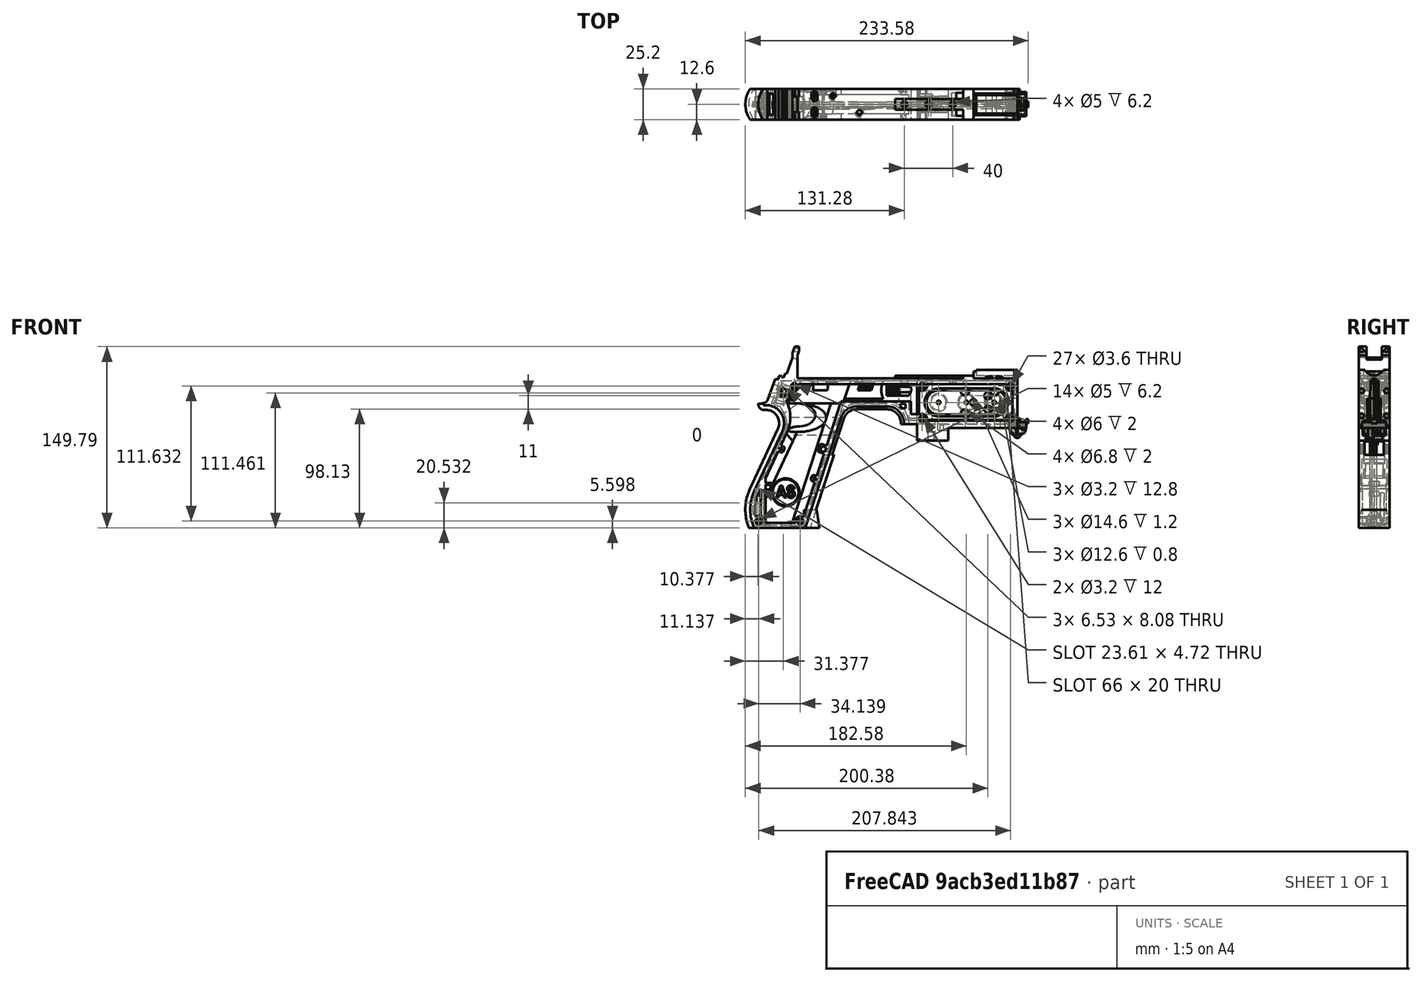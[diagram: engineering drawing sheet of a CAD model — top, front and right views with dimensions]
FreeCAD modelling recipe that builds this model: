
FCSTD DOCUMENT  (FreeCAD 1.0R39319 (Git))
Label: PICON-OF_ver_34_prova_spazio_switch_alette
License: All rights reserved
LicenseURL: https://en.wikipedia.org/wiki/All_rights_reserved
objects: Sketcher::SketchObject×119, Part::Extrusion×75, Part::Cut×47, PartDesign::Pad×19, PartDesign::Pocket×14, PartDesign::Chamfer×14, PartDesign::Body×8, Part::MultiFuse×6, PartDesign::Fillet×6, PartDesign::SubtractivePipe×4, Part::Part2DObjectPython×4, PartDesign::SubtractiveLoft×4, PartDesign::Plane×2, PartDesign::SubShapeBinder×2, Part::Sweep×1, PartDesign::ShapeBinder×1, PartDesign::FeatureBase×1, Part::Cone×1, Part::Chamfer×1, Mesh::Feature×1, +1 more types
note: 572 computed .brp shape members not serialized (recipe doc carries the construction recipe); baked Part::Feature solids carry a one-line shape summary decoded from their .brp

FEATURE [Sketcher::SketchObject] Sketch  label="corpo principale"
  ArcFitTolerance = 1e-06
  AttacherType = Attacher::AttachEngine3D
  AttachmentSupport = -> [XZ_Plane]
  FullyConstrained = true
  MakeInternals = false
  MapMode = 5
  Placement = pos=(0,0,0) rot=(1,0,0;1.5708rad)
  sketch-geometry (65):
    g0: LineSegment StartX=0 StartY=0 StartZ=0 EndX=-57.2 EndY=0 EndZ=0
    g1: LineSegment StartX=-57.2 StartY=0 StartZ=0 EndX=-57.2 EndY=-10.4 EndZ=0
    g2: LineSegment StartX=-57.2 StartY=-10.4 StartZ=0 EndX=-82.8 EndY=-10.4 EndZ=0
    g3: LineSegment StartX=-82.8 StartY=-10.4 StartZ=0 EndX=-82.8 EndY=3.2 EndZ=0
    g4: LineSegment StartX=-82.8 StartY=3.2 StartZ=0 EndX=-93.6 EndY=3.2 EndZ=0
    g5: LineSegment StartX=-93.6 StartY=3.2 StartZ=0 EndX=-93.6 EndY=4 EndZ=0
    g6: LineSegment StartX=-107.6 StartY=18 StartZ=0 EndX=-132.428 EndY=18 EndZ=0
    g7: LineSegment StartX=-145.743 StartY=8.32624 StartZ=0 EndX=-175.232 EndY=-82.4316 EndZ=0
    g8: LineSegment StartX=-175.232 StartY=-82.4316 StartZ=0 EndX=-217.232 EndY=-82.4316 EndZ=0
    g9: LineSegment StartX=-217.232 StartY=-52.1862 StartZ=0 EndX=-193.988 EndY=-2.33927 EndZ=0
    g10: LineSegment StartX=-206.196 StartY=23.0857 StartZ=0 EndX=-199.861 EndY=40.4914 EndZ=0
    g11: LineSegment StartX=-199.861 StartY=40.4914 StartZ=0 EndX=-197.061 EndY=40.4914 EndZ=0
    g12: LineSegment StartX=-197.061 StartY=40.4914 StartZ=0 EndX=-197.061 EndY=42.8914 EndZ=0
    g13: LineSegment StartX=-197.061 StartY=42.8914 StartZ=0 EndX=-194.261 EndY=42.8914 EndZ=0
    g14: LineSegment StartX=-194.261 StartY=42.8914 StartZ=0 EndX=-194.535 EndY=42.1397 EndZ=0
    g15: LineSegment StartX=-194.535 StartY=42.1397 StartZ=0 EndX=-193.031 EndY=41.5924 EndZ=0
    g16: LineSegment StartX=-193.031 StartY=41.5924 StartZ=0 EndX=-191.663 EndY=45.3512 EndZ=0
    g17: LineSegment StartX=-191.663 StartY=45.3512 StartZ=0 EndX=-190.536 EndY=44.9408 EndZ=0
    g18: LineSegment StartX=-190.536 StartY=44.9408 StartZ=0 EndX=-185.747 EndY=58.0965 EndZ=0
    g19: LineSegment StartX=-185.747 StartY=58.0965 StartZ=0 EndX=-185.747 EndY=62.0965 EndZ=0
    g20: LineSegment StartX=-185.747 StartY=62.0965 StartZ=0 EndX=-183.832 EndY=67.3588 EndZ=0
    g21: LineSegment StartX=-183.832 StartY=67.3588 StartZ=0 EndX=-180.232 EndY=67.3588 EndZ=0
    g22: LineSegment StartX=-180.232 StartY=67.3588 StartZ=0 EndX=-180.232 EndY=63.7588 EndZ=0
    g23: LineSegment StartX=-180.232 StartY=63.7588 StartZ=0 EndX=-181.6 EndY=60 EndZ=0
    g24: LineSegment StartX=-181.6 StartY=60 StartZ=0 EndX=-181.6 EndY=41.2 EndZ=0
    g25: LineSegment StartX=-181.6 StartY=41.2 StartZ=0 EndX=-100.8 EndY=41.2 EndZ=0
    g26: LineSegment StartX=-36 StartY=43.2 StartZ=0 EndX=-36 EndY=41.2 EndZ=0
    g27: LineSegment StartX=0 StartY=48 StartZ=0 EndX=0 EndY=0 EndZ=0
    g28: LineSegment StartX=-209.901 StartY=19.85 StartZ=0 EndX=-209.901 EndY=20.1 EndZ=0
    g29: LineSegment StartX=-208.001 StartY=22 StartZ=0 EndX=-207.747 EndY=22 EndZ=0
    g30: LineSegment StartX=-207.583 StartY=19 StartZ=0 EndX=-209.051 EndY=19 EndZ=0
    g31: ArcOfCircle CenterX=-208.001 CenterY=20.1 CenterZ=0 NormalX=0 NormalY=0 NormalZ=1 AngleXU=0 Radius=1.9 StartAngle=1.5708 EndAngle=3.14159
    g32: GeomPoint [constr] X=-209.901 Y=22 Z=0
    g33: ArcOfCircle CenterX=-209.051 CenterY=19.85 CenterZ=0 NormalX=0 NormalY=0 NormalZ=1 AngleXU=0 Radius=0.85 StartAngle=3.14159 EndAngle=4.71239
    g34: GeomPoint [constr] X=-209.901 Y=19 Z=0
    g35: ArcOfCircle CenterX=-207.747 CenterY=23.65 CenterZ=0 NormalX=0 NormalY=0 NormalZ=1 AngleXU=0 Radius=1.65 StartAngle=4.71239 EndAngle=5.93412
    g36: GeomPoint [constr] X=-206.591 Y=22 Z=0
    g37: LineSegment StartX=-4 StartY=6 StartZ=0 EndX=-4 EndY=36.4 EndZ=0
    g38: LineSegment StartX=-4 StartY=36.4 StartZ=0 EndX=-185.2 EndY=36.4 EndZ=0
    g39: LineSegment StartX=-185.2 StartY=36.4 StartZ=0 EndX=-190.441 EndY=22 EndZ=0
    g40: LineSegment StartX=-214.575 StartY=-78.4316 StartZ=0 EndX=-178.142 EndY=-78.4316 EndZ=0
    g41: LineSegment StartX=-178.142 StartY=-78.4316 StartZ=0 EndX=-145.51 EndY=22 EndZ=0
    g42: LineSegment StartX=-145.51 StartY=22 StartZ=0 EndX=-87.91 EndY=22 EndZ=0
    g43: LineSegment StartX=-87.91 StartY=22 StartZ=0 EndX=-87.91 EndY=11.6 EndZ=0
    g44: LineSegment StartX=-87.91 StartY=11.6 StartZ=0 EndX=-80.11 EndY=11.6 EndZ=0
    g45: LineSegment StartX=-80.11 StartY=11.6 StartZ=0 EndX=-80.11 EndY=6 EndZ=0
    g46: LineSegment StartX=-80.11 StartY=6 StartZ=0 EndX=-4 EndY=6 EndZ=0
    g47: LineSegment StartX=-190.363 StartY=-4.02975 StartZ=0 EndX=-213.607 EndY=-53.8767 EndZ=0
    g48: ArcOfCircle CenterX=-132.428 CenterY=4 CenterZ=0 NormalX=0 NormalY=0 NormalZ=1 AngleXU=0 Radius=14 StartAngle=1.5708 EndAngle=2.82743
    g49: GeomPoint [constr] X=-142.6 Y=18 Z=0
    g50: ArcOfCircle CenterX=-107.6 CenterY=4 CenterZ=0 NormalX=0 NormalY=0 NormalZ=1 AngleXU=0 Radius=14 StartAngle=0 EndAngle=1.5708
    g51: GeomPoint [constr] X=-93.6 Y=18 Z=0
    g52: ArcOfCircle CenterX=-184.801 CenterY=-67.3089 CenterZ=0 NormalX=0 NormalY=0 NormalZ=1 AngleXU=0 Radius=35.7833 StartAngle=2.70526 EndAngle=3.57792
    g53: ArcOfCircle CenterX=-207.583 CenterY=4 CenterZ=0 NormalX=0 NormalY=0 NormalZ=1 AngleXU=0 Radius=15 StartAngle=5.84685 EndAngle=7.85398
    g54: LineSegment [constr] StartX=-213.607 StartY=-53.8767 StartZ=0 EndX=-217.232 EndY=-52.1862 EndZ=0
    g55: ArcOfCircle CenterX=-184.801 CenterY=-67.3089 CenterZ=0 NormalX=0 NormalY=0 NormalZ=1 AngleXU=0 Radius=31.7833 StartAngle=2.70526 EndAngle=3.49911
    g56: ArcOfCircle CenterX=-218.095 CenterY=8.90192 CenterZ=0 NormalX=0 NormalY=0 NormalZ=1 AngleXU=0 Radius=30.5989 StartAngle=5.84685 EndAngle=6.72553
    g57: LineSegment StartX=-44.6 StartY=43.2 StartZ=0 EndX=-36 EndY=43.2 EndZ=0
    g58: LineSegment StartX=-100.8 StartY=41.2 StartZ=0 EndX=-44.6 EndY=41.2 EndZ=0
    g59: LineSegment StartX=-44.6 StartY=41.2 StartZ=0 EndX=-44.6 EndY=43.2 EndZ=0
    g60: LineSegment StartX=-2.4 StartY=48 StartZ=0 EndX=0 EndY=48 EndZ=0
    g61: LineSegment StartX=-36 StartY=41.2 StartZ=0 EndX=-2.4 EndY=41.2 EndZ=0
    g62: LineSegment StartX=-2.4 StartY=41.2 StartZ=0 EndX=-2.4 EndY=48 EndZ=0
    g63: LineSegment [constr] StartX=-181.6 StartY=36.4 StartZ=0 EndX=-152.209 EndY=36.4 EndZ=0
    g64: LineSegment [constr] StartX=-181.6 StartY=36.4 StartZ=0 EndX=-130.41 EndY=36.4 EndZ=0
  constraints (183):
    c: Coincident(g-1,g0)
    c: PointOnObject(g0,g-1)
    c: Coincident(g0,g1)
    c: Vertical(g1)
    c: Coincident(g1,g2)
    c: Horizontal(g2)
    c: Coincident(g2,g3)
    c: Vertical(g3)
    c: Coincident(g3,g4)
    c: Coincident(g4,g5)
    c: Vertical(g5)
    c: Horizontal(g6)
    c: Coincident(g7,g8)
    c: Horizontal(g8)
    c: Coincident(g10,g11)
    c: Horizontal(g11)
    c: Coincident(g11,g12)
    c: Vertical(g12)
    c: Coincident(g12,g13)
    c: Horizontal(g13)
    c: Coincident(g13,g14)
    c: Coincident(g14,g15)
    c: Coincident(g15,g16)
    c: Coincident(g16,g17)
    c: Coincident(g17,g18)
    c: Coincident(g18,g19)
    c: Vertical(g19)
    c: Coincident(g19,g20)
    c: Coincident(g20,g21)
    c: Horizontal(g21)
    c: Coincident(g21,g22)
    c: Vertical(g22)
    c: Coincident(g22,g23)
    c: Coincident(g23,g24)
    c: Vertical(g24)
    c: Coincident(g24,g25)
    c: Horizontal(g25)
    c: Coincident(g57,g26)
    c: Vertical(g26)
    c: Coincident(g26,g61)
    c: PointOnObject(g60,g-2)
    c: Coincident(g60,g27)
    c: Coincident(g27,g0)
    c: DistanceY(g27,g27) = 48
    c: DistanceY(g1,g1) = 10.4
    c: DistanceX(g0,g0) = 57.2
    c: DistanceX(g2,g2) = 25.6
    c: Horizontal(g4)
    c: DistanceY(g3,g3) = 13.6
    c: DistanceX(g4,g4) = 10.8
    c: DistanceY(g5,g51) = 14.8
    c: DistanceX(g49,g51) = 49
    c: Distance(g7,g49) = 105.6
    c: DistanceX(g61,g60) = 36
    c: DistanceX(g25,g25) = 80.8
    c: DistanceY(g24,g24) = 18.8
    c: DistanceY(g22,g22) = 3.6
    c: Distance(g23) = 4
    c: Angle(g-1,g23) = 1.22173
    c: DistanceX(g21,g21) = 3.6
    c: Distance(g20) = 5.6
    c: Angle(g-1,g20) = 1.22173
    c: DistanceY(g19,g19) = 4
    c: Distance(g18) = 14
    c: Angle(g-1,g18) = 1.22173
    c: Distance(g17) = 1.2
    c: Distance(g16) = 4
    c: Angle(g16) = 1.22173
    c: Perpendicular(g18,g17)
    c: Distance(g15) = 1.6
    c: Perpendicular(g16,g15)
    c: Distance(g14) = 0.8
    c: DistanceX(g13,g13) = 2.8
    c: Perpendicular(g15,g14)
    c: DistanceY(g12,g12) = 2.4
    c: DistanceX(g11,g11) = 2.8
    c: Distance(g9) = 55
    c: Angle(g9,g-1) = 2.00713
    c: Horizontal(g29)
    c: Vertical(g28)
    c: Horizontal(g30)
    c: PointOnObject(g32,g29)
    c: PointOnObject(g32,g28)
    c: Tangent(g29,g31) = 1.5708
    c: Tangent(g28,g31) = 1.5708
    c: PointOnObject(g34,g28)
    c: PointOnObject(g34,g30)
    c: Tangent(g28,g33) = 1.5708
    c: Tangent(g30,g33) = 1.5708
    c: PointOnObject(g36,g29)
    c: PointOnObject(g36,g10)
    c: Tangent(g29,g35) = -1.5708
    c: Tangent(g10,g35) = -1.5708
    c: Angle(g-1,g10) = 1.22173
    c: Radius(g35) = 1.65
    c: Vertical(g37)
    c: Coincident(g37,g38)
    c: Horizontal(g38)
    c: Coincident(g38,g39)
    c: Horizontal(g40)
    c: Coincident(g40,g41)
    c: Coincident(g41,g42)
    c: Horizontal(g42)
    c: Coincident(g42,g43)
    c: Vertical(g43)
    c: Coincident(g43,g44)
    c: Horizontal(g44)
    c: Coincident(g44,g45)
    c: Vertical(g45)
    c: Coincident(g45,g46)
    c: Coincident(g46,g37)
    c: Horizontal(g46)
    c: DistanceY(g0,g37) = 6
    c: DistanceX(g37,g0) = 4
    c: DistanceY(g37,g25) = 4.8
    c: DistanceX(g38,g38) = 181.2
    c: DistanceX(g42,g42) = 57.6
    c: DistanceY(g49,g41) = 4
    c: DistanceX(g41,g49) = 2.91
    c: DistanceY(g43,g43) = 10.4
    c: DistanceX(g44,g44) = 7.8
    c: DistanceY(g7,g40) = 4
    c: Distance(g47) = 55
    c: Angle(g-1,g39) = 1.22173
    c: PointOnObject(g49,g7)
    c: PointOnObject(g49,g6)
    c: Tangent(g7,g48) = -1.5708
    c: Tangent(g6,g48) = -1.5708
    c: PointOnObject(g51,g5)
    c: PointOnObject(g51,g6)
    c: Tangent(g5,g50) = -1.5708
    c: Tangent(g6,g50) = -1.5708
    c: Radius(g50) = 14
    c: Radius(g48) = 14
    c: DistanceX(g8,g8) = 42
    c: Angle(g7,g-1) = 1.88496
    c: Parallel(g41,g7)
    c: Parallel(g47,g9)
    c: Coincident(g52,g8)
    c: Tangent(g52,g9) = 1.5708
    c: DistanceX(g9,g8) = 0
    c: Tangent(g53,g9) = -1.5708
    c: Tangent(g53,g30) = -1.5708
    c: Diameter(g53) = 30
    c: DistanceY(g53,g0) = -4
    c: Coincident(g54,g47)
    c: Distance(g54) = 4
    c: Coincident(g54,g9)
    c: Coincident(g55,g40)
    c: Tangent(g55,g47) = -1.5708
    c: Coincident(g52,g55)
    c: Coincident(g56,g39)
    c: Tangent(g56,g47) = 1.5708
    c: Horizontal(g57)
    c: DistanceX(g57,g57) = 8.6
    c: Coincident(g58,g25)
    c: Horizontal(g58)
    c: Coincident(g59,g58)
    c: Vertical(g59)
    c: DistanceY(g58,g57) = 2
    c: DistanceX(g58,g58) = 56.2
    c: Coincident(g59,g57)
    c: DistanceY(g41,g36) = 0
    c: DistanceY(g36,g39) = 0
    c: DistanceY(g28,g28) = 0.25
    c: DistanceX(g30,g36) = 2.46
    c: DistanceX(g28,g29) = 1.9
    c: Coincident(g62,g60)
    c: Horizontal(g60)
    c: DistanceX(g62,g27) = 2.4
    c: Coincident(g61,g62)
    c: DistanceY(g26,g26) = 2
    c: Vertical(g62)
    c: DistanceY(g61,g60) = 6.8
    c: Horizontal(g61)
    c: Distance(g63) = 29.391
    c: PointOnObject(g63,g38)
    c: PointOnObject(g63,g38)
    c: Distance(g64) = 51.19
    c: PointOnObject(g64,g38)
    c: PointOnObject(g64,g38)
    c: DistanceX(g24,g63) = 0
    c: DistanceX(g24,g64) = 0
FEATURE [Part::Extrusion] Extrude  label="Extrude corpo principale"
  Base = -> Sketch
  Dir = (0,-1,2e-16)
  DirMode = 2
  FaceMakerClass = Part::FaceMakerBullseye
  FaceMakerMode = 3
  LengthFwd = 25.2
  LengthRev = 12.6
  Solid = true
  Symmetric = true
FEATURE [Sketcher::SketchObject] Sketch002  label="scavo grilletto"
  ArcFitTolerance = 1e-06
  AttachmentSupport = -> [XZ_Plane]
  ExternalGeometry = -> [Sketch]
  FullyConstrained = true
  MakeInternals = false
  MapMode = 5
  Placement = pos=(0,0,0) rot=(1,0,0;1.5708rad)
  sketch-geometry (4):
    g0: LineSegment StartX=-89.51 StartY=22 StartZ=0 EndX=-152.71 EndY=22 EndZ=0
    g1: LineSegment StartX=-152.71 StartY=22 StartZ=0 EndX=-167.006 EndY=-22 EndZ=0
    g2: LineSegment StartX=-167.006 StartY=-22 StartZ=0 EndX=-89.51 EndY=-22 EndZ=0
    g3: LineSegment StartX=-89.51 StartY=-22 StartZ=0 EndX=-89.51 EndY=22 EndZ=0
  constraints (12):
    c: Horizontal(g0)
    c: Coincident(g0,g1)
    c: Coincident(g1,g2)
    c: Horizontal(g2)
    c: Coincident(g2,g3)
    c: Coincident(g3,g0)
    c: Vertical(g3)
    c: Angle(g1,g0) = 1.88496
    c: DistanceY(g3,g3) = 44
    c: DistanceX(g0,g0) = 63.2
    c: DistanceX(g0,g-3) = 1.6
    c: DistanceY(g-3,g0) = 0
FEATURE [Sketcher::SketchObject] Sketch004  label="traiettoria arrotondamento impugnatura anteriore"
  ArcFitTolerance = 1e-06
  AttachmentSupport = -> [XZ_Plane]
  ExternalGeometry = -> [Sketch]
  FullyConstrained = true
  MakeInternals = false
  MapMode = 5
  Placement = pos=(0,0,0) rot=(1,0,0;1.5708rad)
  sketch-geometry (13):
    g0: LineSegment StartX=-175.232 StartY=-82.4316 StartZ=0 EndX=-145.743 EndY=8.32624 EndZ=0
    g1: LineSegment StartX=-93.6 StartY=3.2 StartZ=0 EndX=-93.6 EndY=4 EndZ=0
    g2: LineSegment StartX=-132.428 StartY=18 StartZ=0 EndX=-107.6 EndY=18 EndZ=0
    g3: ArcOfCircle CenterX=-132.428 CenterY=4 CenterZ=0 NormalX=0 NormalY=0 NormalZ=1 AngleXU=0 Radius=14 StartAngle=1.5708 EndAngle=2.82743
    g4: ArcOfCircle CenterX=-107.6 CenterY=4 CenterZ=0 NormalX=0 NormalY=0 NormalZ=1 AngleXU=0 Radius=14 StartAngle=0 EndAngle=1.5708
    g5: LineSegment StartX=-175.232 StartY=-82.4316 StartZ=0 EndX=-217.232 EndY=-82.4316 EndZ=0
    g6: LineSegment StartX=-217.232 StartY=-52.1862 StartZ=0 EndX=-193.988 EndY=-2.33927 EndZ=0
    g7: LineSegment StartX=-209.051 StartY=19 StartZ=0 EndX=-207.583 EndY=19 EndZ=0
    g8: LineSegment StartX=-209.901 StartY=20.1 StartZ=0 EndX=-209.901 EndY=19.85 EndZ=0
    g9: ArcOfCircle CenterX=-184.801 CenterY=-67.3089 CenterZ=0 NormalX=0 NormalY=0 NormalZ=1 AngleXU=0 Radius=35.7833 StartAngle=2.70526 EndAngle=3.57792
    g10: ArcOfCircle CenterX=-207.583 CenterY=4 CenterZ=0 NormalX=0 NormalY=0 NormalZ=1 AngleXU=0 Radius=15 StartAngle=5.84685 EndAngle=7.85398
    g11: ArcOfCircle CenterX=-209.051 CenterY=19.85 CenterZ=0 NormalX=0 NormalY=0 NormalZ=1 AngleXU=0 Radius=0.85 StartAngle=3.14159 EndAngle=4.71239
    g12: ArcOfCircle CenterX=-208.001 CenterY=20.1 CenterZ=0 NormalX=0 NormalY=0 NormalZ=1 AngleXU=0 Radius=1.9 StartAngle=1.5708 EndAngle=3.14159
  constraints (26):
    c: Coincident(g0,g-3)
    c: Coincident(g0,g-6)
    c: Coincident(g1,g-8)
    c: Coincident(g1,g-7)
    c: Coincident(g2,g-5)
    c: Coincident(g2,g-4)
    c: Coincident(g3,g2)
    c: Tangent(g3,g0) = 1.5708
    c: Coincident(g4,g1)
    c: Tangent(g4,g2) = 1.5708
    c: Coincident(g5,g0)
    c: Coincident(g5,g-9)
    c: Coincident(g6,g-12)
    c: Coincident(g6,g-11)
    c: Coincident(g7,g-15)
    c: Coincident(g7,g-14)
    c: Coincident(g8,g-16)
    c: Coincident(g8,g-17)
    c: Tangent(g9,g6) = 1.5708
    c: Coincident(g9,g5)
    c: Coincident(g10,g7)
    c: Tangent(g10,g6) = -1.5708
    c: Tangent(g11,g7) = -1.5708
    c: Coincident(g11,g8)
    c: Tangent(g12,g8) = -1.5708
    c: Coincident(g12,g-17)
FEATURE [PartDesign::Plane] DatumPlane  label="Piano per disegno arrotondamento impugnatura"
  AttachmentSupport = -> [Sketch]
  Length = 68.5841
  MapMode = 7
  Placement = pos=(-145.743,1.8e-15,8.32624) rot=(0.154555,0.154555,0.97582;1.59527rad)
  ResizeMode = 0
  Width = 191.269
FEATURE [Sketcher::SketchObject] Sketch005  label="forma arrotondamento impugnatura anteriore"
  ArcFitTolerance = 1e-06
  AttachmentSupport = -> [DatumPlane]
  FullyConstrained = true
  MakeInternals = false
  MapMode = 5
  Placement = pos=(-145.743,1.8e-15,8.32624) rot=(0.154555,0.154555,0.97582;1.59527rad)
  sketch-geometry (5):
    g0: GeomPoint [constr] X=0 Y=-4 Z=0
    g1: GeomPoint [constr] X=-12.6 Y=7.1e-15 Z=0
    g2: GeomPoint [constr] X=12.6 Y=4.97e-14 Z=0
    g3: LineSegment StartX=-12.6 StartY=7.1e-15 StartZ=0 EndX=12.6 EndY=4.97e-14 EndZ=0
    g4: ArcOfCircle CenterX=-3.88e-14 CenterY=17.845 CenterZ=0 NormalX=0 NormalY=0 NormalZ=1 AngleXU=0 Radius=21.845 StartAngle=4.09759 EndAngle=5.32718
  constraints (11):
    c: DistanceY(g0,g-1) = 4
    c: DistanceX(g-1,g0) = 0
    c: DistanceX(g1,g-1) = 12.6
    c: DistanceX(g-1,g2) = 12.6
    c: DistanceY(g-1,g2) = 0
    c: DistanceY(g-1,g1) = 0
    c: Coincident(g3,g1)
    c: Coincident(g3,g2)
    c: Coincident(g4,g1)
    c: Coincident(g4,g2)
    c: PointOnObject(g0,g4)
FEATURE [Part::Sweep] Sweep  label="Sweep impugnatura"
  Frenet = true
  Sections = -> [Sketch005]
  Solid = true
  Spine = -> Sketch [Edge32,Edge33,Edge34,Edge35,Edge36,Edge37,Edge38,Edge39,Edge40,Edge41,Edge42,Edge43,Edge44]
  Transition = 1
FEATURE [Sketcher::SketchObject] Sketch008  label="buchi e pulizie varie"
  ArcFitTolerance = 1e-06
  AttachmentSupport = -> [XZ_Plane]
  ExternalGeometry = -> [Sketch]
  FullyConstrained = true
  MakeInternals = false
  MapMode = 5
  Placement = pos=(0,0,0) rot=(1,0,0;1.5708rad)
  sketch-geometry (26):
    g0: LineSegment StartX=-96.278 StartY=20.155 StartZ=0 EndX=-92.278 EndY=20.155 EndZ=0
    g1: LineSegment StartX=-92.278 StartY=20.155 StartZ=0 EndX=-92.278 EndY=16.155 EndZ=0
    g2: LineSegment StartX=-92.278 StartY=16.155 StartZ=0 EndX=-96.278 EndY=16.155 EndZ=0
    g3: LineSegment StartX=-96.278 StartY=16.155 StartZ=0 EndX=-96.278 EndY=20.155 EndZ=0
    g4: LineSegment StartX=-222.232 StartY=-82.4316 StartZ=0 EndX=-170.232 EndY=-82.4316 EndZ=0
    g5: LineSegment StartX=-170.232 StartY=-82.4316 StartZ=0 EndX=-170.232 EndY=-86.4316 EndZ=0
    g6: LineSegment StartX=-170.232 StartY=-86.4316 StartZ=0 EndX=-222.232 EndY=-86.4316 EndZ=0
    g7: LineSegment StartX=-222.232 StartY=-86.4316 StartZ=0 EndX=-222.232 EndY=-82.4316 EndZ=0
    g8: LineSegment StartX=-213.901 StartY=20.1 StartZ=0 EndX=-213.901 EndY=26 EndZ=0
    g9: LineSegment StartX=-213.901 StartY=26 StartZ=0 EndX=-206.196 EndY=26 EndZ=0
    g10: LineSegment StartX=-17.4 StartY=42.8 StartZ=0 EndX=-12.4 EndY=42.8 EndZ=0
    g11: LineSegment StartX=-12.4 StartY=42.8 StartZ=0 EndX=-12.4 EndY=41.2 EndZ=0
    g12: LineSegment StartX=-12.4 StartY=41.2 StartZ=0 EndX=-17.4 EndY=41.2 EndZ=0
    g13: LineSegment StartX=-17.4 StartY=41.2 StartZ=0 EndX=-17.4 EndY=42.8 EndZ=0
    g14: LineSegment StartX=-25.9 StartY=42.8 StartZ=0 EndX=-20.9 EndY=42.8 EndZ=0
    g15: LineSegment StartX=-20.9 StartY=42.8 StartZ=0 EndX=-20.9 EndY=41.2 EndZ=0
    g16: LineSegment StartX=-20.9 StartY=41.2 StartZ=0 EndX=-25.9 EndY=41.2 EndZ=0
    g17: LineSegment StartX=-25.9 StartY=41.2 StartZ=0 EndX=-25.9 EndY=42.8 EndZ=0
    g18: GeomPoint [constr] X=-206.196 Y=23.0857 Z=0
    g19: GeomPoint [constr] X=-213.901 Y=20.1 Z=0
    g20: BSplineCurve PolesCount=4 KnotsCount=2 Degree=3 IsPeriodic=0
    g21-g24: Circle [constr] x4 (B-spline internal-alignment scaffolding for g20; pole/knot coordinates omitted)
    g25: LineSegment StartX=-206.196 StartY=26 StartZ=0 EndX=-206.196 EndY=23.0857 EndZ=0
  constraints (73):
    c: Horizontal(g0)
    c: Coincident(g1,g0)
    c: Vertical(g1)
    c: Coincident(g2,g1)
    c: Horizontal(g2)
    c: Coincident(g3,g2)
    c: Coincident(g3,g0)
    c: Vertical(g3)
    c: DistanceX(g0,g-4) = 4.368
    c: DistanceY(g0,g-4) = 1.845
    c: DistanceY(g1,g1) = 4
    c: DistanceX(g2,g2) = 4
    c: Horizontal(g4)
    c: Coincident(g5,g4)
    c: Vertical(g5)
    c: Coincident(g6,g5)
    c: Horizontal(g6)
    c: Coincident(g7,g6)
    c: Coincident(g7,g4)
    c: Vertical(g7)
    c: DistanceY(g7,g7) = 4
    c: DistanceX(g4,g-5) = 5
    c: DistanceX(g-5,g4) = 5
    c: DistanceY(g4,g-5) = 0
    c: Coincident(g9,g8)
    c: Parallel(g9,g-6)
    c: DistanceX(g8,g-8) = 4
    c: Horizontal(g10)
    c: Coincident(g11,g10)
    c: Vertical(g11)
    c: Coincident(g12,g11)
    c: Horizontal(g12)
    c: Coincident(g13,g12)
    c: Coincident(g13,g10)
    c: Vertical(g13)
    c: Horizontal(g14)
    c: Coincident(g15,g14)
    c: Vertical(g15)
    c: Coincident(g16,g15)
    c: Horizontal(g16)
    c: Coincident(g17,g16)
    c: Coincident(g17,g14)
    c: Vertical(g17)
    c: DistanceY(g11,g10) = 1.6
    c: DistanceX(g10,g10) = 5
    c: DistanceY(g15,g14) = 1.6
    c: DistanceX(g14,g14) = 5
    c: DistanceX(g15,g12) = 3.5
    c: DistanceX(g11,g-9) = 10
    c: DistanceY(g-9,g11) = 0
    c: DistanceY(g-9,g15) = 0
    c: Perpendicular(g8,g9)
    c: DistanceY(g-7,g9) = 4
    c: DistanceY(g8,g-8) = 0
    c: InternalAlignment(g18,g20)
    c: InternalAlignment(g19,g20)
    c: InternalAlignment(g21,g20)
    c: Weight(g21) = 1
    c: InternalAlignment(g22,g20)
    c: Equal(g22,g21)
    c: InternalAlignment(g23,g20)
    c: Equal(g23,g21)
    c: InternalAlignment(g24,g20)
    c: Equal(g24,g21)
    c: Coincident(g18,g-12)
    c: Coincident(g19,g8)
    c: Coincident(g25,g9)
    c: Coincident(g25,g20)
    c: Vertical(g25)
    c: DistanceY(g20,g23) = 0
    c: DistanceY(g22,g18) = 2.26
    c: DistanceX(g22,g18) = 0.93
    c: DistanceX(g20,g23) = 2.9
FEATURE [Part::Extrusion] Extrude004  label="Extrude Buchi e pulizie varie"
  Base = -> Sketch008
  Dir = (0,-1,2e-16)
  DirMode = 2
  FaceMakerClass = Part::FaceMakerBullseye
  FaceMakerMode = 3
  LengthFwd = 25.2
  LengthRev = 0
  Solid = true
  Symmetric = true
FEATURE [Sketcher::SketchObject] Sketch009  label="rinforzi"
  ArcFitTolerance = 1e-06
  AttachmentSupport = -> [XZ_Plane]
  ExternalGeometry = -> [Sketch]
  FullyConstrained = true
  MakeInternals = false
  MapMode = 5
  Placement = pos=(0,0,0) rot=(1,0,0;1.5708rad)
  sketch-geometry (9):
    g0: LineSegment StartX=-87.91 StartY=22 StartZ=0 EndX=-87.91 EndY=36.4 EndZ=0
    g1: LineSegment StartX=-87.91 StartY=36.4 StartZ=0 EndX=-97.91 EndY=36.4 EndZ=0
    g2: LineSegment StartX=-97.91 StartY=36.4 StartZ=0 EndX=-97.91 EndY=22 EndZ=0
    g3: LineSegment StartX=-97.91 StartY=22 StartZ=0 EndX=-87.91 EndY=22 EndZ=0
    g4: LineSegment StartX=-149.713 StartY=9.06563 StartZ=0 EndX=-154.586 EndY=-5.93437 EndZ=0
    g5: LineSegment StartX=-154.586 StartY=-5.93437 StartZ=0 EndX=-191.863 EndY=-5.93437 EndZ=0
    g6: LineSegment StartX=-191.863 StartY=-5.93437 StartZ=0 EndX=-191.863 EndY=9.06563 EndZ=0
    g7: LineSegment StartX=-191.863 StartY=9.06563 StartZ=0 EndX=-149.713 EndY=9.06563 EndZ=0
    g8: LineSegment [constr] StartX=-145.51 StartY=22 StartZ=0 EndX=-149.713 EndY=9.06563 EndZ=0
  constraints (25):
    c: Vertical(g0)
    c: Coincident(g1,g0)
    c: Horizontal(g1)
    c: Coincident(g2,g1)
    c: Vertical(g2)
    c: Coincident(g3,g2)
    c: Coincident(g3,g0)
    c: Horizontal(g3)
    c: Coincident(g0,g-4)
    c: DistanceX(g3,g3) = 10
    c: DistanceY(g0,g-3) = 0
    c: Coincident(g5,g4)
    c: Horizontal(g5)
    c: Coincident(g6,g5)
    c: Vertical(g6)
    c: Coincident(g7,g6)
    c: Coincident(g7,g4)
    c: Horizontal(g7)
    c: Distance(g8) = 13.6
    c: Parallel(g-6,g8)
    c: Coincident(g-6,g8)
    c: Parallel(g4,g-6)
    c: DistanceY(g4,g4) = 15
    c: Coincident(g4,g8)
    c: DistanceX(g-5,g5) = -1.5
FEATURE [Part::Extrusion] Extrude001  label="Extrude scavo grilletto"
  Base = -> Sketch002
  Dir = (0,-1,2e-16)
  DirMode = 2
  FaceMakerClass = Part::FaceMakerBullseye
  FaceMakerMode = 3
  LengthFwd = 16
  LengthRev = 0
  Solid = true
  Symmetric = true
FEATURE [Part::Extrusion] Extrude005  label="Extrude Rinforzi"
  Base = -> Sketch009
  Dir = (0,-1,2e-16)
  DirMode = 2
  FaceMakerClass = Part::FaceMakerBullseye
  FaceMakerMode = 3
  LengthFwd = 2
  LengthRev = 0
  Placement = pos=(0,12.6,0) rot=(0,0,1;0rad)
  Solid = true
  Symmetric = false
FEATURE [PartDesign::ShapeBinder] CopyCut
  TraceSupport = false
FEATURE [PartDesign::Plane] DatumPlane001
  AttachmentSupport = -> [CopyCut]
  Length = 60
  MapMode = 5
  Placement = pos=(0,12.6,0) rot=(0,0.707107,0.707107;3.14159rad)
  ResizeMode = 0
  Width = 60
FEATURE [Sketcher::SketchObject] Sketch010  label="buco neopixel"
  ArcFitTolerance = 1e-06
  AttachmentSupport = -> [XZ_Plane]
  ExternalGeometry = -> [Sketch]
  FullyConstrained = true
  MakeInternals = false
  MapMode = 5
  Placement = pos=(0,0,0) rot=(1,0,0;1.5708rad)
  sketch-geometry (5):
    g0: LineSegment [constr] StartX=-199.861 StartY=40.4914 StartZ=0 EndX=-201.368 EndY=36.3521 EndZ=0
    g1: LineSegment StartX=-201.368 StartY=36.3521 StartZ=0 EndX=-204.932 EndY=26.5605 EndZ=0
    g2: LineSegment StartX=-201.368 StartY=36.3521 StartZ=0 EndX=-180.2 EndY=28.6477 EndZ=0
    g3: LineSegment StartX=-180.2 StartY=28.6477 StartZ=0 EndX=-183.764 EndY=18.8561 EndZ=0
    g4: LineSegment StartX=-183.764 StartY=18.8561 StartZ=0 EndX=-204.932 EndY=26.5605 EndZ=0
  constraints (14):
    c: Parallel(g0,g-3)
    c: Distance(g0) = 4.405
    c: Coincident(g0,g-3)
    c: Coincident(g2,g1)
    c: Coincident(g3,g2)
    c: Coincident(g4,g3)
    c: Coincident(g4,g1)
    c: Parallel(g1,g-3)
    c: Distance(g1) = 10.42
    c: Coincident(g1,g0)
    c: Parallel(g2,g4)
    c: Perpendicular(g1,g2)
    c: DistanceX(g-4,g2) = 5
    c: Parallel(g3,g1)
FEATURE [Part::Extrusion] Extrude006  label="Extrude buco neopixel"
  Base = -> Sketch010
  Dir = (0,-1,2e-16)
  DirMode = 2
  FaceMakerClass = Part::FaceMakerBullseye
  FaceMakerMode = 3
  LengthFwd = 17.2
  LengthRev = 0
  Solid = true
  Symmetric = true
FEATURE [Sketcher::SketchObject] Sketch011  label="fermo grilletto"
  ArcFitTolerance = 1e-06
  AttachmentSupport = -> [XZ_Plane]
  ExternalGeometry = -> [Sketch]
  FullyConstrained = true
  MakeInternals = false
  MapMode = 5
  Placement = pos=(0,0,0) rot=(1,0,0;1.5708rad)
  sketch-geometry (18):
    g0: LineSegment [constr] StartX=-145.51 StartY=22 StartZ=0 EndX=-157.347 EndY=-14.4293 EndZ=0
    g1: LineSegment [constr] StartX=-157.347 StartY=-14.4293 StartZ=0 EndX=-157.841 EndY=-15.951 EndZ=0
    g2: LineSegment StartX=-161.151 StartY=-13.1932 StartZ=0 EndX=-155.825 EndY=-14.9237 EndZ=0
    g3: LineSegment StartX=-163.167 StartY=-14.2205 StartZ=0 EndX=-164.403 EndY=-18.0247 EndZ=0
    g4: LineSegment StartX=-163.376 StartY=-20.0408 StartZ=0 EndX=-158.05 EndY=-21.7713 EndZ=0
    g5: LineSegment StartX=-158.05 StartY=-21.7713 StartZ=0 EndX=-155.825 EndY=-14.9237 EndZ=0
    g6: LineSegment StartX=-161.645 StartY=-14.7149 StartZ=0 EndX=-157.841 EndY=-15.951 EndZ=0
    g7: LineSegment StartX=-157.841 StartY=-15.951 StartZ=0 EndX=-159.077 EndY=-19.7552 EndZ=0
    g8: LineSegment StartX=-159.077 StartY=-19.7552 StartZ=0 EndX=-162.881 EndY=-18.5191 EndZ=0
    g9: LineSegment StartX=-162.881 StartY=-18.5191 StartZ=0 EndX=-161.645 EndY=-14.7149 EndZ=0
    g10: LineSegment [constr] StartX=-161.645 StartY=-14.7149 StartZ=0 EndX=-161.151 EndY=-13.1932 EndZ=0
    g11: LineSegment [constr] StartX=-159.077 StartY=-19.7552 StartZ=0 EndX=-157.555 EndY=-20.2496 EndZ=0
    g12: LineSegment [constr] StartX=-159.077 StartY=-19.7552 StartZ=0 EndX=-159.572 EndY=-21.2769 EndZ=0
    g13: LineSegment [constr] StartX=-161.645 StartY=-14.7149 StartZ=0 EndX=-163.167 EndY=-14.2205 EndZ=0
    g14: ArcOfCircle CenterX=-161.645 CenterY=-14.7149 CenterZ=0 NormalX=0 NormalY=0 NormalZ=1 AngleXU=0 Radius=1.6 StartAngle=1.25664 EndAngle=2.82743
    g15: GeomPoint [constr] X=-162.673 Y=-12.6988 Z=0
    g16: ArcOfCircle CenterX=-162.881 CenterY=-18.5191 CenterZ=0 NormalX=0 NormalY=0 NormalZ=1 AngleXU=0 Radius=1.6 StartAngle=2.82743 EndAngle=4.39823
    g17: GeomPoint [constr] X=-164.897 Y=-19.5464 Z=0
  constraints (48):
    c: Parallel(g0,g-3)
    c: Distance(g0) = 38.304
    c: Coincident(g0,g-3)
    c: Parallel(g1,g-3)
    c: Distance(g1) = 1.6
    c: Coincident(g1,g0)
    c: Coincident(g5,g4)
    c: Coincident(g5,g2)
    c: Coincident(g7,g6)
    c: Coincident(g8,g7)
    c: Coincident(g9,g8)
    c: Coincident(g9,g6)
    c: Parallel(g7,g-3)
    c: Parallel(g9,g7)
    c: Perpendicular(g6,g7)
    c: Parallel(g6,g8)
    c: Distance(g6) = 4
    c: Distance(g9) = 4
    c: Parallel(g5,g7)
    c: Parallel(g9,g3)
    c: Parallel(g2,g6)
    c: Parallel(g4,g8)
    c: Parallel(g13,g6)
    c: Parallel(g10,g9)
    c: Parallel(g11,g8)
    c: Parallel(g12,g7)
    c: Distance(g10) = 1.6
    c: Distance(g13) = 1.6
    c: Distance(g12) = 1.6
    c: Distance(g11) = 1.6
    c: Coincident(g10,g6)
    c: Coincident(g13,g6)
    c: Coincident(g12,g7)
    c: Coincident(g11,g7)
    c: Distance(g10,g15) = 1.6
    c: Distance(g15,g13) = 1.6
    c: Distance(g4,g12) = 1.6
    c: Distance(g4,g11) = 1.6
    c: PointOnObject(g15,g2)
    c: Tangent(g3,g14) = -1.5708
    c: Tangent(g2,g14) = 1.5708
    c: PointOnObject(g17,g4)
    c: PointOnObject(g17,g3)
    c: Tangent(g4,g16) = -1.5708
    c: Tangent(g3,g16) = -1.5708
    c: Equal(g16,g14)
    c: Coincident(g16,g8)
    c: Coincident(g6,g1)
FEATURE [Part::Extrusion] Extrude007  label="Extrude fermo grilletto"
  Base = -> Sketch011
  Dir = (0,-1,2e-16)
  DirMode = 2
  FaceMakerClass = Part::FaceMakerBullseye
  FaceMakerMode = 3
  LengthFwd = 25.2
  LengthRev = 0
  Solid = true
  Symmetric = true
FEATURE [Sketcher::SketchObject] Sketch012  label="buco oled"
  ArcFitTolerance = 1e-06
  AttachmentSupport = -> [XZ_Plane]
  ExternalGeometry = -> [Sketch]
  FullyConstrained = true
  MakeInternals = false
  MapMode = 5
  Placement = pos=(0,0,0) rot=(1,0,0;1.5708rad)
  sketch-geometry (4):
    g0: LineSegment StartX=-185.747 StartY=58.0965 StartZ=0 EndX=-180.232 EndY=56.0891 EndZ=0
    g1: LineSegment StartX=-185.747 StartY=58.0965 StartZ=0 EndX=-185.747 EndY=67.3588 EndZ=0
    g2: LineSegment StartX=-185.747 StartY=67.3588 StartZ=0 EndX=-180.232 EndY=67.3588 EndZ=0
    g3: LineSegment StartX=-180.232 StartY=67.3588 StartZ=0 EndX=-180.232 EndY=56.0891 EndZ=0
  constraints (10):
    c: Coincident(g1,g0)
    c: Coincident(g2,g1)
    c: Coincident(g3,g2)
    c: Coincident(g3,g0)
    c: Parallel(g1,g-5)
    c: Perpendicular(g-3,g0)
    c: Parallel(g2,g-6)
    c: Parallel(g3,g-4)
    c: Coincident(g0,g-5)
    c: Coincident(g2,g-6)
FEATURE [Part::Extrusion] Extrude008  label="Extrude buco oled"
  Base = -> Sketch012
  Dir = (0,-1,2e-16)
  DirMode = 2
  FaceMakerClass = Part::FaceMakerBullseye
  FaceMakerMode = 3
  LengthFwd = 12.8
  LengthRev = 0
  Solid = true
  Symmetric = true
FEATURE [Sketcher::SketchObject] Sketch013  label="buco pompa"
  ArcFitTolerance = 1e-06
  AttachmentSupport = -> [XZ_Plane]
  ExternalGeometry = -> [Sketch]
  FullyConstrained = true
  MakeInternals = false
  MapMode = 5
  Placement = pos=(0,0,0) rot=(1,0,0;1.5708rad)
  sketch-geometry (8):
    g0: LineSegment StartX=-82.8 StartY=-10.4 StartZ=0 EndX=-82.8 EndY=-9.6 EndZ=0
    g1: LineSegment StartX=-82.8 StartY=-9.6 StartZ=0 EndX=-67.9 EndY=-9.6 EndZ=0
    g2: LineSegment StartX=-67.9 StartY=-9.6 StartZ=0 EndX=-67.9 EndY=6 EndZ=0
    g3: LineSegment StartX=-67.9 StartY=6 StartZ=0 EndX=-65.9 EndY=6 EndZ=0
    g4: LineSegment StartX=-65.9 StartY=6 StartZ=0 EndX=-65.9 EndY=-1.7 EndZ=0
    g5: LineSegment StartX=-65.9 StartY=-1.7 StartZ=0 EndX=-57.2 EndY=-1.7 EndZ=0
    g6: LineSegment StartX=-57.2 StartY=-1.7 StartZ=0 EndX=-57.2 EndY=-10.4 EndZ=0
    g7: LineSegment StartX=-57.2 StartY=-10.4 StartZ=0 EndX=-82.8 EndY=-10.4 EndZ=0
  constraints (22):
    c: Vertical(g0)
    c: Coincident(g1,g0)
    c: Horizontal(g1)
    c: Coincident(g2,g1)
    c: Vertical(g2)
    c: Coincident(g3,g2)
    c: Horizontal(g3)
    c: Coincident(g4,g3)
    c: Vertical(g4)
    c: Coincident(g5,g4)
    c: Horizontal(g5)
    c: Coincident(g6,g5)
    c: Vertical(g6)
    c: Coincident(g7,g6)
    c: Coincident(g7,g0)
    c: DistanceY(g0,g0) = 0.8
    c: DistanceY(g6,g6) = 8.7
    c: DistanceX(g1,g1) = 14.9
    c: DistanceX(g3,g3) = 2
    c: Coincident(g0,g-4)
    c: DistanceY(g2,g-6) = 0
    c: Coincident(g6,g-5)
FEATURE [Part::Extrusion] Extrude009  label="Extrude buco pompa"
  Base = -> Sketch013
  Dir = (0,-1,2e-16)
  DirMode = 2
  FaceMakerClass = Part::FaceMakerBullseye
  FaceMakerMode = 3
  LengthFwd = 13.2
  LengthRev = 0
  Solid = true
  Symmetric = true
FEATURE [Sketcher::SketchObject] Sketch014  label="buco frontale"
  ArcFitTolerance = 1e-06
  AttachmentSupport = -> [XZ_Plane]
  ExternalGeometry = -> [Sketch]
  FullyConstrained = true
  MakeInternals = false
  MapMode = 5
  Placement = pos=(0,0,0) rot=(1,0,0;1.5708rad)
  sketch-geometry (10):
    g0: LineSegment StartX=0 StartY=0 StartZ=0 EndX=0 EndY=24.671 EndZ=0
    g1: LineSegment StartX=0 StartY=24.671 StartZ=0 EndX=-4 EndY=24.671 EndZ=0
    g2: LineSegment StartX=-4 StartY=24.671 StartZ=0 EndX=-4 EndY=16 EndZ=0
    g3: LineSegment StartX=-4 StartY=16 StartZ=0 EndX=-2.4 EndY=16 EndZ=0
    g4: LineSegment StartX=-2.4 StartY=16 StartZ=0 EndX=-2.4 EndY=10 EndZ=0
    g5: LineSegment StartX=-2.4 StartY=10 StartZ=0 EndX=-12 EndY=10 EndZ=0
    g6: LineSegment StartX=-12 StartY=10 StartZ=0 EndX=-12 EndY=6 EndZ=0
    g7: LineSegment StartX=-12 StartY=6 StartZ=0 EndX=-2.4 EndY=6 EndZ=0
    g8: LineSegment StartX=-2.4 StartY=6 StartZ=0 EndX=-2.4 EndY=0 EndZ=0
    g9: LineSegment StartX=-2.4 StartY=0 StartZ=0 EndX=0 EndY=0 EndZ=0
  constraints (29):
    c: Vertical(g0)
    c: Coincident(g1,g0)
    c: Horizontal(g1)
    c: Coincident(g2,g1)
    c: Vertical(g2)
    c: Coincident(g3,g2)
    c: Horizontal(g3)
    c: Coincident(g4,g3)
    c: Vertical(g4)
    c: Coincident(g5,g4)
    c: Horizontal(g5)
    c: Coincident(g6,g5)
    c: Vertical(g6)
    c: Coincident(g7,g6)
    c: Coincident(g8,g7)
    c: Vertical(g8)
    c: Coincident(g9,g8)
    c: Coincident(g9,g0)
    c: Horizontal(g9)
    c: DistanceY(g0,g0) = 24.671
    c: Horizontal(g7)
    c: DistanceY(g6,g6) = 4
    c: DistanceY(g4,g4) = 6
    c: DistanceX(g9,g9) = 2.4
    c: Coincident(g0,g-1)
    c: DistanceY(g-3,g7) = 0
    c: DistanceX(g8,g4) = 0
    c: DistanceX(g-3,g1) = 0
    c: DistanceX(g6,g-3) = 8
FEATURE [Part::Extrusion] Extrude010  label="Extrude buco frontale"
  Base = -> Sketch014
  Dir = (0,-1,2e-16)
  DirMode = 2
  FaceMakerClass = Part::FaceMakerBullseye
  FaceMakerMode = 3
  LengthFwd = 11.2
  LengthRev = 0
  Solid = true
  Symmetric = true
FEATURE [Sketcher::SketchObject] Sketch015  label="guida rail"
  ArcFitTolerance = 1e-06
  AttachmentSupport = -> [XZ_Plane]
  ExternalGeometry = -> [Sketch]
  FullyConstrained = true
  MakeInternals = false
  MapMode = 5
  Placement = pos=(0,0,0) rot=(1,0,0;1.5708rad)
  sketch-geometry (4):
    g0: LineSegment StartX=-100.8 StartY=43.2 StartZ=0 EndX=-44.6 EndY=43.2 EndZ=0
    g1: LineSegment StartX=-44.6 StartY=43.2 StartZ=0 EndX=-44.6 EndY=41.2 EndZ=0
    g2: LineSegment StartX=-44.6 StartY=41.2 StartZ=0 EndX=-100.8 EndY=41.2 EndZ=0
    g3: LineSegment StartX=-100.8 StartY=41.2 StartZ=0 EndX=-100.8 EndY=43.2 EndZ=0
  constraints (9):
    c: Horizontal(g0)
    c: Coincident(g1,g0)
    c: Coincident(g2,g1)
    c: Coincident(g3,g2)
    c: Coincident(g3,g0)
    c: Vertical(g3)
    c: Coincident(g2,g-3)
    c: Coincident(g1,g-3)
    c: Coincident(g0,g-4)
FEATURE [Part::Extrusion] Extrude011  label="Extrude guida rail"
  Base = -> Sketch015
  Dir = (0,-1,2e-16)
  DirMode = 2
  FaceMakerClass = Part::FaceMakerBullseye
  FaceMakerMode = 3
  LengthFwd = 9
  LengthRev = 0
  Solid = true
  Symmetric = true
FEATURE [Sketcher::SketchObject] Sketch016  label="guide per coperture laterali"
  ArcFitTolerance = 1e-06
  AttachmentSupport = -> [XZ_Plane]
  ExternalGeometry = -> [Sketch]
  FullyConstrained = true
  MakeInternals = false
  MapMode = 5
  Placement = pos=(0,0,0) rot=(1,0,0;1.5708rad)
  sketch-geometry (14):
    g0: Circle CenterX=-5.6 CenterY=7.6 CenterZ=0 NormalX=0 NormalY=0 NormalZ=1 AngleXU=0 Radius=1.6
    g1: Circle CenterX=-5.6 CenterY=7.6 CenterZ=0 NormalX=0 NormalY=0 NormalZ=1 AngleXU=0 Radius=4
    g2: Circle CenterX=-5.6 CenterY=34.8 CenterZ=0 NormalX=0 NormalY=0 NormalZ=1 AngleXU=0 Radius=1.6
    g3: Circle CenterX=-5.6 CenterY=34.8 CenterZ=0 NormalX=0 NormalY=0 NormalZ=1 AngleXU=0 Radius=4
    g4: Circle CenterX=-184.08 CenterY=34.8 CenterZ=0 NormalX=0 NormalY=0 NormalZ=1 AngleXU=0 Radius=1.6
    g5: Circle CenterX=-184.08 CenterY=34.8 CenterZ=0 NormalX=0 NormalY=0 NormalZ=1 AngleXU=0 Radius=4
    g6: Circle CenterX=-179.305 CenterY=-76.8316 CenterZ=0 NormalX=0 NormalY=0 NormalZ=1 AngleXU=0 Radius=1.6
    g7: Circle CenterX=-179.305 CenterY=-76.8316 CenterZ=0 NormalX=0 NormalY=0 NormalZ=1 AngleXU=0 Radius=4
    g8: Circle CenterX=-213.443 CenterY=-76.8316 CenterZ=0 NormalX=0 NormalY=0 NormalZ=1 AngleXU=0 Radius=1.6
    g9: Circle CenterX=-213.443 CenterY=-76.8316 CenterZ=0 NormalX=0 NormalY=0 NormalZ=1 AngleXU=0 Radius=4
    g10: Circle CenterX=-78.51 CenterY=7.6 CenterZ=0 NormalX=0 NormalY=0 NormalZ=1 AngleXU=0 Radius=1.6
    g11: Circle CenterX=-78.51 CenterY=7.6 CenterZ=0 NormalX=0 NormalY=0 NormalZ=1 AngleXU=0 Radius=4
    g12: Circle CenterX=-78.51 CenterY=34.8 CenterZ=0 NormalX=0 NormalY=0 NormalZ=1 AngleXU=0 Radius=1.6
    g13: Circle CenterX=-78.51 CenterY=34.8 CenterZ=0 NormalX=0 NormalY=0 NormalZ=1 AngleXU=0 Radius=4
  constraints (35):
    c: Diameter(g0) = 3.2
    c: Diameter(g1) = 8
    c: Coincident(g0,g1)
    c: Diameter(g2) = 3.2
    c: Diameter(g3) = 8
    c: Coincident(g3,g2)
    c: Tangent(g2,g-7)
    c: Diameter(g4) = 3.2
    c: Diameter(g5) = 8
    c: Coincident(g5,g4)
    c: Tangent(g4,g-7)
    c: Tangent(g4,g-8)
    c: Diameter(g6) = 3.2
    c: Diameter(g7) = 8
    c: Coincident(g7,g6)
    c: Tangent(g6,g-9)
    c: Tangent(g6,g-10)
    c: Diameter(g8) = 3.2
    c: Diameter(g9) = 8
    c: Coincident(g9,g8)
    c: Tangent(g8,g-10)
    c: Tangent(g8,g-11)
    c: Diameter(g10) = 3.2
    c: Diameter(g11) = 8
    c: Diameter(g12) = 3.2
    c: Diameter(g13) = 8
    c: Coincident(g12,g13)
    c: Coincident(g10,g11)
    c: Tangent(g12,g-7)
    c: DistanceX(g12,g10) = 0
    c: Tangent(g2,g-6)
    c: Tangent(g0,g-6)
    c: Tangent(g0,g-3)
    c: Tangent(g10,g-3)
    c: Tangent(g10,g-4)
FEATURE [Part::Extrusion] Extrude012  label="extrude guide per coperture laterali"
  Base = -> Sketch016
  Dir = (0,-1,2e-16)
  DirMode = 2
  FaceMakerClass = Part::FaceMakerBullseye
  FaceMakerMode = 3
  LengthFwd = 25.2
  LengthRev = 0
  Solid = true
  Symmetric = true
FEATURE [Sketcher::SketchObject] Sketch017  label="supporto CAM"
  ArcFitTolerance = 1e-06
  AttachmentSupport = -> [XZ_Plane]
  ExternalGeometry = -> [Sketch]
  FullyConstrained = true
  MakeInternals = false
  MapMode = 5
  Placement = pos=(0,0,0) rot=(1,0,0;1.5708rad)
  sketch-geometry (6):
    g0: LineSegment StartX=-2.4 StartY=48 StartZ=0 EndX=-2.4 EndY=41.2 EndZ=0
    g1: LineSegment StartX=-2.4 StartY=48 StartZ=0 EndX=-34 EndY=48 EndZ=0
    g2: LineSegment StartX=-34 StartY=48 StartZ=0 EndX=-34 EndY=46.72 EndZ=0
    g3: LineSegment StartX=-34 StartY=46.72 StartZ=0 EndX=-36 EndY=46.72 EndZ=0
    g4: LineSegment StartX=-36 StartY=46.72 StartZ=0 EndX=-36 EndY=41.2 EndZ=0
    g5: LineSegment StartX=-36 StartY=41.2 StartZ=0 EndX=-2.4 EndY=41.2 EndZ=0
  constraints (15):
    c: Coincident(g1,g0)
    c: Horizontal(g1)
    c: Coincident(g2,g1)
    c: Vertical(g2)
    c: Coincident(g3,g2)
    c: Horizontal(g3)
    c: Coincident(g4,g3)
    c: Coincident(g5,g4)
    c: DistanceX(g1,g0) = 31.6
    c: Coincident(g5,g0)
    c: Vertical(g4)
    c: DistanceY(g2,g1) = 1.28
    c: Coincident(g0,g-3)
    c: Coincident(g0,g-3)
    c: Coincident(g4,g-4)
FEATURE [Part::Extrusion] Extrude013  label="Extrude supporto CAM"
  Base = -> Sketch017
  Dir = (0,-1,2e-16)
  DirMode = 2
  FaceMakerClass = Part::FaceMakerBullseye
  FaceMakerMode = 3
  LengthFwd = 17.8
  LengthRev = 0
  Solid = true
  Symmetric = true
FEATURE [Sketcher::SketchObject] Sketch018  label="Scavo CAM"
  ArcFitTolerance = 1e-06
  AttachmentSupport = -> [YZ_Plane]
  ExternalGeometry = -> [Sketch]
  FullyConstrained = true
  MakeInternals = false
  MapMode = 5
  Placement = pos=(0,0,0) rot=(0.57735,0.57735,0.57735;2.0944rad)
  sketch-geometry (4):
    g0: LineSegment StartX=-7.73 StartY=48 StartZ=0 EndX=7.73 EndY=48 EndZ=0
    g1: LineSegment [constr] StartX=1.07e-14 StartY=48 StartZ=0 EndX=0 EndY=43.5155 EndZ=0
    g2: ArcOfCircle CenterX=9e-15 CenterY=52.42 CenterZ=0 NormalX=0 NormalY=0 NormalZ=1 AngleXU=0 Radius=8.90445 StartAngle=3.66102 EndAngle=5.76376
    g3: Circle [constr] CenterX=9e-15 CenterY=52.42 CenterZ=0 NormalX=0 NormalY=0 NormalZ=1 AngleXU=0 Radius=8.9
  constraints (13):
    c: Horizontal(g0)
    c: DistanceY(g-3,g0) = 0
    c: DistanceX(g0,g0) = 15.46
    c: DistanceX(g0,g-3) = 7.73
    c: DistanceX(g-3) = 0
    c: Coincident(g1,g-3)
    c: PointOnObject(g1,g-2)
    c: Coincident(g2,g0)
    c: Coincident(g2,g0)
    c: PointOnObject(g1,g2)
    c: Diameter(g3) = 17.8
    c: DistanceY(g1,g3) = 4.42
    c: Coincident(g2,g3)
FEATURE [Part::Extrusion] Extrude014  label="Extrude Scavo CAM"
  Base = -> Sketch018
  Dir = (1,0,0)
  DirMode = 2
  FaceMakerClass = Part::FaceMakerBullseye
  FaceMakerMode = 3
  LengthFwd = -34
  LengthRev = 0
  Solid = true
  Symmetric = false
FEATURE [Sketcher::SketchObject] Sketch019  label="scavo rumble"
  ArcFitTolerance = 1e-06
  AttachmentSupport = -> [XZ_Plane]
  ExternalGeometry = -> [Sketch]
  FullyConstrained = true
  MakeInternals = false
  MapMode = 5
  Placement = pos=(0,0,0) rot=(1,0,0;1.5708rad)
  sketch-geometry (6):
    g0: LineSegment StartX=-164.575 StartY=-24.3786 StartZ=0 EndX=-159.439 EndY=-26.0473 EndZ=0
    g1: LineSegment StartX=-159.439 StartY=-26.0473 StartZ=0 EndX=-166.547 EndY=-47.9216 EndZ=0
    g2: LineSegment StartX=-166.547 StartY=-47.9216 StartZ=0 EndX=-171.682 EndY=-46.2529 EndZ=0
    g3: LineSegment StartX=-171.682 StartY=-46.2529 StartZ=0 EndX=-164.575 EndY=-24.3786 EndZ=0
    g4: LineSegment [constr] StartX=-145.51 StartY=22 StartZ=0 EndX=-160.961 EndY=-25.5528 EndZ=0
    g5: LineSegment [constr] StartX=-159.439 StartY=-26.0473 StartZ=0 EndX=-160.961 EndY=-25.5528 EndZ=0
  constraints (17):
    c: Coincident(g1,g0)
    c: Coincident(g2,g1)
    c: Coincident(g3,g2)
    c: Coincident(g3,g0)
    c: Parallel(g3,g-3)
    c: Parallel(g3,g1)
    c: Perpendicular(g3,g0)
    c: Perpendicular(g2,g3)
    c: Distance(g2,g0) = 23
    c: Parallel(g4,g-3)
    c: Distance(g4) = 50
    c: Coincident(g4,g-3)
    c: Parallel(g5,g0)
    c: Distance(g5) = 1.6
    c: Coincident(g5,g0)
    c: Distance(g5,g0) = 3.8
    c: Coincident(g5,g4)
FEATURE [Part::Extrusion] Extrude015  label="scavo rumble001"
  Base = -> Sketch019
  Dir = (0,-1,2e-16)
  DirMode = 2
  FaceMakerClass = Part::FaceMakerBullseye
  FaceMakerMode = 3
  LengthFwd = 21
  LengthRev = 0
  Solid = true
  Symmetric = true
FEATURE [Sketcher::SketchObject] Sketch020  label="fermo rumble"
  ArcFitTolerance = 1e-06
  AttachmentSupport = -> [XZ_Plane]
  ExternalGeometry = -> [Sketch019,Sketch]
  FullyConstrained = true
  MakeInternals = false
  MapMode = 5
  Placement = pos=(0,0,0) rot=(1,0,0;1.5708rad)
  sketch-geometry (16):
    g0: LineSegment [constr] StartX=-166.709 StartY=-43.2425 StartZ=0 EndX=-168.068 EndY=-47.4271 EndZ=0
    g1: LineSegment [constr] StartX=-168.068 StartY=-47.4271 StartZ=0 EndX=-166.547 EndY=-47.9216 EndZ=0
    g2: LineSegment StartX=-168.121 StartY=-40.4703 StartZ=0 EndX=-166.029 EndY=-41.1502 EndZ=0
    g3: LineSegment StartX=-166.029 StartY=-41.1502 StartZ=0 EndX=-166.709 EndY=-43.2425 EndZ=0
    g4: LineSegment StartX=-166.709 StartY=-43.2425 StartZ=0 EndX=-168.801 EndY=-42.5626 EndZ=0
    g5: LineSegment StartX=-168.801 StartY=-42.5626 StartZ=0 EndX=-168.121 EndY=-40.4703 EndZ=0
    g6: LineSegment StartX=-167.627 StartY=-38.9486 StartZ=0 EndX=-164.203 EndY=-40.0611 EndZ=0
    g7: LineSegment StartX=-164.203 StartY=-40.0611 StartZ=0 EndX=-165.81 EndY=-45.0066 EndZ=0
    g8: LineSegment StartX=-165.81 StartY=-45.0066 StartZ=0 EndX=-169.234 EndY=-43.8941 EndZ=0
    g9: LineSegment StartX=-170.261 StartY=-41.878 StartZ=0 EndX=-169.643 EndY=-39.9759 EndZ=0
    g10: LineSegment [constr] StartX=-169.643 StartY=-39.9759 StartZ=0 EndX=-169.148 EndY=-38.4542 EndZ=0
    g11: LineSegment [constr] StartX=-169.148 StartY=-38.4542 StartZ=0 EndX=-167.627 EndY=-38.9486 EndZ=0
    g12: ArcOfCircle CenterX=-168.739 CenterY=-42.3724 CenterZ=0 NormalX=0 NormalY=0 NormalZ=1 AngleXU=0 Radius=1.6 StartAngle=2.82743 EndAngle=4.39823
    g13: GeomPoint [constr] X=-170.755 Y=-43.3997 Z=0
    g14: ArcOfCircle CenterX=-168.121 CenterY=-40.4703 CenterZ=0 NormalX=0 NormalY=0 NormalZ=1 AngleXU=0 Radius=1.6 StartAngle=1.25664 EndAngle=2.82743
    g15: GeomPoint [constr] X=-169.148 Y=-38.4542 Z=0
  constraints (42):
    c: Parallel(g0,g-4)
    c: Distance(g0) = 4.4
    c: Coincident(g1,g0)
    c: Perpendicular(g0,g1)
    c: Distance(g1) = 1.6
    c: Coincident(g1,g-5)
    c: Coincident(g3,g2)
    c: Coincident(g4,g3)
    c: Coincident(g5,g4)
    c: Coincident(g5,g2)
    c: Parallel(g3,g-4)
    c: Parallel(g3,g5)
    c: Perpendicular(g2,g3)
    c: Parallel(g4,g2)
    c: Distance(g2) = 2.2
    c: Distance(g3) = 2.2
    c: Coincident(g7,g6)
    c: Coincident(g8,g7)
    c: Parallel(g7,g-4)
    c: Parallel(g7,g9)
    c: Perpendicular(g6,g7)
    c: Parallel(g6,g8)
    c: Distance(g6,g15) = 5.2
    c: Distance(g7) = 5.2
    c: Coincident(g11,g10)
    c: Parallel(g10,g9)
    c: Parallel(g11,g6)
    c: Distance(g10) = 1.6
    c: Distance(g11) = 1.6
    c: Coincident(g10,g15)
    c: Distance(g11,g2) = 1.6
    c: Distance(g2,g10) = 1.6
    c: PointOnObject(g13,g8)
    c: PointOnObject(g13,g9)
    c: Tangent(g8,g12) = 1.5708
    c: Tangent(g9,g12) = 1.5708
    c: PointOnObject(g15,g9)
    c: Tangent(g6,g14) = 1.5708
    c: Tangent(g9,g14) = 1.5708
    c: Equal(g12,g14)
    c: Coincident(g6,g11)
    c: Coincident(g3,g0)
FEATURE [Part::Extrusion] Extrude016  label="Extrude fermo rumble"
  Base = -> Sketch020
  Dir = (0,-1,2e-16)
  DirMode = 2
  FaceMakerClass = Part::FaceMakerBullseye
  FaceMakerMode = 3
  LengthFwd = 25.2
  LengthRev = 0
  Solid = true
  Symmetric = true
FEATURE [Sketcher::SketchObject] Sketch021  label="perno fermo rumble001"
  ArcFitTolerance = 1e-06
  AttachmentSupport = -> [XZ_Plane001]
  FullyConstrained = true
  MakeInternals = false
  MapMode = 5
  Placement = pos=(0,0,0) rot=(1,0,0;1.5708rad)
  sketch-geometry (16):
    g0: LineSegment StartX=0 StartY=0.45 StartZ=0 EndX=0 EndY=1.55 EndZ=0
    g1: LineSegment StartX=0.45 StartY=2 StartZ=0 EndX=1.55 EndY=2 EndZ=0
    g2: LineSegment StartX=2 StartY=1.55 StartZ=0 EndX=2 EndY=0.45 EndZ=0
    g3: LineSegment StartX=1.55 StartY=0 StartZ=0 EndX=0.45 EndY=0 EndZ=0
    g4: ArcOfCircle [constr] CenterX=0.45 CenterY=1.55 CenterZ=0 NormalX=0 NormalY=0 NormalZ=1 AngleXU=0 Radius=0.45 StartAngle=1.5708 EndAngle=3.14159
    g5: GeomPoint [constr] X=0 Y=2 Z=0
    g6: LineSegment StartX=0.45 StartY=2 StartZ=0 EndX=0 EndY=1.55 EndZ=0
    g7: ArcOfCircle [constr] CenterX=1.55 CenterY=1.55 CenterZ=0 NormalX=0 NormalY=0 NormalZ=1 AngleXU=0 Radius=0.45 StartAngle=0 EndAngle=1.5708
    g8: GeomPoint [constr] X=2 Y=2 Z=0
    g9: LineSegment StartX=2 StartY=1.55 StartZ=0 EndX=1.55 EndY=2 EndZ=0
    g10: ArcOfCircle [constr] CenterX=1.55 CenterY=0.45 CenterZ=0 NormalX=0 NormalY=0 NormalZ=1 AngleXU=0 Radius=0.45 StartAngle=4.71239 EndAngle=6.28319
    g11: GeomPoint [constr] X=2 Y=0 Z=0
    g12: LineSegment StartX=1.55 StartY=0 StartZ=0 EndX=2 EndY=0.45 EndZ=0
    g13: ArcOfCircle [constr] CenterX=0.45 CenterY=0.45 CenterZ=0 NormalX=0 NormalY=0 NormalZ=1 AngleXU=0 Radius=0.45 StartAngle=3.14159 EndAngle=4.71239
    g14: GeomPoint [constr] X=0 Y=0 Z=0
    g15: LineSegment StartX=0 StartY=0.45 StartZ=0 EndX=0.45 EndY=0 EndZ=0
  constraints (35):
    c: Coincident(g14,g-1)
    c: PointOnObject(g5,g-2)
    c: Horizontal(g1)
    c: Vertical(g2)
    c: Horizontal(g3)
    c: DistanceX(g5,g8) = 2
    c: DistanceY(g11,g8) = 2
    c: PointOnObject(g5,g0)
    c: PointOnObject(g5,g1)
    c: Tangent(g0,g4) = 1.5708
    c: Tangent(g1,g4) = 1.5708
    c: Coincident(g6,g0)
    c: Coincident(g6,g1)
    c: PointOnObject(g8,g2)
    c: PointOnObject(g8,g1)
    c: Tangent(g2,g7) = 1.5708
    c: Tangent(g1,g7) = 1.5708
    c: Coincident(g9,g2)
    c: Coincident(g9,g1)
    c: PointOnObject(g11,g2)
    c: PointOnObject(g11,g3)
    c: Tangent(g2,g10) = 1.5708
    c: Tangent(g3,g10) = 1.5708
    c: Coincident(g12,g2)
    c: Coincident(g12,g3)
    c: PointOnObject(g14,g0)
    c: PointOnObject(g14,g3)
    c: Tangent(g0,g13) = 1.5708
    c: Tangent(g3,g13) = 1.5708
    c: Coincident(g15,g0)
    c: Coincident(g15,g3)
    c: Equal(g6,g9)
    c: Equal(g9,g12)
    c: Equal(g12,g15)
    c: DistanceX(g14,g3) = 0.45
FEATURE [Part::Extrusion] Extrude017  label="Extrude perno fermo rumble"
  Base = -> Sketch021
  Dir = (0,-1,2e-16)
  DirMode = 2
  FaceMakerClass = Part::FaceMakerBullseye
  FaceMakerMode = 3
  LengthFwd = 25.2
  LengthRev = 0
  Solid = true
  Symmetric = true
FEATURE [Sketcher::SketchObject] Sketch022  label="fori per M3x5(OD)x6(L)"
  ArcFitTolerance = 1e-06
  AttachmentSupport = -> [XZ_Plane]
  ExternalGeometry = -> [Sketch016]
  FullyConstrained = true
  MakeInternals = false
  MapMode = 5
  Placement = pos=(0,0,0) rot=(1,0,0;1.5708rad)
  sketch-geometry (7):
    g0: Circle CenterX=-5.6 CenterY=34.8 CenterZ=0 NormalX=0 NormalY=0 NormalZ=1 AngleXU=0 Radius=2.5
    g1: Circle CenterX=-5.6 CenterY=7.6 CenterZ=0 NormalX=0 NormalY=0 NormalZ=1 AngleXU=0 Radius=2.5
    g2: Circle CenterX=-78.51 CenterY=34.8 CenterZ=0 NormalX=0 NormalY=0 NormalZ=1 AngleXU=0 Radius=2.5
    g3: Circle CenterX=-78.51 CenterY=7.6 CenterZ=0 NormalX=0 NormalY=0 NormalZ=1 AngleXU=0 Radius=2.5
    g4: Circle CenterX=-184.08 CenterY=34.8 CenterZ=0 NormalX=0 NormalY=0 NormalZ=1 AngleXU=0 Radius=2.5
    g5: Circle CenterX=-179.305 CenterY=-76.8316 CenterZ=0 NormalX=0 NormalY=0 NormalZ=1 AngleXU=0 Radius=2.5
    g6: Circle CenterX=-213.443 CenterY=-76.8316 CenterZ=0 NormalX=0 NormalY=0 NormalZ=1 AngleXU=0 Radius=2.5
  constraints (14):
    c: Diameter(g0) = 5
    c: Diameter(g1) = 5
    c: Diameter(g2) = 5
    c: Diameter(g3) = 5
    c: Diameter(g4) = 5
    c: Diameter(g5) = 5
    c: Diameter(g6) = 5
    c: Coincident(g0,g-8)
    c: Coincident(g1,g-9)
    c: Coincident(g2,g-6)
    c: Coincident(g3,g-7)
    c: Coincident(g4,g-5)
    c: Coincident(g5,g-4)
    c: Coincident(g6,g-3)
FEATURE [Part::Extrusion] Extrude018  label="Extrude fori M3x5x6 - dx"
  Base = -> Sketch022
  Dir = (0,-1,2e-16)
  DirMode = 2
  FaceMakerClass = Part::FaceMakerBullseye
  FaceMakerMode = 3
  LengthFwd = 6.2
  LengthRev = 0
  Placement = pos=(0,-9.5,0) rot=(0,0,1;0rad)
  Solid = true
  Symmetric = true
FEATURE [Part::Extrusion] Extrude019  label="Extrude fori M3x5x6 - sx"
  Base = -> Sketch022
  Dir = (0,-1,2e-16)
  DirMode = 2
  FaceMakerClass = Part::FaceMakerBullseye
  FaceMakerMode = 3
  LengthFwd = 6.2
  LengthRev = 0
  Placement = pos=(0,9.5,0) rot=(0,0,1;0rad)
  Solid = true
  Symmetric = true
FEATURE [Sketcher::SketchObject] Sketch023  label="foro anteriore M3x5x6"
  ArcFitTolerance = 1e-06
  AttachmentSupport = -> [YZ_Plane]
  FullyConstrained = true
  MakeInternals = false
  MapMode = 5
  Placement = pos=(0,0,0) rot=(0.57735,0.57735,0.57735;2.0944rad)
  sketch-geometry (2):
    g0: LineSegment [constr] StartX=0 StartY=0 StartZ=0 EndX=0 EndY=38.6 EndZ=0
    g1: Circle CenterX=0 CenterY=38.6 CenterZ=0 NormalX=0 NormalY=0 NormalZ=1 AngleXU=0 Radius=2.5
  constraints (5):
    c: Coincident(g0,g-1)
    c: PointOnObject(g0,g-2)
    c: DistanceY(g0,g0) = 38.6
    c: Diameter(g1) = 5
    c: Coincident(g1,g0)
FEATURE [Part::Extrusion] Extrude020  label="Extrude foro anteriore M3x5x6"
  Base = -> Sketch023
  Dir = (1,0,0)
  DirMode = 2
  FaceMakerClass = Part::FaceMakerBullseye
  FaceMakerMode = 3
  LengthFwd = -6.2
  LengthRev = 0
  Solid = true
  Symmetric = false
FEATURE [Sketcher::SketchObject] Sketch024  label="fori per viti frontale"
  ArcFitTolerance = 1e-06
  AttachmentSupport = -> [YZ_Plane]
  FullyConstrained = true
  MakeInternals = false
  MapMode = 5
  Placement = pos=(0,0,0) rot=(0.57735,0.57735,0.57735;2.0944rad)
  sketch-geometry (9):
    g0: LineSegment [constr] StartX=-10.3 StartY=30.721 StartZ=0 EndX=10.3 EndY=30.721 EndZ=0
    g1: LineSegment [constr] StartX=10.3 StartY=30.721 StartZ=0 EndX=10.3 EndY=10.121 EndZ=0
    g2: LineSegment [constr] StartX=10.3 StartY=10.121 StartZ=0 EndX=-10.3 EndY=10.121 EndZ=0
    g3: LineSegment [constr] StartX=-10.3 StartY=10.121 StartZ=0 EndX=-10.3 EndY=30.721 EndZ=0
    g4: LineSegment [constr] StartX=0 StartY=0 StartZ=0 EndX=0 EndY=10.121 EndZ=0
    g5: Circle CenterX=-10.3 CenterY=30.721 CenterZ=0 NormalX=0 NormalY=0 NormalZ=1 AngleXU=0 Radius=2
    g6: Circle CenterX=10.3 CenterY=30.721 CenterZ=0 NormalX=0 NormalY=0 NormalZ=1 AngleXU=0 Radius=2
    g7: Circle CenterX=-10.3 CenterY=10.121 CenterZ=0 NormalX=0 NormalY=0 NormalZ=1 AngleXU=0 Radius=2
    g8: Circle CenterX=10.3 CenterY=10.121 CenterZ=0 NormalX=0 NormalY=0 NormalZ=1 AngleXU=0 Radius=2
  constraints (22):
    c: Horizontal(g0)
    c: Coincident(g1,g0)
    c: Vertical(g1)
    c: Coincident(g2,g1)
    c: Horizontal(g2)
    c: Coincident(g3,g2)
    c: Coincident(g3,g0)
    c: Vertical(g3)
    c: DistanceX(g0,g0) = 20.6
    c: DistanceY(g3,g3) = 20.6
    c: Coincident(g4,g-1)
    c: PointOnObject(g4,g-2)
    c: DistanceY(g4,g4) = 10.121
    c: Symmetric(g2,g2,g4)
    c: Diameter(g5) = 4
    c: Diameter(g6) = 4
    c: Diameter(g7) = 4
    c: Diameter(g8) = 4
    c: Coincident(g5,g0)
    c: Coincident(g6,g0)
    c: Coincident(g7,g2)
    c: Coincident(g8,g1)
FEATURE [Part::Extrusion] Extrude021  label="Extrude fori per viti frontale"
  Base = -> Sketch024
  Dir = (1,0,0)
  DirMode = 2
  FaceMakerClass = Part::FaceMakerBullseye
  FaceMakerMode = 3
  LengthFwd = -2.4
  LengthRev = 0
  Solid = true
  Symmetric = false
FEATURE [Sketcher::SketchObject] Sketch025  label="foro per filo CAM"
  ArcFitTolerance = 1e-06
  AttachmentSupport = -> [XZ_Plane]
  ExternalGeometry = -> [Sketch]
  FullyConstrained = true
  MakeInternals = false
  MapMode = 5
  Placement = pos=(0,0,0) rot=(1,0,0;1.5708rad)
  sketch-geometry (4):
    g0: LineSegment StartX=-44.6 StartY=41.2 StartZ=0 EndX=-44.6 EndY=36.4 EndZ=0
    g1: LineSegment StartX=-44.6 StartY=36.4 StartZ=0 EndX=-54.6 EndY=36.4 EndZ=0
    g2: LineSegment StartX=-54.6 StartY=36.4 StartZ=0 EndX=-50.4 EndY=41.2 EndZ=0
    g3: LineSegment StartX=-50.4 StartY=41.2 StartZ=0 EndX=-44.6 EndY=41.2 EndZ=0
  constraints (11):
    c: Vertical(g0)
    c: Coincident(g1,g0)
    c: Horizontal(g1)
    c: Coincident(g2,g1)
    c: Coincident(g3,g2)
    c: Coincident(g3,g0)
    c: Horizontal(g3)
    c: Coincident(g0,g-3)
    c: DistanceY(g0,g-4) = 0
    c: DistanceX(g3,g3) = 5.8
    c: DistanceX(g1,g1) = 10
FEATURE [Part::Extrusion] Extrude022  label="Extrude foro per filo CAM dx"
  Base = -> Sketch025
  Dir = (0,-1,2e-16)
  DirMode = 2
  FaceMakerClass = Part::FaceMakerBullseye
  FaceMakerMode = 3
  LengthFwd = 4.9
  LengthRev = 0
  Placement = pos=(0,6.95,0) rot=(0,0,1;0rad)
  Solid = true
  Symmetric = true
FEATURE [Part::Extrusion] Extrude023  label="Extrude foro per filo CAM sx"
  Base = -> Sketch025
  Dir = (0,-1,2e-16)
  DirMode = 2
  FaceMakerClass = Part::FaceMakerBullseye
  FaceMakerMode = 3
  LengthFwd = 4.9
  LengthRev = 0
  Placement = pos=(0,-6.95,0) rot=(0,0,1;0rad)
  Solid = true
  Symmetric = true
FEATURE [Sketcher::SketchObject] Sketch026  label="foro sotto anteriore M3x5x6"
  ArcFitTolerance = 1e-06
  AttachmentSupport = -> [XY_Plane]
  FullyConstrained = true
  MakeInternals = false
  MapMode = 5
  sketch-geometry (2):
    g0: LineSegment [constr] StartX=0 StartY=0 StartZ=0 EndX=-16.5 EndY=0 EndZ=0
    g1: Circle CenterX=-16.5 CenterY=0 CenterZ=0 NormalX=0 NormalY=0 NormalZ=1 AngleXU=0 Radius=2.5
  constraints (5):
    c: Distance(g0) = 16.5
    c: Coincident(g0,g-1)
    c: PointOnObject(g0,g-1)
    c: Diameter(g1) = 5
    c: Coincident(g0,g1)
FEATURE [Sketcher::SketchObject] Sketch027  label="foro sotto posteriore M3x5x6"
  ArcFitTolerance = 1e-06
  AttachmentSupport = -> [XY_Plane]
  ExternalGeometry = -> [Sketch]
  FullyConstrained = true
  MakeInternals = false
  MapMode = 5
  sketch-geometry (2):
    g0: LineSegment [constr] StartX=-82.8 StartY=2e-16 StartZ=0 EndX=-71.3 EndY=2e-16 EndZ=0
    g1: Circle CenterX=-71.3 CenterY=2e-16 CenterZ=0 NormalX=0 NormalY=0 NormalZ=1 AngleXU=0 Radius=2.5
  constraints (5):
    c: Distance(g0) = 11.5
    c: Coincident(g0,g-3)
    c: PointOnObject(g0,g-3)
    c: Diameter(g1) = 5
    c: Coincident(g1,g0)
FEATURE [Sketcher::SketchObject] Sketch029  label="fori sotto impugnatura"
  ArcFitTolerance = 1e-06
  AttachmentSupport = -> [XY_Plane]
  ExternalGeometry = -> [Sketch]
  FullyConstrained = true
  MakeInternals = false
  MapMode = 5
  sketch-geometry (15):
    g0: LineSegment [constr] StartX=-175.232 StartY=-1.83e-14 StartZ=0 EndX=-191.232 EndY=0 EndZ=0
    g1: Circle CenterX=-191.232 CenterY=0 CenterZ=0 NormalX=0 NormalY=0 NormalZ=1 AngleXU=0 Radius=3.95
    g2: LineSegment [constr] StartX=-175.232 StartY=-1.83e-14 StartZ=0 EndX=-204.275 EndY=0 EndZ=0
    g3: LineSegment StartX=-204.275 StartY=3.525 StartZ=0 EndX=-204.275 EndY=-3.525 EndZ=0
    g4: LineSegment StartX=-205.4 StartY=-4.65 StartZ=0 EndX=-206.65 EndY=-4.65 EndZ=0
    g5: LineSegment StartX=-207.775 StartY=-3.525 StartZ=0 EndX=-207.775 EndY=3.525 EndZ=0
    g6: LineSegment StartX=-206.65 StartY=4.65 StartZ=0 EndX=-205.4 EndY=4.65 EndZ=0
    g7: ArcOfCircle CenterX=-206.65 CenterY=3.525 CenterZ=0 NormalX=0 NormalY=0 NormalZ=1 AngleXU=0 Radius=1.125 StartAngle=1.5708 EndAngle=3.14159
    g8: GeomPoint [constr] X=-207.775 Y=4.65 Z=0
    g9: ArcOfCircle CenterX=-205.4 CenterY=3.525 CenterZ=0 NormalX=0 NormalY=0 NormalZ=1 AngleXU=0 Radius=1.125 StartAngle=0 EndAngle=1.5708
    g10: GeomPoint [constr] X=-204.275 Y=4.65 Z=0
    g11: ArcOfCircle CenterX=-205.4 CenterY=-3.525 CenterZ=0 NormalX=0 NormalY=0 NormalZ=1 AngleXU=0 Radius=1.125 StartAngle=4.71239 EndAngle=6.28319
    g12: GeomPoint [constr] X=-204.275 Y=-4.65 Z=0
    g13: ArcOfCircle CenterX=-206.65 CenterY=-3.525 CenterZ=0 NormalX=0 NormalY=0 NormalZ=1 AngleXU=0 Radius=1.125 StartAngle=3.14159 EndAngle=4.71239
    g14: GeomPoint [constr] X=-207.775 Y=-4.65 Z=0
  constraints (35):
    c: Distance(g0) = 16
    c: Coincident(g0,g-3)
    c: PointOnObject(g0,g-1)
    c: Diameter(g1) = 7.9
    c: Coincident(g1,g0)
    c: Coincident(g2,g0)
    c: PointOnObject(g2,g-1)
    c: Vertical(g3)
    c: Horizontal(g4)
    c: Vertical(g5)
    c: Horizontal(g6)
    c: DistanceY(g12,g10) = 9.3
    c: DistanceX(g8,g10) = 3.5
    c: Symmetric(g10,g12,g2)
    c: PointOnObject(g8,g5)
    c: PointOnObject(g8,g6)
    c: Tangent(g5,g7) = 1.5708
    c: Tangent(g6,g7) = 1.5708
    c: PointOnObject(g10,g3)
    c: PointOnObject(g10,g6)
    c: Tangent(g3,g9) = 1.5708
    c: Tangent(g6,g9) = 1.5708
    c: PointOnObject(g12,g3)
    c: PointOnObject(g12,g4)
    c: Tangent(g3,g11) = 1.5708
    c: Tangent(g4,g11) = 1.5708
    c: PointOnObject(g14,g4)
    c: PointOnObject(g14,g5)
    c: Tangent(g4,g13) = 1.5708
    c: Tangent(g5,g13) = 1.5708
    c: Equal(g7,g9)
    c: Equal(g9,g11)
    c: Equal(g11,g13)
    c: DistanceX(g6,g6) = 1.25
    c: DistanceX(g-5,g5) = 6.8
FEATURE [Sketcher::SketchObject] Sketch030  label="fori superiori per solenoide e oled"
  ArcFitTolerance = 1e-06
  AttachmentSupport = -> [XY_Plane]
  ExternalGeometry = -> [Sketch]
  FullyConstrained = true
  MakeInternals = false
  MapMode = 5
  sketch-geometry (33):
    g0: LineSegment [constr] StartX=-181.6 StartY=1.12e-14 StartZ=0 EndX=-169.91 EndY=0 EndZ=0
    g1: LineSegment [constr] StartX=-169.91 StartY=0 StartZ=0 EndX=-169.91 EndY=-2.6 EndZ=0
    g2: LineSegment [constr] StartX=-169.91 StartY=0 StartZ=0 EndX=-169.91 EndY=2.6 EndZ=0
    g3: LineSegment StartX=-169.91 StartY=4.975 StartZ=0 EndX=-169.91 EndY=8.225 EndZ=0
    g4: LineSegment StartX=-167.535 StartY=10.6 StartZ=0 EndX=-167.285 EndY=10.6 EndZ=0
    g5: LineSegment StartX=-164.91 StartY=8.225 StartZ=0 EndX=-164.91 EndY=4.975 EndZ=0
    g6: LineSegment StartX=-167.285 StartY=2.6 StartZ=0 EndX=-167.535 EndY=2.6 EndZ=0
    g7: LineSegment StartX=-169.91 StartY=-4.975 StartZ=0 EndX=-169.91 EndY=-8.225 EndZ=0
    g8: LineSegment StartX=-167.535 StartY=-10.6 StartZ=0 EndX=-167.285 EndY=-10.6 EndZ=0
    g9: LineSegment StartX=-164.91 StartY=-8.225 StartZ=0 EndX=-164.91 EndY=-4.975 EndZ=0
    g10: LineSegment StartX=-167.285 StartY=-2.6 StartZ=0 EndX=-167.535 EndY=-2.6 EndZ=0
    g11: ArcOfCircle CenterX=-167.535 CenterY=8.225 CenterZ=0 NormalX=0 NormalY=0 NormalZ=1 AngleXU=0 Radius=2.375 StartAngle=1.5708 EndAngle=3.14159
    g12: GeomPoint [constr] X=-169.91 Y=10.6 Z=0
    g13: ArcOfCircle CenterX=-167.285 CenterY=8.225 CenterZ=0 NormalX=0 NormalY=0 NormalZ=1 AngleXU=0 Radius=2.375 StartAngle=0 EndAngle=1.5708
    g14: GeomPoint [constr] X=-164.91 Y=10.6 Z=0
    g15: ArcOfCircle CenterX=-167.285 CenterY=4.975 CenterZ=0 NormalX=0 NormalY=0 NormalZ=1 AngleXU=0 Radius=2.375 StartAngle=4.71239 EndAngle=6.28319
    g16: GeomPoint [constr] X=-164.91 Y=2.6 Z=0
    g17: ArcOfCircle CenterX=-167.535 CenterY=4.975 CenterZ=0 NormalX=0 NormalY=0 NormalZ=1 AngleXU=0 Radius=2.375 StartAngle=3.14159 EndAngle=4.71239
    g18: GeomPoint [constr] X=-169.91 Y=2.6 Z=0
    g19: ArcOfCircle CenterX=-167.535 CenterY=-4.975 CenterZ=0 NormalX=0 NormalY=0 NormalZ=1 AngleXU=0 Radius=2.375 StartAngle=1.5708 EndAngle=3.14159
    g20: GeomPoint [constr] X=-169.91 Y=-2.6 Z=0
    g21: ArcOfCircle CenterX=-167.285 CenterY=-4.975 CenterZ=0 NormalX=0 NormalY=0 NormalZ=1 AngleXU=0 Radius=2.375 StartAngle=0 EndAngle=1.5708
    g22: GeomPoint [constr] X=-164.91 Y=-2.6 Z=0
    g23: ArcOfCircle CenterX=-167.285 CenterY=-8.225 CenterZ=0 NormalX=0 NormalY=0 NormalZ=1 AngleXU=0 Radius=2.375 StartAngle=4.71239 EndAngle=6.28319
    g24: GeomPoint [constr] X=-164.91 Y=-10.6 Z=0
    g25: ArcOfCircle CenterX=-167.535 CenterY=-8.225 CenterZ=0 NormalX=0 NormalY=0 NormalZ=1 AngleXU=0 Radius=2.375 StartAngle=3.14159 EndAngle=4.71239
    g26: GeomPoint [constr] X=-169.91 Y=-10.6 Z=0
    g27: LineSegment [constr] StartX=-181.6 StartY=1.12e-14 StartZ=0 EndX=-152.209 EndY=0 EndZ=0
    g28: LineSegment [constr] StartX=-181.6 StartY=1.12e-14 StartZ=0 EndX=-130.41 EndY=0 EndZ=0
    g29: LineSegment [constr] StartX=-152.209 StartY=0 StartZ=0 EndX=-152.209 EndY=6.95 EndZ=0
    g30: LineSegment [constr] StartX=-130.41 StartY=0 StartZ=0 EndX=-130.41 EndY=-6.95 EndZ=0
    g31: Circle CenterX=-152.209 CenterY=6.95 CenterZ=0 NormalX=0 NormalY=0 NormalZ=1 AngleXU=0 Radius=2.1
    g32: Circle CenterX=-130.41 CenterY=-6.95 CenterZ=0 NormalX=0 NormalY=0 NormalZ=1 AngleXU=0 Radius=2.1
  constraints (79):
    c: Distance(g0) = 11.69
    c: PointOnObject(g0,g-1)
    c: Coincident(g-4,g0)
    c: Distance(g1) = 2.6
    c: Coincident(g1,g0)
    c: Vertical(g1)
    c: Distance(g2) = 2.6
    c: Coincident(g2,g0)
    c: Vertical(g2)
    c: Distance(g18,g12) = 8
    c: Coincident(g18,g2)
    c: Vertical(g3)
    c: Distance(g14,g12) = 5
    c: Horizontal(g4)
    c: Distance(g16,g14) = 8
    c: Vertical(g5)
    c: Distance(g26,g20) = 8
    c: Coincident(g20,g1)
    c: Vertical(g7)
    c: Distance(g26,g24) = 5
    c: Horizontal(g8)
    c: Distance(g24,g22) = 8
    c: Vertical(g9)
    c: PointOnObject(g12,g3)
    c: PointOnObject(g12,g4)
    c: Tangent(g3,g11) = 1.5708
    c: Tangent(g4,g11) = 1.5708
    c: PointOnObject(g14,g5)
    c: PointOnObject(g14,g4)
    c: Tangent(g5,g13) = 1.5708
    c: Tangent(g4,g13) = 1.5708
    c: PointOnObject(g16,g5)
    c: PointOnObject(g16,g6)
    c: Tangent(g5,g15) = 1.5708
    c: Tangent(g6,g15) = 1.5708
    c: PointOnObject(g18,g3)
    c: PointOnObject(g18,g6)
    c: Tangent(g3,g17) = 1.5708
    c: Tangent(g6,g17) = 1.5708
    c: Equal(g11,g13)
    c: Equal(g13,g15)
    c: Equal(g15,g17)
    c: DistanceX(g4,g4) = 0.25
    c: PointOnObject(g20,g7)
    c: PointOnObject(g20,g10)
    c: Tangent(g7,g19) = -1.5708
    c: Tangent(g10,g19) = -1.5708
    c: PointOnObject(g22,g9)
    c: PointOnObject(g22,g10)
    c: Tangent(g9,g21) = -1.5708
    c: Tangent(g10,g21) = -1.5708
    c: PointOnObject(g24,g9)
    c: PointOnObject(g24,g8)
    c: Tangent(g9,g23) = -1.5708
    c: Tangent(g8,g23) = -1.5708
    c: PointOnObject(g26,g8)
    c: PointOnObject(g26,g7)
    c: Tangent(g8,g25) = -1.5708
    c: Tangent(g7,g25) = -1.5708
    c: Equal(g19,g21)
    c: Equal(g21,g23)
    c: Equal(g23,g25)
    c: DistanceX(g10,g10) = 0.25
    c: Distance(g27) = 29.391
    c: Coincident(g27,g0)
    c: PointOnObject(g27,g-1)
    c: Distance(g28) = 51.19
    c: Coincident(g28,g0)
    c: PointOnObject(g28,g-1)
    c: Distance(g29) = 6.95
    c: Coincident(g29,g27)
    c: Vertical(g29)
    c: Distance(g30) = 6.95
    c: Coincident(g30,g28)
    c: Vertical(g30)
    c: Diameter(g31) = 4.2
    c: Diameter(g32) = 4.2
    c: Coincident(g32,g30)
    c: Coincident(g31,g29)
FEATURE [Sketcher::SketchObject] Sketch031  label="fori inferiori switch pompa"
  ArcFitTolerance = 1e-06
  AttachmentSupport = -> [XY_Plane]
  ExternalGeometry = -> [Sketch]
  FullyConstrained = true
  MakeInternals = false
  MapMode = 5
  sketch-geometry (4):
    g0: LineSegment [constr] StartX=-57.2 StartY=1.9e-15 StartZ=0 EndX=-62.45 EndY=1.9e-15 EndZ=0
    g1: LineSegment [constr] StartX=-62.45 StartY=3.25 StartZ=0 EndX=-62.45 EndY=-3.25 EndZ=0
    g2: Circle CenterX=-62.45 CenterY=3.25 CenterZ=0 NormalX=0 NormalY=0 NormalZ=1 AngleXU=0 Radius=1.6
    g3: Circle CenterX=-62.45 CenterY=-3.25 CenterZ=0 NormalX=0 NormalY=0 NormalZ=1 AngleXU=0 Radius=1.6
  constraints (10):
    c: Distance(g0) = 5.25
    c: Coincident(g0,g-3)
    c: PointOnObject(g0,g-3)
    c: Vertical(g1)
    c: DistanceY(g1,g1) = 6.5
    c: Symmetric(g1,g1,g0)
    c: Diameter(g2) = 3.2
    c: Diameter(g3) = 3.2
    c: Coincident(g2,g1)
    c: Coincident(g3,g1)
FEATURE [Sketcher::SketchObject] Sketch032  label="spazio per PILA 18650"
  ArcFitTolerance = 1e-06
  AttachmentSupport = -> [XY_Plane]
  ExternalGeometry = -> [Sketch]
  FullyConstrained = true
  MakeInternals = false
  MapMode = 5
  sketch-geometry (2):
    g0: LineSegment [constr] StartX=-178.142 StartY=-1.74e-14 StartZ=0 EndX=-190.142 EndY=-1.83e-14 EndZ=0
    g1: Circle CenterX=-190.142 CenterY=-1.83e-14 CenterZ=0 NormalX=0 NormalY=0 NormalZ=1 AngleXU=0 Radius=9.25
  constraints (5):
    c: Distance(g0) = 12
    c: Coincident(g0,g-3)
    c: PointOnObject(g0,g-4)
    c: Diameter(g1) = 18.5
    c: Coincident(g1,g0)
FEATURE [Part::Extrusion] Extrude030  label="Extrude spazio per PILA 18650"
  Base = -> Sketch032
  Dir = (0,0,1)
  DirLink = -> Sketch [Edge45]
  DirMode = 2
  FaceMakerClass = Part::FaceMakerBullseye
  FaceMakerMode = 3
  LengthFwd = 68
  LengthRev = 0
  Placement = pos=(6,0,-72.7) rot=(0,0,1;0rad)
  Solid = true
  Symmetric = false
FEATURE [Sketcher::SketchObject] Sketch033  label="fermo per scheda micro"
  ArcFitTolerance = 1e-06
  AttachmentSupport = -> [XZ_Plane]
  ExternalGeometry = -> [Sketch]
  FullyConstrained = true
  MakeInternals = false
  MapMode = 5
  Placement = pos=(0,0,0) rot=(1,0,0;1.5708rad)
  sketch-geometry (12):
    g0: LineSegment StartX=-11.6 StartY=6 StartZ=0 EndX=-4 EndY=6 EndZ=0
    g1: LineSegment StartX=-4 StartY=6 StartZ=0 EndX=-4 EndY=36.4 EndZ=0
    g2: LineSegment StartX=-4 StartY=36.4 StartZ=0 EndX=-11.6 EndY=36.4 EndZ=0
    g3: LineSegment StartX=-11.6 StartY=36.4 StartZ=0 EndX=-11.6 EndY=6 EndZ=0
    g4: LineSegment StartX=-80.11 StartY=11.6 StartZ=0 EndX=-70.51 EndY=11.6 EndZ=0
    g5: LineSegment StartX=-70.51 StartY=11.6 StartZ=0 EndX=-70.51 EndY=6 EndZ=0
    g6: LineSegment StartX=-70.51 StartY=6 StartZ=0 EndX=-80.11 EndY=6 EndZ=0
    g7: LineSegment StartX=-80.11 StartY=6 StartZ=0 EndX=-80.11 EndY=11.6 EndZ=0
    g8: LineSegment StartX=-78.51 StartY=36.4 StartZ=0 EndX=-70.51 EndY=36.4 EndZ=0
    g9: LineSegment StartX=-70.51 StartY=36.4 StartZ=0 EndX=-70.51 EndY=30.8 EndZ=0
    g10: LineSegment StartX=-70.51 StartY=30.8 StartZ=0 EndX=-78.51 EndY=30.8 EndZ=0
    g11: LineSegment StartX=-78.51 StartY=30.8 StartZ=0 EndX=-78.51 EndY=36.4 EndZ=0
  constraints (33):
    c: Horizontal(g0)
    c: Coincident(g1,g0)
    c: Coincident(g2,g1)
    c: Horizontal(g2)
    c: Coincident(g3,g2)
    c: Coincident(g3,g0)
    c: Vertical(g3)
    c: DistanceX(g2,g2) = 7.6
    c: Coincident(g1,g-3)
    c: Coincident(g0,g-3)
    c: Horizontal(g4)
    c: Coincident(g5,g4)
    c: Vertical(g5)
    c: Coincident(g6,g5)
    c: Horizontal(g6)
    c: Coincident(g7,g6)
    c: Coincident(g7,g4)
    c: Vertical(g7)
    c: DistanceY(g5,g5) = 5.6
    c: DistanceX(g4,g4) = 9.6
    c: Coincident(g9,g8)
    c: Vertical(g9)
    c: Coincident(g10,g9)
    c: Horizontal(g10)
    c: Coincident(g11,g10)
    c: Coincident(g11,g8)
    c: Vertical(g11)
    c: DistanceY(g9,g9) = 5.6
    c: DistanceX(g10,g10) = 8
    c: Coincident(g4,g-4)
    c: DistanceX(g4,g10) = 1.6
    c: Horizontal(g8)
    c: DistanceY(g8,g1) = 0
FEATURE [Sketcher::SketchObject] Sketch034  label="buchi guida rail"
  ArcFitTolerance = 1e-06
  AttachmentSupport = -> [XY_Plane]
  ExternalGeometry = -> [Sketch]
  FullyConstrained = true
  MakeInternals = false
  MapMode = 5
  sketch-geometry (6):
    g0: LineSegment [constr] StartX=-100.8 StartY=9.1e-15 StartZ=0 EndX=-93.3 EndY=0 EndZ=0
    g1: LineSegment [constr] StartX=-93.3 StartY=0 StartZ=0 EndX=-73.3 EndY=0 EndZ=0
    g2: LineSegment [constr] StartX=-73.3 StartY=0 StartZ=0 EndX=-53.3 EndY=0 EndZ=0
    g3: Circle CenterX=-93.3 CenterY=0 CenterZ=0 NormalX=0 NormalY=0 NormalZ=1 AngleXU=0 Radius=2.5
    g4: Circle CenterX=-73.3 CenterY=0 CenterZ=0 NormalX=0 NormalY=0 NormalZ=1 AngleXU=0 Radius=2.5
    g5: Circle CenterX=-53.3 CenterY=0 CenterZ=0 NormalX=0 NormalY=0 NormalZ=1 AngleXU=0 Radius=2.5
  constraints (15):
    c: Distance(g0) = 7.5
    c: Coincident(g0,g-3)
    c: PointOnObject(g0,g-1)
    c: Distance(g1) = 20
    c: Coincident(g1,g0)
    c: PointOnObject(g1,g-1)
    c: Distance(g2) = 20
    c: Coincident(g2,g1)
    c: PointOnObject(g2,g-1)
    c: Diameter(g3) = 5
    c: Diameter(g4) = 5
    c: Diameter(g5) = 5
    c: Coincident(g3,g0)
    c: Coincident(g4,g1)
    c: Coincident(g5,g2)
FEATURE [PartDesign::FeatureBase] BaseFeature
  BaseFeature = -> Extrude017
  Suppressed = false
FEATURE [PartDesign::Body] Body001  label="perno fermo rumble"
  AllowCompound = false
  BaseFeature = -> Extrude017
  Group = -> [BaseFeature,Sketch021]
  Origin = -> Origin001
  Tip = -> BaseFeature
FEATURE [Part::Extrusion] Extrude032  label="Extrude buchi guida rail"
  Base = -> Sketch034
  Dir = (0,0,1)
  DirMode = 2
  FaceMakerClass = Part::FaceMakerBullseye
  FaceMakerMode = 3
  LengthFwd = -6.2
  LengthRev = 0
  Placement = pos=(0,0,43.2) rot=(0,0,1;0rad)
  Solid = true
  Symmetric = false
FEATURE [Part::Extrusion] Extrude033  label="Extrude fori superiori per solenoide e oled001"
  Base = -> Sketch030
  Dir = (0,0,1)
  DirMode = 2
  FaceMakerClass = Part::FaceMakerBullseye
  FaceMakerMode = 3
  LengthFwd = -4.8
  LengthRev = 0
  Placement = pos=(0,0,41.2) rot=(0,0,1;0rad)
  Solid = true
  Symmetric = false
FEATURE [Part::Extrusion] Extrude034  label="Extrude fori sotto impugnatura001"
  Base = -> Sketch029
  Dir = (0,0,1)
  DirMode = 2
  FaceMakerClass = Part::FaceMakerBullseye
  FaceMakerMode = 3
  LengthFwd = 5
  LengthRev = 0
  Placement = pos=(0,0,-83) rot=(0,0,1;0rad)
  Solid = true
  Symmetric = false
FEATURE [Part::Extrusion] Extrude035  label="Extrude fori inferiori switch pompa001"
  Base = -> Sketch031
  Dir = (0,0,1)
  DirMode = 2
  FaceMakerClass = Part::FaceMakerBullseye
  FaceMakerMode = 3
  LengthFwd = 4
  LengthRev = 0
  Placement = pos=(0,0,-1.7) rot=(0,0,1;0rad)
  Solid = true
  Symmetric = false
FEATURE [Part::Extrusion] Extrude036  label="Extrude foro sotto posteriore M3x5x007"
  Base = -> Sketch027
  Dir = (0,0,1)
  DirMode = 2
  FaceMakerClass = Part::FaceMakerBullseye
  FaceMakerMode = 3
  LengthFwd = 6.2
  LengthRev = 0
  Placement = pos=(0,0,-9.6) rot=(0,0,1;0rad)
  Solid = true
  Symmetric = false
FEATURE [Part::Extrusion] Extrude037  label="Extrude foro sotto anteriore M3x5x007"
  Base = -> Sketch026
  Dir = (0,0,1)
  DirMode = 2
  FaceMakerClass = Part::FaceMakerBullseye
  FaceMakerMode = 3
  LengthFwd = 6.2
  LengthRev = 0
  Solid = true
  Symmetric = false
FEATURE [Sketcher::SketchObject] Sketch035  label="foro per fissaggio micro"
  ArcFitTolerance = 1e-06
  AttachmentSupport = -> [XZ_Plane]
  ExternalGeometry = -> [Sketch,Sketch033]
  FullyConstrained = true
  MakeInternals = false
  MapMode = 5
  Placement = pos=(0,0,0) rot=(1,0,0;1.5708rad)
  sketch-geometry (3):
    g0: Circle CenterX=-7.8 CenterY=21.2 CenterZ=0 NormalX=0 NormalY=0 NormalZ=1 AngleXU=0 Radius=1.6
    g1: GeomPoint [constr] X=-4 Y=21.2 Z=0
    g2: LineSegment [constr] StartX=-4 StartY=21.2 StartZ=0 EndX=-11.6 EndY=21.2 EndZ=0
  constraints (6):
    c: Diameter(g0) = 3.2
    c: Symmetric(g-3,g-3,g1)
    c: Coincident(g2,g1)
    c: Horizontal(g2)
    c: DistanceX(g-4,g2) = 0
    c: Symmetric(g2,g1,g0)
FEATURE [Part::Extrusion] Extrude038  label="Extrude foro per fissaggio micro"
  Base = -> Sketch035
  Dir = (0,-1,2e-16)
  DirMode = 2
  FaceMakerClass = Part::FaceMakerBullseye
  FaceMakerMode = 3
  LengthFwd = 3
  LengthRev = 0
  Placement = pos=(0,8.6,0) rot=(0,0,1;0rad)
  Solid = true
  Symmetric = false
FEATURE [Sketcher::SketchObject] Sketch036  label="supporto per alimentatore"
  ArcFitTolerance = 1e-06
  AttachmentSupport = -> [XZ_Plane]
  ExternalGeometry = -> [Sketch,Sketch016,Sketch022]
  FullyConstrained = true
  MakeInternals = false
  MapMode = 5
  Placement = pos=(0,0,0) rot=(1,0,0;1.5708rad)
  sketch-geometry (5):
    g0: LineSegment StartX=-211.843 StartY=-50.0944 StartZ=0 EndX=-211.843 EndY=-80.4316 EndZ=0
    g1: LineSegment StartX=-211.843 StartY=-50.0944 StartZ=0 EndX=-207.775 EndY=-41.3701 EndZ=0
    g2: LineSegment [constr] StartX=-209.443 StartY=-50.0944 StartZ=0 EndX=-209.443 EndY=-80.4316 EndZ=0
    g3: LineSegment StartX=-207.775 StartY=-41.3701 StartZ=0 EndX=-207.775 EndY=-80.4316 EndZ=0
    g4: LineSegment StartX=-211.843 StartY=-80.4316 StartZ=0 EndX=-207.775 EndY=-80.4316 EndZ=0
  constraints (15):
    c: Vertical(g0)
    c: Coincident(g1,g0)
    c: Vertical(g2)
    c: Tangent(g2,g-5)
    c: Coincident(g3,g1)
    c: Vertical(g3)
    c: DistanceY(g-3,g3) = -2
    c: Tangent(g1,g-8)
    c: DistanceY(g-3,g0) = -2
    c: Coincident(g4,g0)
    c: Coincident(g4,g3)
    c: Tangent(g0,g-6)
    c: DistanceY(g-3,g2) = -2
    c: DistanceY(g2,g0) = 0
    c: DistanceX(g-3,g3) = 6.8
FEATURE [Part::Extrusion] Extrude039  label="Extrude039 supporto alimentatore"
  Base = -> Sketch036
  Dir = (0,-1,2e-16)
  DirMode = 2
  FaceMakerClass = Part::FaceMakerBullseye
  FaceMakerMode = 3
  LengthFwd = 25.2
  LengthRev = 0
  Solid = true
  Symmetric = true
FEATURE [Sketcher::SketchObject] Sketch037  label="scavo per alimentatore"
  ArcFitTolerance = 1e-06
  AttachmentSupport = -> [XZ_Plane]
  ExternalGeometry = -> [Sketch036]
  FullyConstrained = true
  MakeInternals = false
  MapMode = 5
  Placement = pos=(0,0,0) rot=(1,0,0;1.5708rad)
  sketch-geometry (4):
    g0: LineSegment StartX=-209.575 StartY=-50.4316 StartZ=0 EndX=-209.575 EndY=-80.4316 EndZ=0
    g1: LineSegment StartX=-209.575 StartY=-50.4316 StartZ=0 EndX=-207.775 EndY=-50.4316 EndZ=0
    g2: LineSegment StartX=-207.775 StartY=-50.4316 StartZ=0 EndX=-207.775 EndY=-80.4316 EndZ=0
    g3: LineSegment StartX=-207.775 StartY=-80.4316 StartZ=0 EndX=-209.575 EndY=-80.4316 EndZ=0
  constraints (11):
    c: Vertical(g0)
    c: Coincident(g1,g0)
    c: Horizontal(g1)
    c: Coincident(g2,g1)
    c: Vertical(g2)
    c: Coincident(g3,g2)
    c: Coincident(g3,g0)
    c: Horizontal(g3)
    c: DistanceX(g1,g1) = 1.8
    c: Coincident(g2,g-3)
    c: DistanceY(g2,g2) = 30
FEATURE [Part::Extrusion] Extrude040  label="Extrude040 scavo alimentatore"
  Base = -> Sketch037
  Dir = (0,-1,2e-16)
  DirMode = 2
  FaceMakerClass = Part::FaceMakerBullseye
  FaceMakerMode = 3
  LengthFwd = 19.5
  LengthRev = 0
  Solid = true
  Symmetric = true
FEATURE [Part::Extrusion] Extrude031  label="Extrude fermo per scheda micro"
  Base = -> Sketch033
  Dir = (0,-1,2e-16)
  DirMode = 2
  FaceMakerClass = Part::FaceMakerBullseye
  FaceMakerMode = 3
  LengthFwd = 3
  LengthRev = 0
  Placement = pos=(0,8.6,0) rot=(0,0,1;0rad)
  Solid = true
  Symmetric = false
FEATURE [Sketcher::SketchObject] Sketch038  label="scavo driver solenoide"
  ArcFitTolerance = 1e-06
  AttachmentSupport = -> [XZ_Plane]
  ExternalGeometry = -> [Sketch,Sketch036]
  FullyConstrained = true
  MakeInternals = false
  MapMode = 5
  Placement = pos=(0,0,0) rot=(1,0,0;1.5708rad)
  sketch-geometry (7):
    g0: LineSegment StartX=-193.66 StartY=-11.0994 StartZ=0 EndX=-195.11 EndY=-10.4232 EndZ=0
    g1: LineSegment StartX=-195.11 StartY=-10.4232 StartZ=0 EndX=-209.225 EndY=-40.6939 EndZ=0
    g2: LineSegment StartX=-193.66 StartY=-11.0994 StartZ=0 EndX=-190.216 EndY=-12.7054 EndZ=0
    g3: LineSegment StartX=-190.216 StartY=-12.7054 StartZ=0 EndX=-204.331 EndY=-42.9761 EndZ=0
    g4: LineSegment StartX=-204.331 StartY=-42.9761 StartZ=0 EndX=-207.775 EndY=-41.3701 EndZ=0
    g5: LineSegment [constr] StartX=-209.225 StartY=-40.6939 StartZ=0 EndX=-207.775 EndY=-41.3701 EndZ=0
    g6: LineSegment StartX=-209.225 StartY=-40.6939 StartZ=0 EndX=-207.775 EndY=-41.3701 EndZ=0
  constraints (19):
    c: Coincident(g1,g0)
    c: Coincident(g3,g2)
    c: Coincident(g4,g3)
    c: Distance(g2) = 3.8
    c: Distance(g1) = 33.4
    c: Coincident(g5,g1)
    c: Distance(g5) = 1.6
    c: Coincident(g-4,g5)
    c: Perpendicular(g5,g-3)
    c: Parallel(g1,g-3)
    c: Perpendicular(g1,g0)
    c: Distance(g0) = 1.6
    c: Coincident(g6,g1)
    c: Coincident(g6,g5)
    c: Parallel(g3,g-3)
    c: Perpendicular(g3,g4)
    c: Perpendicular(g2,g3)
    c: Coincident(g2,g0)
    c: Coincident(g4,g5)
FEATURE [Part::Extrusion] Extrude041  label="Extrude scavo driver solenoide"
  Base = -> Sketch038
  Dir = (0,-1,2e-16)
  DirMode = 2
  FaceMakerClass = Part::FaceMakerBullseye
  FaceMakerMode = 3
  LengthFwd = 17
  LengthRev = 0
  Solid = true
  Symmetric = true
FEATURE [Sketcher::SketchObject] Sketch039  label="scavo per cavo usb per micro"
  ArcFitTolerance = 1e-06
  AttachmentSupport = -> [XZ_Plane]
  ExternalGeometry = -> [Sketch,Sketch016]
  FullyConstrained = true
  MakeInternals = false
  MapMode = 5
  Placement = pos=(0,0,0) rot=(1,0,0;1.5708rad)
  sketch-geometry (4):
    g0: LineSegment StartX=-82.51 StartY=36.4 StartZ=0 EndX=-74.51 EndY=36.4 EndZ=0
    g1: LineSegment StartX=-74.51 StartY=36.4 StartZ=0 EndX=-74.51 EndY=30.8 EndZ=0
    g2: LineSegment StartX=-74.51 StartY=30.8 StartZ=0 EndX=-82.51 EndY=30.8 EndZ=0
    g3: LineSegment StartX=-82.51 StartY=30.8 StartZ=0 EndX=-82.51 EndY=36.4 EndZ=0
  constraints (11):
    c: Coincident(g1,g0)
    c: Vertical(g1)
    c: Coincident(g2,g1)
    c: Horizontal(g2)
    c: Coincident(g3,g2)
    c: Coincident(g3,g0)
    c: Vertical(g3)
    c: Tangent(g0,g-3)
    c: Tangent(g2,g-4)
    c: Tangent(g3,g-4)
    c: Tangent(g1,g-4)
FEATURE [Part::Extrusion] Extrude042  label="Extrude scavo per cavo usb per micro"
  Base = -> Sketch039
  Dir = (0,-1,2e-16)
  DirMode = 2
  FaceMakerClass = Part::FaceMakerBullseye
  FaceMakerMode = 3
  LengthFwd = 11.2
  LengthRev = 0
  Solid = true
  Symmetric = true
FEATURE [Sketcher::SketchObject] Sketch040  label="scavo saldature alimentatore connettore 5v"
  ArcFitTolerance = 1e-06
  AttachmentSupport = -> [XZ_Plane]
  ExternalGeometry = -> [Sketch037]
  FullyConstrained = true
  MakeInternals = false
  MapMode = 5
  Placement = pos=(0,0,0) rot=(1,0,0;1.5708rad)
  sketch-geometry (4):
    g0: LineSegment StartX=-211.175 StartY=-52.4316 StartZ=0 EndX=-211.175 EndY=-56.4316 EndZ=0
    g1: LineSegment StartX=-211.175 StartY=-52.4316 StartZ=0 EndX=-209.575 EndY=-52.4316 EndZ=0
    g2: LineSegment StartX=-209.575 StartY=-52.4316 StartZ=0 EndX=-209.575 EndY=-56.4316 EndZ=0
    g3: LineSegment StartX=-209.575 StartY=-56.4316 StartZ=0 EndX=-211.175 EndY=-56.4316 EndZ=0
  constraints (11):
    c: Vertical(g0)
    c: Coincident(g1,g0)
    c: Horizontal(g1)
    c: Coincident(g2,g1)
    c: Coincident(g3,g2)
    c: Coincident(g3,g0)
    c: Horizontal(g3)
    c: DistanceX(g1,g1) = 1.6
    c: DistanceY(g2,g2) = 4
    c: Tangent(g2,g-3)
    c: DistanceY(g1,g-3) = 2
FEATURE [Part::Extrusion] Extrude043  label="Extrude scavo saldature alimentatore connettore 5v"
  Base = -> Sketch040
  Dir = (0,-1,2e-16)
  DirMode = 2
  FaceMakerClass = Part::FaceMakerBullseye
  FaceMakerMode = 3
  LengthFwd = 8
  LengthRev = 0
  Solid = true
  Symmetric = true
FEATURE [Sketcher::SketchObject] Sketch041  label="scavo saldature alimentatore connettore 5v verticali"
  ArcFitTolerance = 1e-06
  AttachmentSupport = -> [XZ_Plane]
  ExternalGeometry = -> [Sketch037]
  FullyConstrained = true
  MakeInternals = false
  MapMode = 5
  Placement = pos=(0,0,0) rot=(1,0,0;1.5708rad)
  sketch-geometry (4):
    g0: LineSegment StartX=-211.175 StartY=-53.6316 StartZ=0 EndX=-209.575 EndY=-53.6316 EndZ=0
    g1: LineSegment StartX=-209.575 StartY=-53.6316 StartZ=0 EndX=-209.575 EndY=-76.6316 EndZ=0
    g2: LineSegment StartX=-209.575 StartY=-76.6316 StartZ=0 EndX=-211.175 EndY=-76.6316 EndZ=0
    g3: LineSegment StartX=-211.175 StartY=-76.6316 StartZ=0 EndX=-211.175 EndY=-53.6316 EndZ=0
  constraints (11):
    c: Horizontal(g0)
    c: Coincident(g1,g0)
    c: Coincident(g2,g1)
    c: Horizontal(g2)
    c: Coincident(g3,g2)
    c: Coincident(g3,g0)
    c: Vertical(g3)
    c: DistanceY(g3,g3) = 23
    c: DistanceX(g0,g0) = 1.6
    c: Tangent(g1,g-3)
    c: DistanceY(g0,g-3) = 3.2
FEATURE [Part::Extrusion] Extrude044  label="Extrude scavo saldature alimentatore connettore 5v verticali"
  Base = -> Sketch041
  Dir = (0,-1,2e-16)
  DirMode = 2
  FaceMakerClass = Part::FaceMakerBullseye
  FaceMakerMode = 3
  LengthFwd = 3.2
  LengthRev = 0
  Placement = pos=(0,8.3,0) rot=(0,0,1;0rad)
  Solid = true
  Symmetric = false
FEATURE [Sketcher::SketchObject] Sketch042  label="fermi per driver solenoide e alimentatore"
  ArcFitTolerance = 1e-06
  AttachmentSupport = -> [XZ_Plane]
  ExternalGeometry = -> [Sketch036,Sketch037,Sketch,Sketch038]
  FullyConstrained = true
  MakeInternals = false
  MapMode = 5
  Placement = pos=(0,0,0) rot=(1,0,0;1.5708rad)
  sketch-geometry (27):
    g0: LineSegment StartX=-195.773 StartY=-15.631 StartZ=0 EndX=-196.702 EndY=-17.6249 EndZ=0
    g1: LineSegment StartX=-196.702 StartY=-17.6249 StartZ=0 EndX=-194.709 EndY=-18.5546 EndZ=0
    g2: LineSegment StartX=-194.709 StartY=-18.5546 StartZ=0 EndX=-193.779 EndY=-16.5607 EndZ=0
    g3: LineSegment StartX=-193.779 StartY=-16.5607 StartZ=0 EndX=-195.773 EndY=-15.631 EndZ=0
    g4: LineSegment StartX=-196.547 StartY=-13.5047 StartZ=0 EndX=-198.829 EndY=-18.3988 EndZ=0
    g5: LineSegment StartX=-198.829 StartY=-18.3988 StartZ=0 EndX=-195.385 EndY=-20.0047 EndZ=0
    g6: LineSegment StartX=-193.258 StartY=-19.2308 StartZ=0 EndX=-192.329 EndY=-17.2369 EndZ=0
    g7: LineSegment StartX=-193.103 StartY=-15.1106 StartZ=0 EndX=-196.547 EndY=-13.5047 EndZ=0
    g8: LineSegment [constr] StartX=-193.935 StartY=-20.6809 StartZ=0 EndX=-193.258 EndY=-19.2308 EndZ=0
    g9: LineSegment [constr] StartX=-193.935 StartY=-20.6809 StartZ=0 EndX=-195.385 EndY=-20.0047 EndZ=0
    g10: ArcOfCircle CenterX=-193.779 CenterY=-16.5607 CenterZ=0 NormalX=0 NormalY=0 NormalZ=1 AngleXU=0 Radius=1.6 StartAngle=5.84685 EndAngle=7.41765
    g11: GeomPoint [constr] X=-191.653 Y=-15.7868 Z=0
    g12: ArcOfCircle CenterX=-194.709 CenterY=-18.5546 CenterZ=0 NormalX=0 NormalY=0 NormalZ=1 AngleXU=0 Radius=1.6 StartAngle=4.27606 EndAngle=5.84685
    g13: GeomPoint [constr] X=-193.935 Y=-20.6809 Z=0
    g14: LineSegment StartX=-207.775 StartY=-46.8316 StartZ=0 EndX=-207.775 EndY=-50.8316 EndZ=0
    g15: LineSegment StartX=-207.775 StartY=-46.8316 StartZ=0 EndX=-203.775 EndY=-46.8316 EndZ=0
    g16: LineSegment StartX=-203.775 StartY=-46.8316 StartZ=0 EndX=-203.775 EndY=-50.8316 EndZ=0
    g17: LineSegment StartX=-207.775 StartY=-50.8316 StartZ=0 EndX=-203.775 EndY=-50.8316 EndZ=0
    g18: LineSegment StartX=-209.375 StartY=-52.4316 StartZ=0 EndX=-203.775 EndY=-52.4316 EndZ=0
    g19: LineSegment StartX=-202.175 StartY=-50.8316 StartZ=0 EndX=-202.175 EndY=-46.8316 EndZ=0
    g20: LineSegment StartX=-203.775 StartY=-45.2316 StartZ=0 EndX=-209.375 EndY=-45.2316 EndZ=0
    g21: LineSegment StartX=-209.375 StartY=-45.2316 StartZ=0 EndX=-209.375 EndY=-52.4316 EndZ=0
    g22: ArcOfCircle CenterX=-203.775 CenterY=-46.8316 CenterZ=0 NormalX=0 NormalY=0 NormalZ=1 AngleXU=0 Radius=1.6 StartAngle=1.8e-15 EndAngle=1.5708
    g23: GeomPoint [constr] X=-202.175 Y=-45.2316 Z=0
    g24: ArcOfCircle CenterX=-203.775 CenterY=-50.8316 CenterZ=0 NormalX=0 NormalY=0 NormalZ=1 AngleXU=0 Radius=1.6 StartAngle=4.71239 EndAngle=6.28319
    g25: GeomPoint [constr] X=-202.175 Y=-52.4316 Z=0
    g26: LineSegment [constr] StartX=-207.775 StartY=-50.4316 StartZ=0 EndX=-207.775 EndY=-50.8316 EndZ=0
  constraints (69):
    c: Coincident(g1,g0)
    c: Coincident(g2,g1)
    c: Coincident(g3,g2)
    c: Coincident(g3,g0)
    c: Parallel(g0,g2)
    c: Perpendicular(g3,g0)
    c: Perpendicular(g1,g0)
    c: Coincident(g5,g4)
    c: Coincident(g7,g4)
    c: Distance(g3) = 2.2
    c: Distance(g2) = 2.2
    c: Parallel(g6,g2)
    c: Parallel(g6,g4)
    c: Perpendicular(g5,g6)
    c: Perpendicular(g7,g6)
    c: Distance(g13,g11) = 5.4
    c: Distance(g5,g13) = 5.4
    c: Coincident(g9,g8)
    c: Distance(g8) = 1.6
    c: Distance(g9) = 1.6
    c: Perpendicular(g9,g8)
    c: Parallel(g8,g6)
    c: Coincident(g8,g13)
    c: Distance(g8,g1) = 1.6
    c: Distance(g9,g1) = 1.6
    c: Tangent(g0,g-5)
    c: Distance(g0,g-6) = 26.2
    c: PointOnObject(g11,g7)
    c: PointOnObject(g11,g6)
    c: Tangent(g7,g10) = -1.5708
    c: Tangent(g6,g10) = -1.5708
    c: PointOnObject(g13,g5)
    c: Tangent(g5,g12) = -1.5708
    c: Tangent(g6,g12) = -1.5708
    c: Equal(g10,g12)
    c: Coincident(g10,g2)
    c: Vertical(g14)
    c: Coincident(g15,g14)
    c: Horizontal(g15)
    c: Coincident(g16,g15)
    c: Vertical(g16)
    c: Coincident(g17,g14)
    c: Coincident(g17,g16)
    c: Horizontal(g17)
    c: Distance(g16) = 4
    c: Distance(g15) = 4
    c: Horizontal(g18)
    c: Vertical(g19)
    c: Horizontal(g20)
    c: Coincident(g21,g20)
    c: Coincident(g21,g18)
    c: Vertical(g21)
    c: Distance(g20,g23) = 7.2
    c: Distance(g25,g23) = 7.2
    c: DistanceY(g18,g14) = 1.6
    c: DistanceX(g18,g14) = 1.6
    c: PointOnObject(g23,g20)
    c: PointOnObject(g23,g19)
    c: Tangent(g20,g22) = -1.5708
    c: Tangent(g19,g22) = -1.5708
    c: PointOnObject(g25,g19)
    c: Tangent(g18,g24) = -1.5708
    c: Tangent(g19,g24) = -1.5708
    c: Equal(g22,g24)
    c: Coincident(g22,g15)
    c: Vertical(g26)
    c: Distance(g26) = 0.4
    c: Coincident(g26,g-4)
    c: Coincident(g14,g26)
FEATURE [Part::Extrusion] Extrude045  label="Extrude fermi per driver solenoide e alimentatore"
  Base = -> Sketch042
  Dir = (0,-1,2e-16)
  DirMode = 2
  FaceMakerClass = Part::FaceMakerBullseye
  FaceMakerMode = 3
  LengthFwd = 25.2
  LengthRev = 0
  Solid = true
  Symmetric = true
FEATURE [Sketcher::SketchObject] Sketch043  label="scavo pulizia fermo alimentatore"
  ArcFitTolerance = 1e-06
  AttachmentSupport = -> [XZ_Plane]
  ExternalGeometry = -> [Sketch042,Sketch036,Sketch037]
  FullyConstrained = true
  MakeInternals = false
  MapMode = 5
  Placement = pos=(0,0,0) rot=(1,0,0;1.5708rad)
  sketch-geometry (6):
    g0: LineSegment StartX=-209.375 StartY=-52.4316 StartZ=0 EndX=-209.375 EndY=-50.4316 EndZ=0
    g1: LineSegment StartX=-209.375 StartY=-50.4316 StartZ=0 EndX=-207.775 EndY=-50.4316 EndZ=0
    g2: LineSegment StartX=-207.775 StartY=-50.4316 StartZ=0 EndX=-207.775 EndY=-45.2316 EndZ=0
    g3: LineSegment StartX=-207.775 StartY=-45.2316 StartZ=0 EndX=-202.175 EndY=-45.2316 EndZ=0
    g4: LineSegment StartX=-202.175 StartY=-45.2316 StartZ=0 EndX=-202.175 EndY=-52.4316 EndZ=0
    g5: LineSegment StartX=-202.175 StartY=-52.4316 StartZ=0 EndX=-209.375 EndY=-52.4316 EndZ=0
  constraints (13):
    c: Vertical(g0)
    c: Coincident(g1,g0)
    c: Coincident(g2,g1)
    c: Coincident(g3,g2)
    c: Coincident(g4,g3)
    c: Coincident(g5,g4)
    c: Coincident(g5,g0)
    c: Horizontal(g5)
    c: Coincident(g0,g-6)
    c: Tangent(g1,g-8)
    c: Tangent(g2,g-4)
    c: Tangent(g3,g-7)
    c: Tangent(g4,g-3)
FEATURE [Part::Extrusion] Extrude046  label="Extrude scavo pulizia fermo alimentatore"
  Base = -> Sketch043
  Dir = (0,-1,2e-16)
  DirMode = 2
  FaceMakerClass = Part::FaceMakerBullseye
  FaceMakerMode = 3
  LengthFwd = 19.5
  LengthRev = 0
  Solid = true
  Symmetric = true
FEATURE [Sketcher::SketchObject] Sketch044  label="buchini per fissaggio oled"
  ArcFitTolerance = 1e-06
  AttachmentSupport = -> [YZ_Plane]
  ExternalGeometry = -> [Sketch]
  FullyConstrained = true
  MakeInternals = false
  MapMode = 5
  Placement = pos=(0,0,0) rot=(0.57735,0.57735,0.57735;2.0944rad)
  sketch-geometry (5):
    g0: LineSegment [constr] StartX=1.5e-14 StartY=67.3588 StartZ=0 EndX=0 EndY=64.3588 EndZ=0
    g1: LineSegment [constr] StartX=0 StartY=64.3588 StartZ=0 EndX=10.4 EndY=64.3588 EndZ=0
    g2: LineSegment [constr] StartX=0 StartY=64.3588 StartZ=0 EndX=-10.4 EndY=64.3588 EndZ=0
    g3: Circle CenterX=10.4 CenterY=64.3588 CenterZ=0 NormalX=0 NormalY=0 NormalZ=1 AngleXU=0 Radius=1.5
    g4: Circle CenterX=-10.4 CenterY=64.3588 CenterZ=0 NormalX=0 NormalY=0 NormalZ=1 AngleXU=0 Radius=1.5
  constraints (13):
    c: Distance(g0) = 3
    c: PointOnObject(g0,g-2)
    c: Coincident(g1,g0)
    c: Horizontal(g1)
    c: Coincident(g2,g0)
    c: Horizontal(g2)
    c: DistanceX(g1,g1) = 10.4
    c: Coincident(g3,g1)
    c: Diameter(g4) = 3
    c: Coincident(g4,g2)
    c: Coincident(g0,g-7)
    c: Equal(g1,g2)
    c: Equal(g4,g3)
FEATURE [Part::Extrusion] Extrude047  label="Extrude buchini per fissaggio oled"
  Base = -> Sketch044
  Dir = (1,0,0)
  DirMode = 2
  FaceMakerClass = Part::FaceMakerBullseye
  FaceMakerMode = 3
  LengthFwd = 10
  LengthRev = 0
  Placement = pos=(-186,0,0) rot=(0,0,1;0rad)
  Solid = true
  Symmetric = false
FEATURE [Sketcher::SketchObject] Sketch046  label="scavo 5x5 neopixel"
  ArcFitTolerance = 1e-06
  AttachmentSupport = -> [YZ_Plane002]
  FullyConstrained = true
  MakeInternals = false
  MapMode = 5
  Placement = pos=(0,0,0) rot=(0.57735,0.57735,0.57735;2.0944rad)
  sketch-geometry (4):
    g0: LineSegment StartX=-2.7 StartY=2.7 StartZ=0 EndX=2.7 EndY=2.7 EndZ=0
    g1: LineSegment StartX=2.7 StartY=2.7 StartZ=0 EndX=2.7 EndY=-2.7 EndZ=0
    g2: LineSegment StartX=2.7 StartY=-2.7 StartZ=0 EndX=-2.7 EndY=-2.7 EndZ=0
    g3: LineSegment StartX=-2.7 StartY=-2.7 StartZ=0 EndX=-2.7 EndY=2.7 EndZ=0
  constraints (11):
    c: Horizontal(g0)
    c: Coincident(g1,g0)
    c: Vertical(g1)
    c: Coincident(g2,g1)
    c: Horizontal(g2)
    c: Coincident(g3,g2)
    c: Coincident(g3,g0)
    c: Vertical(g3)
    c: DistanceX(g0,g0) = 5.4
    c: DistanceY(g1,g1) = 5.4
    c: Symmetric(g0,g1,g-1)
FEATURE [Part::Extrusion] Extrude049  label="Extrude scavo 5x5 neopixel"
  Base = -> Sketch046
  Dir = (1,0,0)
  DirMode = 2
  FaceMakerClass = Part::FaceMakerBullseye
  FaceMakerMode = 3
  LengthFwd = 1
  LengthRev = 0
  Solid = true
  Symmetric = false
FEATURE [Sketcher::SketchObject] Sketch047  label="scavo 10x10 neopixel corpo"
  ArcFitTolerance = 1e-06
  AttachmentSupport = -> [YZ_Plane002]
  FullyConstrained = true
  MakeInternals = false
  MapMode = 5
  Placement = pos=(0,0,0) rot=(0.57735,0.57735,0.57735;2.0944rad)
  sketch-geometry (4):
    g0: LineSegment StartX=-5 StartY=5.1 StartZ=0 EndX=5 EndY=5.1 EndZ=0
    g1: LineSegment StartX=5 StartY=5.1 StartZ=0 EndX=5 EndY=-5.1 EndZ=0
    g2: LineSegment StartX=5 StartY=-5.1 StartZ=0 EndX=-5 EndY=-5.1 EndZ=0
    g3: LineSegment StartX=-5 StartY=-5.1 StartZ=0 EndX=-5 EndY=5.1 EndZ=0
  constraints (11):
    c: Horizontal(g0)
    c: Coincident(g1,g0)
    c: Vertical(g1)
    c: Coincident(g2,g1)
    c: Horizontal(g2)
    c: Coincident(g3,g2)
    c: Coincident(g3,g0)
    c: Vertical(g3)
    c: DistanceX(g0,g0) = 10
    c: DistanceY(g1,g1) = 10.2
    c: Symmetric(g0,g2,g-1)
FEATURE [Part::Extrusion] Extrude050  label="Extrude scavo 10x10 neopixel corpo"
  Base = -> Sketch047
  Dir = (1,0,0)
  DirMode = 2
  FaceMakerClass = Part::FaceMakerBullseye
  FaceMakerMode = 3
  LengthFwd = 8
  LengthRev = 0
  Placement = pos=(1,0,0) rot=(0,0,1;0rad)
  Solid = true
  Symmetric = false
FEATURE [Sketcher::SketchObject] Sketch048  label="buco per perno blocco neopixel"
  ArcFitTolerance = 1e-06
  AttachmentSupport = -> [XZ_Plane002]
  FullyConstrained = true
  MakeInternals = false
  MapMode = 5
  Placement = pos=(0,0,0) rot=(1,0,0;1.5708rad)
  sketch-geometry (4):
    g0: LineSegment StartX=3 StartY=1.2 StartZ=0 EndX=3 EndY=-1.2 EndZ=0
    g1: LineSegment StartX=3 StartY=-1.2 StartZ=0 EndX=5.4 EndY=-1.2 EndZ=0
    g2: LineSegment StartX=5.4 StartY=-1.2 StartZ=0 EndX=5.4 EndY=1.2 EndZ=0
    g3: LineSegment StartX=5.4 StartY=1.2 StartZ=0 EndX=3 EndY=1.2 EndZ=0
  constraints (11):
    c: Coincident(g1,g0)
    c: Horizontal(g1)
    c: Coincident(g2,g1)
    c: Vertical(g2)
    c: Coincident(g3,g2)
    c: Coincident(g3,g0)
    c: Horizontal(g3)
    c: DistanceX(g1,g1) = 2.4
    c: DistanceY(g2,g2) = 2.4
    c: Symmetric(g0,g0,g-1)
    c: DistanceX(g-1,g0) = 3
FEATURE [Sketcher::SketchObject] Sketch045  label="blocco principale per neopixel"
  ArcFitTolerance = 1e-06
  AttachmentSupport = -> [XZ_Plane002]
  ExternalGeometry = -> [Sketch048]
  FullyConstrained = true
  MakeInternals = false
  MapMode = 5
  Placement = pos=(0,0,0) rot=(1,0,0;1.5708rad)
  sketch-geometry (6):
    g0: LineSegment StartX=0 StartY=5.1 StartZ=0 EndX=0 EndY=-5.1 EndZ=0
    g1: LineSegment StartX=0 StartY=-5.1 StartZ=0 EndX=3 EndY=-5.1 EndZ=0
    g2: LineSegment StartX=7 StartY=-1.1 StartZ=0 EndX=7 EndY=5.1 EndZ=0
    g3: LineSegment StartX=7 StartY=5.1 StartZ=0 EndX=0 EndY=5.1 EndZ=0
    g4: ArcOfCircle CenterX=3 CenterY=-1.1 CenterZ=0 NormalX=0 NormalY=0 NormalZ=1 AngleXU=0 Radius=4 StartAngle=4.71239 EndAngle=6.28319
    g5: GeomPoint [constr] X=7 Y=-5.1 Z=0
  constraints (15):
    c: Vertical(g0)
    c: Coincident(g1,g0)
    c: Horizontal(g1)
    c: Vertical(g2)
    c: Coincident(g3,g2)
    c: Coincident(g3,g0)
    c: Horizontal(g3)
    c: DistanceY(g0,g0) = 10.2
    c: Symmetric(g0,g0,g-1)
    c: DistanceX(g3,g3) = 7
    c: PointOnObject(g5,g2)
    c: PointOnObject(g5,g1)
    c: Tangent(g2,g4) = -1.5708
    c: Tangent(g1,g4) = -1.5708
    c: DistanceX(g-3,g1) = 0
FEATURE [Part::Extrusion] Extrude048  label="Extrude blocco principale per neopixel"
  Base = -> Sketch045
  Dir = (0,-1,2e-16)
  DirMode = 2
  FaceMakerClass = Part::FaceMakerBullseye
  FaceMakerMode = 3
  LengthFwd = 17
  LengthRev = 0
  Solid = true
  Symmetric = true
FEATURE [Part::Extrusion] Extrude051  label="Extrude buco per perno blocco neopixel"
  Base = -> Sketch048
  Dir = (0,-1,2e-16)
  DirMode = 2
  FaceMakerClass = Part::FaceMakerBullseye
  FaceMakerMode = 3
  LengthFwd = 17
  LengthRev = 0
  Solid = true
  Symmetric = true
FEATURE [Sketcher::SketchObject] Sketch049  label="rinforzi esterni per corpo neopoixel"
  ArcFitTolerance = 1e-06
  AttachmentSupport = -> [XZ_Plane002]
  ExternalGeometry = -> [Sketch045]
  FullyConstrained = true
  MakeInternals = false
  MapMode = 5
  Placement = pos=(0,0,0) rot=(1,0,0;1.5708rad)
  sketch-geometry (8):
    g0: LineSegment StartX=1 StartY=-4.1 StartZ=0 EndX=2 EndY=-4.1 EndZ=0
    g1: LineSegment StartX=2 StartY=-4.1 StartZ=0 EndX=2 EndY=-5.1 EndZ=0
    g2: LineSegment StartX=2 StartY=-5.1 StartZ=0 EndX=1 EndY=-5.1 EndZ=0
    g3: LineSegment StartX=1 StartY=-5.1 StartZ=0 EndX=1 EndY=-4.1 EndZ=0
    g4: LineSegment StartX=1 StartY=5.1 StartZ=0 EndX=2 EndY=5.1 EndZ=0
    g5: LineSegment StartX=2 StartY=5.1 StartZ=0 EndX=2 EndY=4.1 EndZ=0
    g6: LineSegment StartX=2 StartY=4.1 StartZ=0 EndX=1 EndY=4.1 EndZ=0
    g7: LineSegment StartX=1 StartY=4.1 StartZ=0 EndX=1 EndY=5.1 EndZ=0
  constraints (24):
    c: Horizontal(g0)
    c: Coincident(g1,g0)
    c: Vertical(g1)
    c: Coincident(g2,g1)
    c: Horizontal(g2)
    c: Coincident(g3,g2)
    c: Coincident(g3,g0)
    c: Vertical(g3)
    c: Horizontal(g4)
    c: Coincident(g5,g4)
    c: Vertical(g5)
    c: Coincident(g6,g5)
    c: Horizontal(g6)
    c: Coincident(g7,g6)
    c: Coincident(g7,g4)
    c: Vertical(g7)
    c: DistanceX(g4,g4) = 1
    c: DistanceY(g5,g5) = 1
    c: DistanceX(g0,g0) = 1
    c: DistanceY(g1,g1) = 1
    c: DistanceX(g-3,g4) = 1
    c: DistanceY(g-3,g4) = 0
    c: DistanceX(g-4,g2) = 1
    c: DistanceY(g2,g-4) = 0
FEATURE [Part::Extrusion] Extrude052  label="Extrude rinforzi esterni per corpo neopoixel"
  Base = -> Sketch049
  Dir = (0,-1,2e-16)
  DirMode = 2
  FaceMakerClass = Part::FaceMakerBullseye
  FaceMakerMode = 3
  LengthFwd = 17
  LengthRev = 0
  Solid = true
  Symmetric = true
FEATURE [Part::Cut] Cut030
  Base = -> Extrude048
  Refine = true
  Tool = -> Extrude050
FEATURE [Part::Cut] Cut031
  Base = -> Cut030
  Refine = true
  Tool = -> Extrude049
FEATURE [Part::Cut] Cut032
  Base = -> Cut031
  Refine = true
  Tool = -> Extrude051
FEATURE [Part::MultiFuse] Fusion001  label="fusion neopixel"
  Refine = true
  Shapes = -> [Cut032,Extrude052]
FEATURE [Sketcher::SketchObject] Sketch052  label="scavo saldature driver solenoide"
  ArcFitTolerance = 1e-06
  AttachmentSupport = -> [XZ_Plane]
  ExternalGeometry = -> [Sketch038]
  FullyConstrained = true
  MakeInternals = false
  MapMode = 5
  Placement = pos=(0,0,0) rot=(1,0,0;1.5708rad)
  sketch-geometry (4):
    g0: LineSegment StartX=-196.56 StartY=-9.74706 StartZ=0 EndX=-198.25 EndY=-13.3723 EndZ=0
    g1: LineSegment StartX=-198.25 StartY=-13.3723 StartZ=0 EndX=-196.8 EndY=-14.0485 EndZ=0
    g2: LineSegment StartX=-196.8 StartY=-14.0485 StartZ=0 EndX=-195.11 EndY=-10.4232 EndZ=0
    g3: LineSegment StartX=-195.11 StartY=-10.4232 StartZ=0 EndX=-196.56 EndY=-9.74706 EndZ=0
  constraints (11):
    c: Coincident(g1,g0)
    c: Coincident(g2,g1)
    c: Coincident(g3,g2)
    c: Coincident(g3,g0)
    c: Parallel(g2,g0)
    c: Perpendicular(g2,g3)
    c: Perpendicular(g1,g2,g1) = 1.5708
    c: Parallel(g2,g-3)
    c: Distance(g2) = 4
    c: Distance(g3) = 1.6
    c: Coincident(g2,g-3)
FEATURE [Part::Extrusion] Extrude055  label="Extrude scavo saldature driver solenoide"
  Base = -> Sketch052
  Dir = (0,-1,2e-16)
  DirMode = 2
  FaceMakerClass = Part::FaceMakerBullseye
  FaceMakerMode = 3
  LengthFwd = 6
  LengthRev = 0
  Solid = true
  Symmetric = true
FEATURE [Sketcher::SketchObject] Sketch053  label="scavo saldature rumble"
  ArcFitTolerance = 1e-06
  AttachmentSupport = -> [XZ_Plane]
  ExternalGeometry = -> [Sketch019]
  FullyConstrained = true
  MakeInternals = false
  MapMode = 5
  Placement = pos=(0,0,0) rot=(1,0,0;1.5708rad)
  sketch-geometry (4):
    g0: LineSegment StartX=-165.31 StartY=-44.1173 StartZ=0 EndX=-166.547 EndY=-47.9216 EndZ=0
    g1: LineSegment StartX=-166.547 StartY=-47.9216 StartZ=0 EndX=-165.405 EndY=-48.2924 EndZ=0
    g2: LineSegment StartX=-165.405 StartY=-48.2924 StartZ=0 EndX=-164.169 EndY=-44.4881 EndZ=0
    g3: LineSegment StartX=-164.169 StartY=-44.4881 StartZ=0 EndX=-165.31 EndY=-44.1173 EndZ=0
  constraints (11):
    c: Coincident(g1,g0)
    c: Coincident(g2,g1)
    c: Coincident(g3,g2)
    c: Coincident(g3,g0)
    c: Parallel(g0,g2)
    c: Perpendicular(g3,g0)
    c: Perpendicular(g1,g0)
    c: Parallel(g0,g-3)
    c: Distance(g0) = 4
    c: Distance(g1) = 1.2
    c: Coincident(g0,g-3)
FEATURE [Part::Extrusion] Extrude056  label="Extrude scavo saldature rumble"
  Base = -> Sketch053
  Dir = (0,-1,2e-16)
  DirMode = 2
  FaceMakerClass = Part::FaceMakerBullseye
  FaceMakerMode = 3
  LengthFwd = 8.4
  LengthRev = 0
  Solid = true
  Symmetric = true
FEATURE [Part::Cone] Cone  label="Cono"
  Angle = 180
  AttacherType = Attacher::AttachEngine3D
  Height = 15
  Placement = pos=(-176,0,-82.43) rot=(0,0,1;-1.5708rad)
  Radius1 = 12.6
  Radius2 = 10.5
FEATURE [Sketcher::SketchObject] Sketch054  label="scavo saldature alimentatore connettore USB"
  ArcFitTolerance = 1e-06
  AttachmentSupport = -> [XZ_Plane]
  ExternalGeometry = -> [Sketch037]
  FullyConstrained = true
  MakeInternals = false
  MapMode = 5
  Placement = pos=(0,0,0) rot=(1,0,0;1.5708rad)
  sketch-geometry (4):
    g0: LineSegment StartX=-209.575 StartY=-80.4316 StartZ=0 EndX=-210.375 EndY=-80.4316 EndZ=0
    g1: LineSegment StartX=-210.375 StartY=-80.4316 StartZ=0 EndX=-210.375 EndY=-72.4316 EndZ=0
    g2: LineSegment StartX=-210.375 StartY=-72.4316 StartZ=0 EndX=-209.575 EndY=-72.4316 EndZ=0
    g3: LineSegment StartX=-209.575 StartY=-72.4316 StartZ=0 EndX=-209.575 EndY=-80.4316 EndZ=0
  constraints (11):
    c: Horizontal(g0)
    c: Coincident(g1,g0)
    c: Vertical(g1)
    c: Coincident(g2,g1)
    c: Horizontal(g2)
    c: Coincident(g3,g2)
    c: Coincident(g3,g0)
    c: Vertical(g3)
    c: DistanceX(g0,g0) = 0.8
    c: DistanceY(g3,g3) = 8
    c: Coincident(g0,g-4)
FEATURE [Part::Extrusion] Extrude057  label="Extrude scavo saldature alimentatore connettore USB"
  Base = -> Sketch054
  Dir = (0,-1,2e-16)
  DirMode = 2
  FaceMakerClass = Part::FaceMakerBullseye
  FaceMakerMode = 3
  LengthFwd = 11
  LengthRev = 0
  Solid = true
  Symmetric = true
FEATURE [Sketcher::SketchObject] Sketch055  label="buco interno per micro switch"
  ArcFitTolerance = 1e-06
  AttachmentSupport = -> [XZ_Plane]
  ExternalGeometry = -> [Sketch]
  FullyConstrained = true
  MakeInternals = false
  MapMode = 5
  Placement = pos=(0,0,0) rot=(1,0,0;1.5708rad)
  sketch-geometry (11):
    g0: LineSegment [constr] StartX=-194.483 StartY=34.2854 StartZ=0 EndX=-196.022 EndY=30.0568 EndZ=0
    g1: LineSegment [constr] StartX=-196.022 StartY=30.0568 StartZ=0 EndX=-197.561 EndY=25.8282 EndZ=0
    g2: LineSegment [constr] StartX=-196.022 StartY=30.0568 StartZ=0 EndX=-194.143 EndY=29.3727 EndZ=0
    g3: LineSegment [constr] StartX=-196.022 StartY=30.0568 StartZ=0 EndX=-197.902 EndY=30.7408 EndZ=0
    g4: LineSegment StartX=-196.362 StartY=34.9694 StartZ=0 EndX=-192.604 EndY=33.6014 EndZ=0
    g5: LineSegment StartX=-199.441 StartY=26.5122 StartZ=0 EndX=-195.682 EndY=25.1441 EndZ=0
    g6: LineSegment StartX=-192.604 StartY=33.6014 StartZ=0 EndX=-195.682 EndY=25.1441 EndZ=0
    g7: LineSegment StartX=-196.362 StartY=34.9694 StartZ=0 EndX=-199.441 EndY=26.5122 EndZ=0
    g8: GeomPoint [constr] X=-187.821 Y=29.2 Z=0
    g9: LineSegment [constr] StartX=-188.505 StartY=27.3206 StartZ=0 EndX=-196.022 EndY=30.0568 EndZ=0
    g10: LineSegment [constr] StartX=-187.821 StartY=29.2 StartZ=0 EndX=-188.505 EndY=27.3206 EndZ=0
  constraints (27):
    c: Coincident(g2,g0)
    c: Parallel(g0,g-3)
    c: Tangent(g1,g0) = -1.5708
    c: Perpendicular(g0,g2)
    c: Tangent(g2,g3)
    c: Distance(g0,g1) = 9
    c: Equal(g0,g1)
    c: Distance(g3,g2) = 4
    c: Equal(g2,g3)
    c: Parallel(g3,g4)
    c: Symmetric(g4,g4,g0)
    c: Parallel(g6,g1)
    c: Parallel(g7,g1)
    c: Symmetric(g6,g6,g2)
    c: Symmetric(g5,g5,g1)
    c: Symmetric(g7,g7,g3)
    c: Coincident(g7,g4)
    c: Coincident(g6,g4)
    c: Coincident(g5,g6)
    c: Symmetric(g-3,g-3,g8)
    c: Perpendicular(g-3,g9)
    c: Distance(g9) = 8
    c: Coincident(g3,g9)
    c: Coincident(g10,g8)
    c: Parallel(g10,g-3)
    c: Distance(g10) = 2
    c: Coincident(g10,g9)
FEATURE [Part::Extrusion] Extrude058  label="Extrude buco interno per micro switch sinistro"
  Base = -> Sketch055
  Dir = (0,-1,2e-16)
  DirMode = 2
  FaceMakerClass = Part::FaceMakerBullseye
  FaceMakerMode = 3
  LengthFwd = 9
  LengthRev = 0
  Placement = pos=(0,10.6,0) rot=(0,0,1;0rad)
  Solid = true
  Symmetric = false
FEATURE [Sketcher::SketchObject] Sketch056  label="buco esterno per micro switch"
  ArcFitTolerance = 1e-06
  AttachmentSupport = -> [XZ_Plane]
  ExternalGeometry = -> [Sketch055]
  FullyConstrained = true
  MakeInternals = false
  MapMode = 5
  Placement = pos=(0,0,0) rot=(1,0,0;1.5708rad)
  sketch-geometry (17):
    g0: GeomPoint [constr] X=-194.143 Y=29.3727 Z=0
    g1: GeomPoint [constr] X=-194.483 Y=34.2854 Z=0
    g2: GeomPoint [constr] X=-197.902 Y=30.7408 Z=0
    g3: GeomPoint [constr] X=-197.561 Y=25.8282 Z=0
    g4: GeomPoint [constr] X=-196.022 Y=30.0568 Z=0
    g5: LineSegment [constr] StartX=-194.483 StartY=34.2854 StartZ=0 EndX=-196.022 EndY=30.0568 EndZ=0
    g6: LineSegment [constr] StartX=-196.022 StartY=30.0568 StartZ=0 EndX=-197.561 EndY=25.8282 EndZ=0
    g7: LineSegment [constr] StartX=-197.902 StartY=30.7408 StartZ=0 EndX=-196.022 EndY=30.0568 EndZ=0
    g8: LineSegment [constr] StartX=-196.022 StartY=30.0568 StartZ=0 EndX=-194.143 EndY=29.3727 EndZ=0
    g9: LineSegment [constr] StartX=-195.338 StartY=31.9362 StartZ=0 EndX=-196.022 EndY=30.0568 EndZ=0
    g10: LineSegment [constr] StartX=-196.022 StartY=30.0568 StartZ=0 EndX=-196.706 EndY=28.1774 EndZ=0
    g11: LineSegment [constr] StartX=-196.022 StartY=30.0568 StartZ=0 EndX=-196.821 EndY=30.3475 EndZ=0
    g12: LineSegment [constr] StartX=-196.022 StartY=30.0568 StartZ=0 EndX=-195.223 EndY=29.7661 EndZ=0
    g13: LineSegment StartX=-194.539 StartY=31.6454 StartZ=0 EndX=-195.907 EndY=27.8867 EndZ=0
    g14: LineSegment StartX=-196.137 StartY=32.2269 StartZ=0 EndX=-197.505 EndY=28.4681 EndZ=0
    g15: LineSegment StartX=-196.137 StartY=32.2269 StartZ=0 EndX=-194.539 EndY=31.6454 EndZ=0
    g16: LineSegment StartX=-197.505 StartY=28.4681 StartZ=0 EndX=-195.907 EndY=27.8867 EndZ=0
  constraints (34):
    c: Symmetric(g-5,g-5,g1)
    c: Symmetric(g-5,g-6,g0)
    c: Symmetric(g-6,g-6,g3)
    c: Symmetric(g-5,g-6,g2)
    c: Coincident(g5,g1)
    c: Coincident(g5,g4)
    c: Coincident(g6,g4)
    c: Coincident(g6,g3)
    c: Equal(g5,g6)
    c: Coincident(g7,g2)
    c: Coincident(g7,g4)
    c: Coincident(g8,g4)
    c: Coincident(g8,g0)
    c: Equal(g7,g8)
    c: Coincident(g11,g9)
    c: Coincident(g12,g9)
    c: Tangent(g10,g9) = -1.5708
    c: Perpendicular(g11,g9)
    c: Parallel(g9,g-4)
    c: Equal(g9,g10)
    c: Parallel(g12,g11)
    c: Equal(g11,g12)
    c: Distance(g11,g12) = 1.7
    c: Distance(g9,g10) = 4
    c: Symmetric(g13,g13,g12)
    c: Parallel(g13,g9)
    c: Symmetric(g14,g14,g11)
    c: Symmetric(g15,g15,g9)
    c: Parallel(g15,g11)
    c: Symmetric(g16,g16,g10)
    c: Coincident(g16,g14)
    c: Coincident(g15,g14)
    c: Coincident(g13,g15)
    c: Coincident(g9,g4)
FEATURE [Part::Extrusion] Extrude059  label="Extrude buco esterno per micro switch sinistro"
  Base = -> Sketch056
  Dir = (0,-1,2e-16)
  DirMode = 2
  FaceMakerClass = Part::FaceMakerBullseye
  FaceMakerMode = 3
  LengthFwd = 2
  LengthRev = 0
  Placement = pos=(0,12.6,0) rot=(0,0,1;0rad)
  Solid = true
  Symmetric = false
FEATURE [Sketcher::SketchObject] Sketch057  label="buco interno per SWITCH"
  ArcFitTolerance = 1e-06
  AttachmentSupport = -> [XZ_Plane]
  ExternalGeometry = -> [Sketch]
  FullyConstrained = true
  MakeInternals = false
  MapMode = 5
  Placement = pos=(0,0,0) rot=(1,0,0;1.5708rad)
  sketch-geometry (10):
    g0: GeomPoint [constr] X=-187.821 Y=29.2 Z=0
    g1: LineSegment [constr] StartX=-188.505 StartY=27.3206 StartZ=0 EndX=-193.203 EndY=29.0307 EndZ=0
    g2: LineSegment [constr] StartX=-190.809 StartY=35.6086 StartZ=0 EndX=-195.597 EndY=22.4529 EndZ=0
    g3: GeomPoint [constr] X=-193.203 Y=29.0307 Z=0
    g4: LineSegment [constr] StartX=-196.492 StartY=30.2278 StartZ=0 EndX=-189.914 EndY=27.8336 EndZ=0
    g5: LineSegment StartX=-194.098 StartY=36.8056 StartZ=0 EndX=-187.52 EndY=34.4115 EndZ=0
    g6: LineSegment StartX=-194.098 StartY=36.8056 StartZ=0 EndX=-198.886 EndY=23.6499 EndZ=0
    g7: LineSegment StartX=-187.52 StartY=34.4115 StartZ=0 EndX=-192.308 EndY=21.2558 EndZ=0
    g8: LineSegment StartX=-198.886 StartY=23.6499 StartZ=0 EndX=-192.308 EndY=21.2558 EndZ=0
    g9: LineSegment [constr] StartX=-187.821 StartY=29.2 StartZ=0 EndX=-188.505 EndY=27.3206 EndZ=0
  constraints (23):
    c: Symmetric(g-3,g-3,g0)
    c: Perpendicular(g1,g-3)
    c: Parallel(g2,g-3)
    c: Symmetric(g2,g2,g3)
    c: Perpendicular(g2,g4)
    c: Symmetric(g4,g4,g3)
    c: Distance(g2) = 14
    c: Distance(g4) = 7
    c: Distance(g1) = 5
    c: Parallel(g5,g4)
    c: Parallel(g7,g2)
    c: Symmetric(g5,g5,g2)
    c: Symmetric(g6,g6,g4)
    c: Symmetric(g7,g7,g4)
    c: Symmetric(g8,g8,g2)
    c: Coincident(g6,g5)
    c: Coincident(g7,g5)
    c: Coincident(g8,g7)
    c: Coincident(g3,g1)
    c: Coincident(g9,g0)
    c: Parallel(g9,g-3)
    c: Distance(g9) = 2
    c: Coincident(g1,g9)
FEATURE [Sketcher::SketchObject] Sketch058  label="buco esterno per SWITCH"
  ArcFitTolerance = 1e-06
  AttachmentSupport = -> [XZ_Plane]
  ExternalGeometry = -> [Sketch057]
  FullyConstrained = true
  MakeInternals = false
  MapMode = 5
  Placement = pos=(0,0,0) rot=(1,0,0;1.5708rad)
  sketch-geometry (12):
    g0: GeomPoint [constr] X=-190.809 Y=35.6086 Z=0
    g1: GeomPoint [constr] X=-196.492 Y=30.2278 Z=0
    g2: GeomPoint [constr] X=-189.914 Y=27.8336 Z=0
    g3: GeomPoint [constr] X=-195.597 Y=22.4529 Z=0
    g4: GeomPoint [constr] X=-193.203 Y=29.0307 Z=0
    g5: LineSegment [constr] StartX=-192.006 StartY=32.3196 StartZ=0 EndX=-194.4 EndY=25.7418 EndZ=0
    g6: GeomPoint [constr] X=-193.203 Y=29.0307 Z=0
    g7: LineSegment [constr] StartX=-195.082 StartY=29.7148 StartZ=0 EndX=-191.324 EndY=28.3467 EndZ=0
    g8: LineSegment StartX=-193.885 StartY=33.0037 StartZ=0 EndX=-190.127 EndY=31.6356 EndZ=0
    g9: LineSegment StartX=-190.127 StartY=31.6356 StartZ=0 EndX=-192.521 EndY=25.0578 EndZ=0
    g10: LineSegment StartX=-196.28 StartY=26.4258 StartZ=0 EndX=-192.521 EndY=25.0578 EndZ=0
    g11: LineSegment StartX=-193.885 StartY=33.0037 StartZ=0 EndX=-196.28 EndY=26.4258 EndZ=0
  constraints (21):
    c: Symmetric(g-6,g-6,g3)
    c: Symmetric(g-4,g-6,g2)
    c: Symmetric(g-5,g-4,g0)
    c: Symmetric(g-5,g-6,g1)
    c: Symmetric(g1,g2,g4)
    c: Parallel(g5,g-4)
    c: Symmetric(g5,g5,g6)
    c: Perpendicular(g7,g5)
    c: Symmetric(g7,g7,g6)
    c: Distance(g5) = 7
    c: Distance(g7) = 4
    c: Parallel(g8,g7)
    c: Parallel(g11,g5)
    c: Symmetric(g8,g8,g5)
    c: Symmetric(g9,g9,g7)
    c: Symmetric(g10,g10,g5)
    c: Symmetric(g11,g11,g7)
    c: Coincident(g11,g8)
    c: Coincident(g9,g8)
    c: Coincident(g9,g10)
    c: Coincident(g6,g4)
FEATURE [Part::Extrusion] Extrude060  label="Extrude buco interno per SWITCH destro"
  Base = -> Sketch057
  Dir = (0,-1,2e-16)
  DirMode = 2
  FaceMakerClass = Part::FaceMakerBullseye
  FaceMakerMode = 3
  LengthFwd = 13.2
  LengthRev = 0
  Placement = pos=(0,2.6,0) rot=(0,0,1;0rad)
  Solid = true
  Symmetric = false
FEATURE [Part::Extrusion] Extrude061  label="Extrude buco esterno per SWITCH destro"
  Base = -> Sketch058
  Dir = (0,-1,2e-16)
  DirMode = 2
  FaceMakerClass = Part::FaceMakerBullseye
  FaceMakerMode = 3
  LengthFwd = 2
  LengthRev = 0
  Placement = pos=(0,-10.6,0) rot=(0,0,1;0rad)
  Solid = true
  Symmetric = false
FEATURE [Sketcher::SketchObject] Sketch059  label="buco per spazio introduzione SWITCH"
  ArcFitTolerance = 1e-06
  AttachmentSupport = -> [XZ_Plane]
  ExternalGeometry = -> [Sketch057,Sketch010]
  FullyConstrained = true
  MakeInternals = false
  MapMode = 5
  Placement = pos=(0,0,0) rot=(1,0,0;1.5708rad)
  sketch-geometry (8):
    g0: LineSegment [constr] StartX=-201.368 StartY=36.3521 StartZ=0 EndX=-195.094 EndY=34.0687 EndZ=0
    g1: LineSegment [constr] StartX=-194.098 StartY=36.8056 StartZ=0 EndX=-195.094 EndY=34.0687 EndZ=0
    g2: LineSegment StartX=-198.658 StartY=24.2771 StartZ=0 EndX=-199.654 EndY=21.5401 EndZ=0
    g3: LineSegment StartX=-199.654 StartY=21.5401 StartZ=0 EndX=-181.196 EndY=14.822 EndZ=0
    g4: LineSegment StartX=-181.196 StartY=14.822 StartZ=0 EndX=-180.2 EndY=17.559 EndZ=0
    g5: LineSegment StartX=-180.2 StartY=17.559 StartZ=0 EndX=-198.658 EndY=24.2771 EndZ=0
    g6: LineSegment [constr] StartX=-204.932 StartY=26.5605 StartZ=0 EndX=-198.658 EndY=24.2771 EndZ=0
    g7: LineSegment [constr] StartX=-198.658 StartY=24.2771 StartZ=0 EndX=-199.654 EndY=21.5401 EndZ=0
  constraints (20):
    c: Parallel(g1,g-3)
    c: Parallel(g0,g-4)
    c: Coincident(g0,g-4)
    c: Coincident(g1,g-3)
    c: Coincident(g0,g1)
    c: Coincident(g3,g2)
    c: Coincident(g4,g3)
    c: Coincident(g5,g4)
    c: Coincident(g5,g2)
    c: Parallel(g5,g-5)
    c: Parallel(g3,g-5)
    c: Parallel(g4,g-6)
    c: DistanceX(g-6,g4) = 0
    c: Coincident(g6,g-5)
    c: Equal(g6,g0)
    c: Coincident(g7,g6)
    c: Equal(g7,g1)
    c: Tangent(g7,g-3)
    c: Coincident(g2,g6)
    c: Coincident(g2,g7)
FEATURE [Part::Extrusion] Extrude062  label="Extrude buco per spazio introduzione SWITCH"
  Base = -> Sketch059
  Dir = (0,-1,2e-16)
  DirMode = 2
  FaceMakerClass = Part::FaceMakerBullseye
  FaceMakerMode = 3
  LengthFwd = 13.2
  LengthRev = 0
  Solid = true
  Symmetric = true
FEATURE [Part::Extrusion] Extrude063  label="Extrude buco interno per SWITCH sinistro"
  Base = -> Sketch057
  Dir = (0,-1,2e-16)
  DirMode = 2
  FaceMakerClass = Part::FaceMakerBullseye
  FaceMakerMode = 3
  LengthFwd = 13.2
  LengthRev = 0
  Placement = pos=(0,10.6,0) rot=(0,0,1;0rad)
  Solid = true
  Symmetric = false
FEATURE [Part::Extrusion] Extrude064  label="Extrude buco esterno per SWITCH sinistro"
  Base = -> Sketch058
  Dir = (0,-1,2e-16)
  DirMode = 2
  FaceMakerClass = Part::FaceMakerBullseye
  FaceMakerMode = 3
  LengthFwd = 2
  LengthRev = 0
  Placement = pos=(0,12.6,0) rot=(0,0,1;0rad)
  Solid = true
  Symmetric = false
FEATURE [Sketcher::SketchObject] Sketch060  label="prova spazio switch"
  ArcFitTolerance = 1e-06
  AttachmentSupport = -> [XY_Plane003]
  FullyConstrained = true
  MakeInternals = false
  MapMode = 5
  sketch-geometry (12):
    g0: LineSegment StartX=-7.5 StartY=10 StartZ=0 EndX=-7.5 EndY=-10 EndZ=0
    g1: LineSegment StartX=-7.5 StartY=-10 StartZ=0 EndX=7.5 EndY=-10 EndZ=0
    g2: LineSegment StartX=7.5 StartY=-10 StartZ=0 EndX=7.5 EndY=10 EndZ=0
    g3: LineSegment StartX=7.5 StartY=10 StartZ=0 EndX=-7.5 EndY=10 EndZ=0
    g4: GeomPoint [constr] X=0 Y=0 Z=0
    g5: LineSegment StartX=-2.95 StartY=-5.55 StartZ=0 EndX=2.95 EndY=-5.55 EndZ=0
    g6: LineSegment StartX=2.95 StartY=-5.55 StartZ=0 EndX=2.95 EndY=5.55 EndZ=0
    g7: LineSegment StartX=2.95 StartY=5.55 StartZ=0 EndX=-2.95 EndY=5.55 EndZ=0
    g8: LineSegment StartX=-2.95 StartY=5.55 StartZ=0 EndX=-2.95 EndY=-5.55 EndZ=0
    g9: GeomPoint [constr] X=0 Y=0 Z=0
    g10: Circle CenterX=0 CenterY=7.75 CenterZ=0 NormalX=0 NormalY=0 NormalZ=1 AngleXU=0 Radius=1.6
    g11: Circle CenterX=0 CenterY=-7.75 CenterZ=0 NormalX=0 NormalY=0 NormalZ=1 AngleXU=0 Radius=1.6
  constraints (29):
    c: Coincident(g0,g1)
    c: Coincident(g1,g2)
    c: Coincident(g2,g3)
    c: Coincident(g3,g0)
    c: Vertical(g0)
    c: Vertical(g2)
    c: Horizontal(g1)
    c: Horizontal(g3)
    c: Symmetric(g2,g0,g4)
    c: Coincident(g4,g-1)
    c: Distance(g3) = 15
    c: Distance(g2) = 20
    c: Coincident(g5,g6)
    c: Coincident(g6,g7)
    c: Coincident(g7,g8)
    c: Coincident(g8,g5)
    c: Horizontal(g5)
    c: Horizontal(g7)
    c: Vertical(g6)
    c: Vertical(g8)
    c: Symmetric(g7,g5,g9)
    c: Coincident(g9,g4)
    c: Distance(g7) = 5.9
    c: Distance(g6) = 11.1
    c: Diameter(g10) = 3.2
    c: Equal(g10,g11)
    c: Symmetric(g10,g11,g-1)
    c: PointOnObject(g10,g-2)
    c: Distance(g10,g11) = 15.5
FEATURE [Part::Extrusion] Extrude065  label="Extrude prova spazio switch"
  Base = -> Sketch060
  Dir = (0,0,1)
  DirMode = 2
  FaceMakerClass = Part::FaceMakerBullseye
  FaceMakerMode = 3
  LengthFwd = 5
  LengthRev = 0
  Solid = true
  Symmetric = false
FEATURE [Sketcher::SketchObject] Sketch061  label="struttura esterna blocco switch"
  ArcFitTolerance = 1e-06
  AttachmentSupport = -> [XZ_Plane003]
  FullyConstrained = true
  MakeInternals = false
  MapMode = 5
  Placement = pos=(0,0,0) rot=(1,0,0;1.5708rad)
  sketch-geometry (5):
    g0: LineSegment StartX=-1 StartY=-5.1 StartZ=0 EndX=1 EndY=-5.1 EndZ=0
    g1: LineSegment StartX=1 StartY=-5.1 StartZ=0 EndX=1 EndY=5.1 EndZ=0
    g2: LineSegment StartX=1 StartY=5.1 StartZ=0 EndX=-1 EndY=5.1 EndZ=0
    g3: LineSegment StartX=-1 StartY=5.1 StartZ=0 EndX=-1 EndY=-5.1 EndZ=0
    g4: GeomPoint [constr] X=0 Y=0 Z=0
  constraints (12):
    c: Coincident(g0,g1)
    c: Coincident(g1,g2)
    c: Coincident(g2,g3)
    c: Coincident(g3,g0)
    c: Horizontal(g0)
    c: Horizontal(g2)
    c: Vertical(g1)
    c: Vertical(g3)
    c: Symmetric(g2,g0,g4)
    c: Distance(g1,g3) = 2
    c: Distance(g0,g2) = 10.2
    c: Coincident(g4,g-1)
FEATURE [Part::Extrusion] Extrude066  label="Extrude struttura esterna blocco switch"
  Base = -> Sketch061
  Dir = (0,-1,2e-16)
  DirMode = 2
  FaceMakerClass = Part::FaceMakerBullseye
  FaceMakerMode = 3
  LengthFwd = 16.8
  LengthRev = 0
  Solid = true
  Symmetric = true
FEATURE [Sketcher::SketchObject] Sketch062  label="struttura interna blocco switch"
  ArcFitTolerance = 1e-06
  AttachmentSupport = -> [XZ_Plane003]
  ExternalGeometry = -> [Sketch061]
  FullyConstrained = true
  MakeInternals = false
  MapMode = 5
  Placement = pos=(0,0,0) rot=(1,0,0;1.5708rad)
  sketch-geometry (5):
    g0: LineSegment StartX=-1 StartY=3.1 StartZ=0 EndX=-1 EndY=-3.1 EndZ=0
    g1: LineSegment StartX=-1 StartY=-3.1 StartZ=0 EndX=1 EndY=-3.1 EndZ=0
    g2: LineSegment StartX=1 StartY=-3.1 StartZ=0 EndX=1 EndY=3.1 EndZ=0
    g3: LineSegment StartX=1 StartY=3.1 StartZ=0 EndX=-1 EndY=3.1 EndZ=0
    g4: GeomPoint [constr] X=0 Y=0 Z=0
  constraints (12):
    c: Coincident(g0,g1)
    c: Coincident(g1,g2)
    c: Coincident(g2,g3)
    c: Coincident(g3,g0)
    c: Vertical(g0)
    c: Vertical(g2)
    c: Horizontal(g1)
    c: Horizontal(g3)
    c: Symmetric(g2,g0,g4)
    c: Coincident(g4,g-1)
    c: Distance(g0) = 6.2
    c: Equal(g3,g-3)
FEATURE [Part::Extrusion] Extrude067  label="Extrude struttura interna blocco switch"
  Base = -> Sketch062
  Dir = (0,-1,2e-16)
  DirMode = 2
  FaceMakerClass = Part::FaceMakerBullseye
  FaceMakerMode = 3
  LengthFwd = 12.8
  LengthRev = 0
  Solid = true
  Symmetric = true
FEATURE [Part::Cut] Cut036  label="struttura blocco switch"
  Base = -> Extrude066
  Refine = true
  Tool = -> Extrude067
FEATURE [Sketcher::SketchObject] Sketch063  label="blocchi tra switch"
  ArcFitTolerance = 1e-06
  AttachmentSupport = -> [XZ_Plane003]
  ExternalGeometry = -> [Sketch061,Sketch062]
  FullyConstrained = true
  MakeInternals = false
  MapMode = 5
  Placement = pos=(0,0,0) rot=(1,0,0;1.5708rad)
  sketch-geometry (8):
    g0: LineSegment StartX=-3 StartY=5.1 StartZ=0 EndX=-1 EndY=5.1 EndZ=0
    g1: LineSegment StartX=-1 StartY=5.1 StartZ=0 EndX=-1 EndY=3.1 EndZ=0
    g2: LineSegment StartX=-1 StartY=3.1 StartZ=0 EndX=-3 EndY=3.1 EndZ=0
    g3: LineSegment StartX=-3 StartY=3.1 StartZ=0 EndX=-3 EndY=5.1 EndZ=0
    g4: LineSegment StartX=-3 StartY=-3.1 StartZ=0 EndX=-1 EndY=-3.1 EndZ=0
    g5: LineSegment StartX=-1 StartY=-3.1 StartZ=0 EndX=-1 EndY=-5.1 EndZ=0
    g6: LineSegment StartX=-1 StartY=-5.1 StartZ=0 EndX=-3 EndY=-5.1 EndZ=0
    g7: LineSegment StartX=-3 StartY=-5.1 StartZ=0 EndX=-3 EndY=-3.1 EndZ=0
  constraints (20):
    c: Horizontal(g0)
    c: Coincident(g1,g0)
    c: Coincident(g2,g1)
    c: Horizontal(g2)
    c: Coincident(g3,g2)
    c: Coincident(g3,g0)
    c: Vertical(g3)
    c: Horizontal(g4)
    c: Coincident(g5,g4)
    c: Coincident(g6,g5)
    c: Horizontal(g6)
    c: Coincident(g7,g6)
    c: Coincident(g7,g4)
    c: Vertical(g7)
    c: Coincident(g0,g-4)
    c: Coincident(g1,g-5)
    c: Coincident(g4,g-6)
    c: Coincident(g5,g-7)
    c: Distance(g0) = 2
    c: Distance(g4) = 2
FEATURE [PartDesign::Body] Body003  label="blocco switch e neopixel"
  AllowCompound = false
  Group = -> [Sketch060,Sketch061,Sketch062,Sketch063]
  Origin = -> Origin003
FEATURE [Part::Extrusion] Extrude068  label="Extrude blocchi tra switch"
  Base = -> Sketch063
  Dir = (0,-1,2e-16)
  DirMode = 2
  FaceMakerClass = Part::FaceMakerBullseye
  FaceMakerMode = 3
  LengthFwd = 7.6
  LengthRev = 0
  Solid = true
  Symmetric = true
FEATURE [Part::MultiFuse] Fusion002  label="Fusion blocco switch"
  Refine = true
  Shapes = -> [Cut036,Extrude068]
FEATURE [Sketcher::SketchObject] Sketch066  label="piano per rampino"
  ArcFitTolerance = 1e-06
  AttachmentSupport = -> [XZ_Plane002]
  ExternalGeometry = -> [Sketch045]
  FullyConstrained = true
  MakeInternals = false
  MapMode = 5
  Placement = pos=(0,0,0) rot=(1,0,0;1.5708rad)
  sketch-geometry (4):
    g0: LineSegment StartX=5.4 StartY=5.1 StartZ=0 EndX=5.4 EndY=3.9 EndZ=0
    g1: LineSegment StartX=5.4 StartY=3.9 StartZ=0 EndX=7 EndY=3.9 EndZ=0
    g2: LineSegment StartX=7 StartY=3.9 StartZ=0 EndX=7 EndY=5.1 EndZ=0
    g3: LineSegment StartX=7 StartY=5.1 StartZ=0 EndX=5.4 EndY=5.1 EndZ=0
  constraints (11):
    c: Coincident(g0,g1)
    c: Coincident(g1,g2)
    c: Coincident(g2,g3)
    c: Coincident(g3,g0)
    c: Vertical(g0)
    c: Vertical(g2)
    c: Horizontal(g1)
    c: Horizontal(g3)
    c: Distance(g0,g2) = 1.6
    c: Distance(g1,g3) = 1.2
    c: Coincident(g2,g-3)
FEATURE [Sketcher::SketchObject] Sketch064  label="rampini_per_serraggio_struttura"
  ArcFitTolerance = 1e-06
  AttachmentSupport = -> [XZ_Plane002]
  ExternalGeometry = -> [Sketch066,Sketch045]
  FullyConstrained = true
  MakeInternals = false
  MapMode = 5
  Placement = pos=(0,0,0) rot=(1,0,0;1.5708rad)
  sketch-geometry (7):
    g0: LineSegment StartX=7 StartY=5.1 StartZ=0 EndX=7 EndY=3.9 EndZ=0
    g1: LineSegment StartX=7 StartY=3.9 StartZ=0 EndX=9 EndY=3.9 EndZ=0
    g2: LineSegment StartX=7 StartY=5.1 StartZ=0 EndX=7 EndY=5.1 EndZ=0
    g3: LineSegment StartX=7 StartY=5.1 StartZ=0 EndX=7 EndY=7.5 EndZ=0
    g4: LineSegment StartX=9 StartY=5.1 StartZ=0 EndX=9 EndY=3.9 EndZ=0
    g5: LineSegment StartX=7 StartY=7.5 StartZ=0 EndX=9 EndY=7.5 EndZ=0
    g6: LineSegment StartX=9 StartY=7.5 StartZ=0 EndX=9 EndY=5.1 EndZ=0
  constraints (20):
    c: Vertical(g0)
    c: Coincident(g1,g0)
    c: Horizontal(g1)
    c: Coincident(g2,g0)
    c: Horizontal(g2)
    c: Coincident(g3,g2)
    c: Vertical(g3)
    c: Coincident(g5,g3)
    c: Coincident(g4,g6)
    c: Coincident(g4,g1)
    c: Vertical(g4)
    c: Coincident(g0,g-3)
    c: DistanceY(g-4,g3) = 2.4
    c: DistanceX(g1,g1) = 2
    c: DistanceY(g2,g6) = 0
    c: DistanceX(g2,g2) = 0
    c: DistanceY(g0,g0) = 1.2
    c: Coincident(g5,g6)
    c: Horizontal(g5)
    c: Vertical(g6)
FEATURE [Part::Extrusion] Extrude070  label="Extrude piano per rampino"
  Base = -> Sketch066
  Dir = (0,-1,2e-16)
  DirMode = 2
  FaceMakerClass = Part::FaceMakerBullseye
  FaceMakerMode = 3
  LengthFwd = 17
  LengthRev = 0
  Solid = true
  Symmetric = true
FEATURE [Part::Extrusion] Extrude071  label="Extrude rampini_per_serraggio_struttura"
  Base = -> Sketch064
  Dir = (0,-1,2e-16)
  DirMode = 2
  FaceMakerClass = Part::FaceMakerBullseye
  FaceMakerMode = 3
  LengthFwd = 5
  LengthRev = 0
  Solid = true
  Symmetric = true
FEATURE [Part::MultiFuse] Fusion003  label="Fusion supporto neopixel completo"
  Refine = true
  Shapes = -> [Fusion001,Extrude070,Extrude071]
FEATURE [Sketcher::SketchObject] Sketch067  label="perno per blocco switch"
  ArcFitTolerance = 1e-06
  AttachmentSupport = -> [XZ_Plane]
  ExternalGeometry = -> [Sketch,Sketch010]
  FullyConstrained = true
  MakeInternals = false
  MapMode = 5
  Placement = pos=(0,0,0) rot=(1,0,0;1.5708rad)
  sketch-geometry (14):
    g0: LineSegment StartX=-191.073 StartY=24.9429 StartZ=0 EndX=-185.81 EndY=23.0276 EndZ=0
    g1: LineSegment StartX=-183.76 StartY=23.9839 StartZ=0 EndX=-182.392 EndY=27.7427 EndZ=0
    g2: LineSegment StartX=-183.348 StartY=29.7934 StartZ=0 EndX=-188.61 EndY=31.7087 EndZ=0
    g3: LineSegment StartX=-188.61 StartY=31.7087 StartZ=0 EndX=-191.073 EndY=24.9429 EndZ=0
    g4: GeomPoint [constr] X=-186.459 Y=27.0946 Z=0
    g5: LineSegment StartX=-189.022 StartY=25.8992 StartZ=0 EndX=-185.263 EndY=24.5311 EndZ=0
    g6: LineSegment StartX=-185.263 StartY=24.5311 StartZ=0 EndX=-183.895 EndY=28.2899 EndZ=0
    g7: LineSegment StartX=-183.895 StartY=28.2899 StartZ=0 EndX=-187.654 EndY=29.658 EndZ=0
    g8: LineSegment StartX=-187.654 StartY=29.658 StartZ=0 EndX=-189.022 EndY=25.8992 EndZ=0
    g9: GeomPoint [constr] X=-186.459 Y=27.0946 Z=0
    g10: ArcOfCircle CenterX=-185.263 CenterY=24.5311 CenterZ=0 NormalX=0 NormalY=0 NormalZ=1 AngleXU=0 Radius=1.6 StartAngle=4.36332 EndAngle=5.93412
    g11: GeomPoint [constr] X=-184.307 Y=22.4804 Z=0
    g12: ArcOfCircle CenterX=-183.895 CenterY=28.2899 CenterZ=0 NormalX=0 NormalY=0 NormalZ=1 AngleXU=0 Radius=1.6 StartAngle=5.93412 EndAngle=7.50492
    g13: GeomPoint [constr] X=-181.844 Y=29.2462 Z=0
  constraints (30):
    c: Coincident(g2,g3)
    c: Coincident(g3,g0)
    c: Symmetric(g13,g0,g4)
    c: Distance(g11,g3) = 7.2
    c: Distance(g0,g2) = 7.2
    c: Parallel(g3,g1)
    c: Parallel(g2,g0)
    c: Perpendicular(g2,g3)
    c: Coincident(g5,g6)
    c: Coincident(g6,g7)
    c: Coincident(g7,g8)
    c: Coincident(g8,g5)
    c: Symmetric(g7,g5,g9)
    c: Distance(g6,g8) = 4
    c: Distance(g5,g7) = 4
    c: Coincident(g9,g4)
    c: Parallel(g8,g6)
    c: Parallel(g7,g5)
    c: Perpendicular(g7,g8)
    c: Tangent(g8,g-3)
    c: Tangent(g2,g-4)
    c: PointOnObject(g11,g1)
    c: PointOnObject(g11,g0)
    c: Tangent(g1,g10) = -1.5708
    c: Tangent(g0,g10) = -1.5708
    c: PointOnObject(g13,g1)
    c: Tangent(g1,g12) = -1.5708
    c: Tangent(g2,g12) = -1.5708
    c: Equal(g10,g12)
    c: Coincident(g10,g5)
FEATURE [Part::Extrusion] Extrude072  label="Extrude perno per blocco switch"
  Base = -> Sketch067
  Dir = (0,-1,2e-16)
  DirMode = 2
  FaceMakerClass = Part::FaceMakerBullseye
  FaceMakerMode = 3
  LengthFwd = 25.2
  LengthRev = 0
  Solid = true
  Symmetric = true
FEATURE [Part::MultiFuse] Fusion
  Refine = true
  Shapes = -> [Extrude,Sweep,Extrude007,Extrude011,Extrude005,Extrude012,Extrude013,Extrude016,Extrude031,Extrude039,Extrude045,Extrude072]
FEATURE [Part::Cut] Cut
  Base = -> Fusion
  Refine = true
  Tool = -> Extrude001
FEATURE [Part::Cut] Cut001
  Base = -> Cut
  Refine = true
  Tool = -> Extrude004
FEATURE [Part::Cut] Cut002
  Base = -> Cut001
  Refine = true
  Tool = -> Extrude006
FEATURE [Part::Cut] Cut003
  Base = -> Cut002
  Refine = true
  Tool = -> Extrude008
FEATURE [Part::Cut] Cut004
  Base = -> Cut003
  Refine = true
  Tool = -> Extrude009
FEATURE [Part::Cut] Cut005
  Base = -> Cut004
  Refine = true
  Tool = -> Extrude010
FEATURE [Part::Cut] Cut006
  Base = -> Cut005
  Refine = true
  Tool = -> Extrude014
FEATURE [Part::Cut] Cut007
  Base = -> Cut006
  Refine = true
  Tool = -> Extrude015
FEATURE [Part::Cut] Cut008
  Base = -> Cut007
  Refine = true
  Tool = -> Extrude018
FEATURE [Part::Cut] Cut009
  Base = -> Cut008
  Refine = true
  Tool = -> Extrude019
FEATURE [Part::Cut] Cut010
  Base = -> Cut009
  Refine = true
  Tool = -> Extrude020
FEATURE [Part::Cut] Cut011
  Base = -> Cut010
  Refine = true
  Tool = -> Extrude021
FEATURE [Part::Cut] Cut012
  Base = -> Cut011
  Refine = true
  Tool = -> Extrude022
FEATURE [Part::Cut] Cut013
  Base = -> Cut012
  Refine = true
  Tool = -> Extrude023
FEATURE [Part::Cut] Cut014
  Base = -> Cut013
  Refine = true
  Tool = -> Extrude032
FEATURE [Part::Cut] Cut015
  Base = -> Cut014
  Refine = true
  Tool = -> Extrude033
FEATURE [Part::Cut] Cut016
  Base = -> Cut015
  Refine = true
  Tool = -> Extrude034
FEATURE [Part::Cut] Cut017
  Base = -> Cut016
  Refine = true
  Tool = -> Extrude035
FEATURE [Part::Cut] Cut018
  Base = -> Cut017
  Refine = true
  Tool = -> Extrude036
FEATURE [Part::Cut] Cut019
  Base = -> Cut018
  Refine = true
  Tool = -> Extrude037
FEATURE [Part::Cut] Cut020
  Base = -> Cut019
  Refine = true
  Tool = -> Extrude030
FEATURE [Part::Cut] Cut022
  Base = -> Cut020
  Refine = true
  Tool = -> Extrude038
FEATURE [Part::Cut] Cut023
  Base = -> Cut022
  Refine = true
  Tool = -> Extrude041
FEATURE [Part::Cut] Cut024
  Base = -> Cut023
  Refine = true
  Tool = -> Extrude040
FEATURE [Part::Cut] Cut025
  Base = -> Cut024
  Refine = true
  Tool = -> Extrude042
FEATURE [Part::Cut] Cut026
  Base = -> Cut025
  Refine = true
  Tool = -> Extrude043
FEATURE [Part::Cut] Cut027
  Base = -> Cut026
  Refine = true
  Tool = -> Extrude044
FEATURE [Part::Cut] Cut028
  Base = -> Cut027
  Refine = true
  Tool = -> Extrude046
FEATURE [Part::Cut] Cut029
  Base = -> Cut028
  Refine = true
  Tool = -> Extrude047
FEATURE [Part::Cut] Cut033
  Base = -> Cut029
  Refine = true
  Tool = -> Extrude055
FEATURE [Part::Cut] Cut034
  Base = -> Cut033
  Refine = true
  Tool = -> Extrude056
FEATURE [Part::Cut] Cut035
  Base = -> Cut034
  Refine = true
  Tool = -> Extrude057
FEATURE [Part::Cut] Cut037
  Base = -> Cut035
  Refine = true
  Tool = -> Extrude060
FEATURE [Part::Cut] Cut038
  Base = -> Cut037
  Refine = true
  Tool = -> Extrude061
FEATURE [Part::Cut] Cut039
  Base = -> Cut038
  Refine = true
  Tool = -> Extrude063
FEATURE [Part::Cut] Cut040
  Base = -> Cut039
  Refine = true
  Tool = -> Extrude064
FEATURE [Part::Cut] Cut041
  Base = -> Cut040
  Refine = true
  Tool = -> Extrude062
FEATURE [Sketcher::SketchObject] Sketch068  label="base con smusso sopra neopixel"
  ArcFitTolerance = 1e-06
  AttachmentSupport = -> [YZ_Plane002]
  FullyConstrained = true
  MakeInternals = false
  MapMode = 5
  Placement = pos=(0,0,0) rot=(0.57735,0.57735,0.57735;2.0944rad)
  sketch-geometry (5):
    g0: LineSegment StartX=-9.5 StartY=-6.1 StartZ=0 EndX=9.5 EndY=-6.1 EndZ=0
    g1: LineSegment StartX=9.5 StartY=-6.1 StartZ=0 EndX=9.5 EndY=6.1 EndZ=0
    g2: LineSegment StartX=9.5 StartY=6.1 StartZ=0 EndX=-9.5 EndY=6.1 EndZ=0
    g3: LineSegment StartX=-9.5 StartY=6.1 StartZ=0 EndX=-9.5 EndY=-6.1 EndZ=0
    g4: GeomPoint [constr] X=0 Y=0 Z=0
  constraints (12):
    c: Coincident(g0,g1)
    c: Coincident(g1,g2)
    c: Coincident(g2,g3)
    c: Coincident(g3,g0)
    c: Horizontal(g0)
    c: Horizontal(g2)
    c: Vertical(g1)
    c: Vertical(g3)
    c: Symmetric(g2,g0,g4)
    c: Distance(g1,g3) = 19
    c: Distance(g0,g2) = 12.2
    c: Coincident(g4,g-1)
FEATURE [PartDesign::Body] Body002  label="supporto per neopixel"
  AllowCompound = false
  Group = -> [Sketch045,Sketch046,Sketch047,Sketch048,Sketch049,Sketch064,Sketch066,Sketch068]
  Origin = -> Origin002
FEATURE [Part::Extrusion] Extrude073  label="Extrude base con smusso sopra neopixel"
  Base = -> Sketch068
  Dir = (1,0,0)
  DirMode = 2
  FaceMakerClass = Part::FaceMakerBullseye
  FaceMakerMode = 3
  LengthFwd = -1
  LengthRev = 0
  Solid = true
  Symmetric = false
FEATURE [Part::Chamfer] Chamfer  label="Chamfer frontale supporto neopixel da fondere al supporto"
  Base = -> Extrude073
  EdgeLinks = -> Extrude073 [Edge4,Edge7,Edge10,Edge12]
  Edges = 4 edges r=0.5: [Edge4,Edge7,Edge10,Edge12]
FEATURE [Sketcher::SketchObject] Sketch069  label="cilindro minore"
  ArcFitTolerance = 1e-06
  AttachmentSupport = -> [XZ_Plane004]
  FullyConstrained = true
  MakeInternals = false
  MapMode = 5
  Placement = pos=(0,0,0) rot=(1,0,0;1.5708rad)
  sketch-geometry (1):
    g0: Circle CenterX=0 CenterY=0 CenterZ=0 NormalX=0 NormalY=0 NormalZ=1 AngleXU=0 Radius=5.8
  constraints (2):
    c: Diameter(g0) = 11.6
    c: Coincident(g0,g-1)
FEATURE [Sketcher::SketchObject] Sketch070  label="cilindro maggiore"
  ArcFitTolerance = 1e-06
  AttachmentSupport = -> [XZ_Plane004]
  ExternalGeometry = -> [Sketch069]
  FullyConstrained = true
  MakeInternals = false
  MapMode = 5
  Placement = pos=(0,0,0) rot=(1,0,0;1.5708rad)
  sketch-geometry (1):
    g0: Circle CenterX=0 CenterY=0 CenterZ=0 NormalX=0 NormalY=0 NormalZ=1 AngleXU=0 Radius=6.5
  constraints (2):
    c: Coincident(g0,g-1)
    c: Diameter(g0) = 13
FEATURE [Sketcher::SketchObject] Sketch071  label="buco interno"
  ArcFitTolerance = 1e-06
  AttachmentSupport = -> [XZ_Plane004]
  ExternalGeometry = -> [Sketch069]
  FullyConstrained = true
  MakeInternals = false
  MapMode = 5
  Placement = pos=(0,0,0) rot=(1,0,0;1.5708rad)
  sketch-geometry (1):
    g0: Circle CenterX=0 CenterY=0 CenterZ=0 NormalX=0 NormalY=0 NormalZ=1 AngleXU=0 Radius=5
  constraints (2):
    c: Coincident(g0,g-1)
    c: Diameter(g0) = 10
FEATURE [PartDesign::Pad] Pad
  Direction = (0,-1,2e-16)
  Length = 1.2
  Length2 = 10
  Placement = pos=(0,0,0) rot=(1,0,0;1.5708rad)
  Profile = -> Sketch070
  ReferenceAxis = -> Sketch070 [N_Axis]
  Refine = true
  Suppressed = false
  Type = 0
FEATURE [PartDesign::Pad] Pad001
  BaseFeature = -> Pad
  Direction = (0,-1,2e-16)
  Length = 5.6
  Length2 = 10
  Placement = pos=(0,0,0) rot=(1,0,0;1.5708rad)
  Profile = -> Sketch069
  ReferenceAxis = -> Sketch069 [N_Axis]
  Refine = true
  Suppressed = false
  Type = 0
FEATURE [PartDesign::Pocket] Pocket
  BaseFeature = -> Pad001
  Direction = (0,1,-2e-16)
  Length = 7
  Length2 = 5
  Midplane = true
  Placement = pos=(0,0,0) rot=(1,0,0;1.5708rad)
  Profile = -> Sketch071
  ReferenceAxis = -> Sketch071 [N_Axis]
  Refine = true
  Suppressed = false
  Type = 0
FEATURE [PartDesign::Fillet] Fillet
  Base = -> Pocket [Face7]
  BaseFeature = -> Pocket
  Placement = pos=(0,0,0) rot=(1,0,0;1.5708rad)
  Radius = 1
  Refine = true
  SupportTransform = false
  Suppressed = false
  UseAllEdges = false
FEATURE [PartDesign::Body] Body004  label="pulsanti lato sinistro"
  AllowCompound = false
  Group = -> [Sketch069,Sketch070,Sketch071,Pad,Pad001,Pocket,Fillet]
  Origin = -> Origin004
  Tip = -> Fillet
FEATURE [Sketcher::SketchObject] Sketch072  label="buco per saldature e diodo driver solenoide"
  ArcFitTolerance = 1e-06
  AttachmentSupport = -> [XZ_Plane]
  ExternalGeometry = -> [Sketch038]
  FullyConstrained = true
  MakeInternals = false
  MapMode = 5
  Placement = pos=(0,0,0) rot=(1,0,0;1.5708rad)
  sketch-geometry (4):
    g0: LineSegment StartX=-209.225 StartY=-40.6939 StartZ=0 EndX=-204.154 EndY=-29.8182 EndZ=0
    g1: LineSegment StartX=-204.154 StartY=-29.8182 StartZ=0 EndX=-206.51 EndY=-28.7194 EndZ=0
    g2: LineSegment StartX=-206.51 StartY=-28.7194 StartZ=0 EndX=-211.582 EndY=-39.5951 EndZ=0
    g3: LineSegment StartX=-211.582 StartY=-39.5951 StartZ=0 EndX=-209.225 EndY=-40.6939 EndZ=0
  constraints (11):
    c: Coincident(g1,g0)
    c: Coincident(g2,g1)
    c: Coincident(g3,g2)
    c: Coincident(g3,g0)
    c: Parallel(g-3,g0)
    c: Parallel(g0,g2)
    c: Perpendicular(g0,g3)
    c: Perpendicular(g1,g0)
    c: Distance(g3) = 2.6
    c: Distance(g2) = 12
    c: Coincident(g0,g-3)
FEATURE [Part::Extrusion] Extrude074  label="Extrude buco per saldature e diodo driver solenoide"
  Base = -> Sketch072
  Dir = (0,-1,2e-16)
  DirMode = 2
  FaceMakerClass = Part::FaceMakerBullseye
  FaceMakerMode = 3
  LengthFwd = 14.6
  LengthRev = 0
  Solid = true
  Symmetric = true
FEATURE [Part::Cut] Cut042
  Base = -> Cut041
  Refine = true
  Tool = -> Extrude074
FEATURE [Sketcher::SketchObject] Sketch073  label="fori slargati blocco solenoide"
  ArcFitTolerance = 1e-06
  AttachmentSupport = -> [XY_Plane]
  ExternalGeometry = -> [Sketch030]
  FullyConstrained = true
  MakeInternals = false
  MapMode = 5
  sketch-geometry (2):
    g0: Circle CenterX=-152.209 CenterY=6.95 CenterZ=0 NormalX=0 NormalY=0 NormalZ=1 AngleXU=0 Radius=3.7
    g1: Circle CenterX=-130.41 CenterY=-6.95 CenterZ=0 NormalX=0 NormalY=0 NormalZ=1 AngleXU=0 Radius=3.7
  constraints (4):
    c: Diameter(g0) = 7.4
    c: Coincident(g0,g-3)
    c: Diameter(g1) = 7.4
    c: Coincident(g1,g-4)
FEATURE [Part::Extrusion] Extrude075  label="Extrude fori slargati blocco solenoide"
  Base = -> Sketch073
  Dir = (0,0,1)
  DirMode = 2
  FaceMakerClass = Part::FaceMakerBullseye
  FaceMakerMode = 3
  LengthFwd = 1.5
  LengthRev = 0
  Placement = pos=(0,0,36.4) rot=(0,0,1;0rad)
  Solid = true
  Symmetric = false
FEATURE [Part::Cut] Cut043
  Base = -> Cut042
  Refine = true
  Tool = -> Extrude075
FEATURE [Sketcher::SketchObject] Sketch074  label="lato sx pistola"
  ArcFitTolerance = 1e-06
  AttachmentSupport = -> [XZ_Plane]
  ExternalGeometry = -> [Sketch016,Sketch,Sketch058]
  FullyConstrained = true
  MakeInternals = false
  MapMode = 5
  Placement = pos=(0,0,0) rot=(1,0,0;1.5708rad)
  sketch-geometry (37):
    g0: LineSegment StartX=-82.8 StartY=3.2 StartZ=0 EndX=0 EndY=3.2 EndZ=0
    g1: LineSegment StartX=-82.8 StartY=3.2 StartZ=0 EndX=-82.8 EndY=6.2 EndZ=0
    g2: LineSegment [constr] StartX=-107.6 StartY=18 StartZ=0 EndX=-107.6 EndY=20 EndZ=0
    g3: LineSegment [constr] StartX=-132.428 StartY=18 StartZ=0 EndX=-132.428 EndY=20 EndZ=0
    g4: LineSegment StartX=-132.428 StartY=20 StartZ=0 EndX=-107.6 EndY=20 EndZ=0
    g5: ArcOfCircle CenterX=-107.6 CenterY=4 CenterZ=0 NormalX=0 NormalY=0 NormalZ=1 AngleXU=0 Radius=16 StartAngle=0.137937 EndAngle=1.5708
    g6: LineSegment StartX=-82.8 StartY=6.2 StartZ=0 EndX=-91.752 EndY=6.2 EndZ=0
    g7: LineSegment [constr] StartX=-145.743 StartY=8.32624 StartZ=0 EndX=-147.645 EndY=8.94427 EndZ=0
    g8: ArcOfCircle CenterX=-132.428 CenterY=4 CenterZ=0 NormalX=0 NormalY=0 NormalZ=1 AngleXU=0 Radius=16 StartAngle=1.5708 EndAngle=2.82743
    g9: LineSegment StartX=-215.932 StartY=-80.4316 StartZ=0 EndX=-176.685 EndY=-80.4316 EndZ=0
    g10: LineSegment StartX=-147.645 StartY=8.94427 StartZ=0 EndX=-176.685 EndY=-80.4316 EndZ=0
    g11: LineSegment [constr] StartX=-193.988 StartY=-2.33927 StartZ=0 EndX=-192.176 EndY=-3.18451 EndZ=0
    g12: LineSegment [constr] StartX=-217.232 StartY=-52.1862 StartZ=0 EndX=-215.42 EndY=-53.0314 EndZ=0
    g13: LineSegment StartX=-192.176 StartY=-3.18451 StartZ=0 EndX=-215.42 EndY=-53.0314 EndZ=0
    g14: ArcOfCircle CenterX=-184.801 CenterY=-67.3089 CenterZ=0 NormalX=0 NormalY=0 NormalZ=1 AngleXU=0 Radius=33.7833 StartAngle=2.70526 EndAngle=3.54053
    g15: ArcOfCircle CenterX=-207.583 CenterY=4 CenterZ=0 NormalX=0 NormalY=0 NormalZ=1 AngleXU=0 Radius=17 StartAngle=5.84685 EndAngle=7.56663
    g16: LineSegment StartX=-202.765 StartY=20.303 StartZ=0 EndX=-195.887 EndY=39.2 EndZ=0
    g17: LineSegment [constr] StartX=-193.885 StartY=33.0037 StartZ=0 EndX=-197.644 EndY=34.3718 EndZ=0
    g18: LineSegment StartX=-195.887 StartY=39.2 StartZ=0 EndX=0 EndY=39.2 EndZ=0
    g19: LineSegment StartX=0 StartY=3.2 StartZ=0 EndX=0 EndY=39.2 EndZ=0
    g20: LineSegment StartX=-189.939 StartY=31.5672 StartZ=0 EndX=-192.333 EndY=24.9893 EndZ=0
    g21: LineSegment StartX=-196.467 StartY=26.4942 StartZ=0 EndX=-194.073 EndY=33.0721 EndZ=0
    g22: Circle CenterX=-213.443 CenterY=-76.8316 CenterZ=0 NormalX=0 NormalY=0 NormalZ=1 AngleXU=0 Radius=1.8
    g23: Circle CenterX=-179.305 CenterY=-76.8316 CenterZ=0 NormalX=0 NormalY=0 NormalZ=1 AngleXU=0 Radius=1.8
    g24: Circle CenterX=-184.08 CenterY=34.8 CenterZ=0 NormalX=0 NormalY=0 NormalZ=1 AngleXU=0 Radius=1.8
    g25: Circle CenterX=-78.51 CenterY=34.8 CenterZ=0 NormalX=0 NormalY=0 NormalZ=1 AngleXU=0 Radius=1.8
    g26: Circle CenterX=-78.51 CenterY=7.6 CenterZ=0 NormalX=0 NormalY=0 NormalZ=1 AngleXU=0 Radius=1.8
    g27: Circle CenterX=-5.6 CenterY=34.8 CenterZ=0 NormalX=0 NormalY=0 NormalZ=1 AngleXU=0 Radius=1.8
    g28: Circle CenterX=-5.6 CenterY=7.6 CenterZ=0 NormalX=0 NormalY=0 NormalZ=1 AngleXU=0 Radius=1.8
    g29: LineSegment StartX=-190.127 StartY=31.6356 StartZ=0 EndX=-189.939 EndY=31.5672 EndZ=0
    g30: LineSegment StartX=-194.073 StartY=33.0721 StartZ=0 EndX=-193.885 EndY=33.0037 EndZ=0
    g31: LineSegment StartX=-193.885 StartY=33.0037 StartZ=0 EndX=-190.127 EndY=31.6356 EndZ=0
    g32: LineSegment StartX=-196.467 StartY=26.4942 StartZ=0 EndX=-192.333 EndY=24.9893 EndZ=0
    g33: Circle CenterX=-19 CenterY=21.2 CenterZ=0 NormalX=0 NormalY=0 NormalZ=1 AngleXU=0 Radius=6.3
    g34: Circle CenterX=-42 CenterY=21.2 CenterZ=0 NormalX=0 NormalY=0 NormalZ=1 AngleXU=0 Radius=6.3
    g35: Circle CenterX=-65 CenterY=21.2 CenterZ=0 NormalX=0 NormalY=0 NormalZ=1 AngleXU=0 Radius=6.3
    g36: LineSegment [constr] StartX=-4 StartY=21.2 StartZ=0 EndX=-65 EndY=21.2 EndZ=0
  constraints (96):
    c: Coincident(g0,g-41)
    c: Horizontal(g0)
    c: PointOnObject(g0,g-39)
    c: Coincident(g1,g0)
    c: Vertical(g1)
    c: DistanceY(g1,g1) = 3
    c: Coincident(g2,g-17)
    c: Vertical(g2)
    c: Coincident(g3,g-16)
    c: Vertical(g3)
    c: DistanceY(g2,g2) = 2
    c: DistanceY(g3,g3) = 2
    c: Coincident(g4,g3)
    c: Coincident(g4,g2)
    c: Coincident(g5,g-17)
    c: Coincident(g5,g2)
    c: Coincident(g6,g1)
    c: Horizontal(g6)
    c: Coincident(g6,g5)
    c: Coincident(g7,g-15)
    c: Coincident(g8,g7)
    c: Coincident(g8,g3)
    c: Coincident(g8,g-15)
    c: Horizontal(g9)
    c: DistanceY(g-13,g9) = 2
    c: Coincident(g10,g7)
    c: Parallel(g10,g-14)
    c: Coincident(g9,g10)
    c: Distance(g11) = 2
    c: Coincident(g11,g-11)
    c: Perpendicular(g-11,g11)
    c: Distance(g12) = 2
    c: Coincident(g12,g-12)
    c: Perpendicular(g-11,g12)
    c: Coincident(g13,g11)
    c: Coincident(g13,g12)
    c: Coincident(g14,g-32)
    c: Coincident(g14,g12)
    c: Coincident(g14,g9)
    c: Coincident(g15,g-10)
    c: Coincident(g15,g11)
    c: Parallel(g16,g-22)
    c: Distance(g17) = 4
    c: PointOnObject(g17,g16)
    c: Coincident(g15,g16)
    c: Horizontal(g18)
    c: Coincident(g18,g16)
    c: Coincident(g19,g0)
    c: PointOnObject(g19,g-39)
    c: DistanceY(g19,g-36) = 2
    c: Coincident(g18,g19)
    c: Diameter(g22) = 3.6
    c: Coincident(g22,g-9)
    c: Diameter(g23) = 3.6
    c: Coincident(g23,g-8)
    c: Diameter(g24) = 3.6
    c: Diameter(g25) = 3.6
    c: Diameter(g26) = 3.6
    c: Diameter(g27) = 3.6
    c: Diameter(g28) = 3.6
    c: Coincident(g27,g-4)
    c: Coincident(g28,g-3)
    c: Coincident(g25,g-6)
    c: Coincident(g26,g-5)
    c: Coincident(g24,g-7)
    c: Parallel(g20,g-21)
    c: Equal(g20,g-21)
    c: Parallel(g21,g-19)
    c: Equal(g21,g-19)
    c: Distance(g29) = 0.2
    c: Distance(g30) = 0.2
    c: Parallel(g29,g-20)
    c: Parallel(g31,g-20)
    c: Equal(g31,g-20)
    c: Coincident(g30,g31)
    c: Coincident(g31,g29)
    c: Coincident(g29,g-21)
    c: Parallel(g30,g31)
    c: Coincident(g17,g30)
    c: Coincident(g20,g29)
    c: Coincident(g21,g30)
    c: Perpendicular(g16,g17)
    c: Coincident(g32,g21)
    c: Coincident(g32,g20)
    c: Perpendicular(g10,g7)
    c: Diameter(g33) = 12.6
    c: Diameter(g34) = 12.6
    c: Diameter(g35) = 12.6
    c: Horizontal(g36)
    c: PointOnObject(g33,g36)
    c: PointOnObject(g34,g36)
    c: DistanceX(g34,g33) = 23
    c: DistanceX(g35,g34) = 23
    c: DistanceX(g33,g36) = 15
    c: Symmetric(g-24,g-24,g36)
    c: Coincident(g36,g35)
FEATURE [Part::Extrusion] Extrude076  label="Extrude lato sx pistola"
  Base = -> Sketch074
  Dir = (0,-1,2e-16)
  DirMode = 2
  FaceMakerClass = Part::FaceMakerBullseye
  FaceMakerMode = 3
  LengthFwd = -2
  LengthRev = 0
  Solid = true
  Symmetric = false
FEATURE [Sketcher::SketchObject] Sketch075  label="lato dx pistola"
  ArcFitTolerance = 1e-06
  AttachmentSupport = -> [XZ_Plane]
  ExternalGeometry = -> [Sketch016,Sketch,Sketch058,Sketch074]
  FullyConstrained = true
  MakeInternals = false
  MapMode = 5
  Placement = pos=(0,0,0) rot=(1,0,0;1.5708rad)
  sketch-geometry (61):
    g0: LineSegment StartX=-82.8 StartY=3.2 StartZ=0 EndX=0 EndY=3.2 EndZ=0
    g1: LineSegment StartX=-82.8 StartY=3.2 StartZ=0 EndX=-82.8 EndY=6.2 EndZ=0
    g2: LineSegment [constr] StartX=-107.6 StartY=18 StartZ=0 EndX=-107.6 EndY=20 EndZ=0
    g3: LineSegment [constr] StartX=-132.428 StartY=18 StartZ=0 EndX=-132.428 EndY=20 EndZ=0
    g4: LineSegment StartX=-132.428 StartY=20 StartZ=0 EndX=-107.6 EndY=20 EndZ=0
    g5: ArcOfCircle CenterX=-107.6 CenterY=4 CenterZ=0 NormalX=0 NormalY=0 NormalZ=1 AngleXU=0 Radius=16 StartAngle=0.137937 EndAngle=1.5708
    g6: LineSegment StartX=-82.8 StartY=6.2 StartZ=0 EndX=-91.752 EndY=6.2 EndZ=0
    g7: LineSegment [constr] StartX=-145.743 StartY=8.32624 StartZ=0 EndX=-147.645 EndY=8.94427 EndZ=0
    g8: ArcOfCircle CenterX=-132.428 CenterY=4 CenterZ=0 NormalX=0 NormalY=0 NormalZ=1 AngleXU=0 Radius=16 StartAngle=1.5708 EndAngle=2.82743
    g9: LineSegment StartX=-215.932 StartY=-80.4316 StartZ=0 EndX=-176.685 EndY=-80.4316 EndZ=0
    g10: LineSegment StartX=-147.645 StartY=8.94427 StartZ=0 EndX=-176.685 EndY=-80.4316 EndZ=0
    g11: LineSegment [constr] StartX=-193.988 StartY=-2.33927 StartZ=0 EndX=-192.176 EndY=-3.18451 EndZ=0
    g12: LineSegment [constr] StartX=-217.232 StartY=-52.1862 StartZ=0 EndX=-215.42 EndY=-53.0314 EndZ=0
    g13: LineSegment StartX=-192.176 StartY=-3.18451 StartZ=0 EndX=-215.42 EndY=-53.0314 EndZ=0
    g14: ArcOfCircle CenterX=-184.801 CenterY=-67.3089 CenterZ=0 NormalX=0 NormalY=0 NormalZ=1 AngleXU=0 Radius=33.7833 StartAngle=2.70526 EndAngle=3.54053
    g15: ArcOfCircle CenterX=-207.583 CenterY=4 CenterZ=0 NormalX=0 NormalY=0 NormalZ=1 AngleXU=0 Radius=17 StartAngle=5.84685 EndAngle=7.56663
    g16: LineSegment StartX=-202.765 StartY=20.303 StartZ=0 EndX=-195.887 EndY=39.2 EndZ=0
    g17: LineSegment [constr] StartX=-193.885 StartY=33.0037 StartZ=0 EndX=-197.644 EndY=34.3718 EndZ=0
    g18: LineSegment StartX=-195.887 StartY=39.2 StartZ=0 EndX=0 EndY=39.2 EndZ=0
    g19: LineSegment StartX=0 StartY=3.2 StartZ=0 EndX=0 EndY=39.2 EndZ=0
    g20: LineSegment StartX=-189.939 StartY=31.5672 StartZ=0 EndX=-192.333 EndY=24.9893 EndZ=0
    g21: LineSegment StartX=-196.467 StartY=26.4942 StartZ=0 EndX=-194.073 EndY=33.0721 EndZ=0
    g22: Circle CenterX=-213.443 CenterY=-76.8316 CenterZ=0 NormalX=0 NormalY=0 NormalZ=1 AngleXU=0 Radius=1.8
    g23: Circle CenterX=-179.305 CenterY=-76.8316 CenterZ=0 NormalX=0 NormalY=0 NormalZ=1 AngleXU=0 Radius=1.8
    g24: Circle CenterX=-184.08 CenterY=34.8 CenterZ=0 NormalX=0 NormalY=0 NormalZ=1 AngleXU=0 Radius=1.8
    g25: Circle CenterX=-78.51 CenterY=34.8 CenterZ=0 NormalX=0 NormalY=0 NormalZ=1 AngleXU=0 Radius=1.8
    g26: Circle CenterX=-78.51 CenterY=7.6 CenterZ=0 NormalX=0 NormalY=0 NormalZ=1 AngleXU=0 Radius=1.8
    g27: Circle CenterX=-5.6 CenterY=34.8 CenterZ=0 NormalX=0 NormalY=0 NormalZ=1 AngleXU=0 Radius=1.8
    g28: Circle CenterX=-5.6 CenterY=7.6 CenterZ=0 NormalX=0 NormalY=0 NormalZ=1 AngleXU=0 Radius=1.8
    g29: LineSegment StartX=-190.127 StartY=31.6356 StartZ=0 EndX=-189.939 EndY=31.5672 EndZ=0
    g30: LineSegment StartX=-194.073 StartY=33.0721 StartZ=0 EndX=-193.885 EndY=33.0037 EndZ=0
    g31: LineSegment StartX=-193.885 StartY=33.0037 StartZ=0 EndX=-190.127 EndY=31.6356 EndZ=0
    g32: LineSegment StartX=-196.467 StartY=26.4942 StartZ=0 EndX=-192.333 EndY=24.9893 EndZ=0
    g33: LineSegment [constr] StartX=-4 StartY=21.2 StartZ=0 EndX=-87.91 EndY=21.2 EndZ=0
    g34: GeomPoint [constr] X=-4 Y=21.2 Z=0
    g35: LineSegment [constr] StartX=-15.2 StartY=33.7 StartZ=0 EndX=-15.2 EndY=8.7 EndZ=0
    g36: LineSegment [constr] StartX=-15.2 StartY=33.7 StartZ=0 EndX=-56.2 EndY=33.7 EndZ=0
    g37: LineSegment [constr] StartX=-15.2 StartY=8.7 StartZ=0 EndX=-56.2 EndY=8.7 EndZ=0
    g38: LineSegment [constr] StartX=-56.2 StartY=33.7 StartZ=0 EndX=-56.2 EndY=8.7 EndZ=0
    g39: Circle CenterX=-18.6 CenterY=30.3 CenterZ=0 NormalX=0 NormalY=0 NormalZ=1 AngleXU=0 Radius=3.4
    g40: Circle CenterX=-18.6 CenterY=12.1 CenterZ=0 NormalX=0 NormalY=0 NormalZ=1 AngleXU=0 Radius=3.4
    g41: Circle CenterX=-43.2 CenterY=30.3 CenterZ=0 NormalX=0 NormalY=0 NormalZ=1 AngleXU=0 Radius=3.4
    g42: Circle CenterX=-43.2 CenterY=12.1 CenterZ=0 NormalX=0 NormalY=0 NormalZ=1 AngleXU=0 Radius=3.4
    g43: LineSegment [constr] StartX=-4 StartY=21.2 StartZ=0 EndX=-15.2 EndY=21.2 EndZ=0
    g44: LineSegment [constr] StartX=-15.2 StartY=21.2 StartZ=0 EndX=-36.2 EndY=21.2 EndZ=0
    g45: LineSegment [constr] StartX=-41.5 StartY=16.2 StartZ=0 EndX=-30.9 EndY=16.2 EndZ=0
    g46: LineSegment [constr] StartX=-30.9 StartY=16.2 StartZ=0 EndX=-30.9 EndY=26.2 EndZ=0
    g47: LineSegment [constr] StartX=-30.9 StartY=26.2 StartZ=0 EndX=-41.5 EndY=26.2 EndZ=0
    g48: LineSegment [constr] StartX=-41.5 StartY=26.2 StartZ=0 EndX=-41.5 EndY=16.2 EndZ=0
    g49: GeomPoint [constr] X=-36.2 Y=21.2 Z=0
    g50: Circle CenterX=-36.2 CenterY=21.2 CenterZ=0 NormalX=0 NormalY=0 NormalZ=1 AngleXU=0 Radius=2.8
    g51: LineSegment [constr] StartX=-24.2 StartY=26.7 StartZ=0 EndX=-24.2 EndY=15.7 EndZ=0
    g52: Circle CenterX=-24.2 CenterY=26.7 CenterZ=0 NormalX=0 NormalY=0 NormalZ=1 AngleXU=0 Radius=3
    g53: Circle CenterX=-24.2 CenterY=15.7 CenterZ=0 NormalX=0 NormalY=0 NormalZ=1 AngleXU=0 Radius=3
    g54: GeomPoint X=-18.6 Y=30.3 Z=0
    g55: GeomPoint X=-18.6 Y=12.1 Z=0
    g56: GeomPoint X=-43.2 Y=12.1 Z=0
    g57: GeomPoint X=-43.2 Y=30.3 Z=0
    g58: Circle CenterX=-65 CenterY=21.2 CenterZ=0 NormalX=0 NormalY=0 NormalZ=1 AngleXU=0 Radius=1.5
    g59: Circle CenterX=-42 CenterY=21.2 CenterZ=0 NormalX=0 NormalY=0 NormalZ=1 AngleXU=0 Radius=1.5
    g60: Circle CenterX=-19 CenterY=21.2 CenterZ=0 NormalX=0 NormalY=0 NormalZ=1 AngleXU=0 Radius=1.5
  constraints (149):
    c: Coincident(g0,g-41)
    c: Horizontal(g0)
    c: PointOnObject(g0,g-39)
    c: Coincident(g1,g0)
    c: Vertical(g1)
    c: DistanceY(g1,g1) = 3
    c: Coincident(g2,g-17)
    c: Vertical(g2)
    c: Coincident(g3,g-16)
    c: Vertical(g3)
    c: DistanceY(g2,g2) = 2
    c: DistanceY(g3,g3) = 2
    c: Coincident(g4,g3)
    c: Coincident(g4,g2)
    c: Coincident(g5,g-17)
    c: Coincident(g5,g2)
    c: Coincident(g6,g1)
    c: Horizontal(g6)
    c: Coincident(g6,g5)
    c: Coincident(g7,g-15)
    c: Coincident(g8,g7)
    c: Coincident(g8,g3)
    c: Coincident(g8,g-15)
    c: Horizontal(g9)
    c: DistanceY(g-13,g9) = 2
    c: Coincident(g10,g7)
    c: Parallel(g10,g-14)
    c: Coincident(g9,g10)
    c: Distance(g11) = 2
    c: Coincident(g11,g-11)
    c: Perpendicular(g-11,g11)
    c: Distance(g12) = 2
    c: Coincident(g12,g-12)
    c: Perpendicular(g-11,g12)
    c: Coincident(g13,g11)
    c: Coincident(g13,g12)
    c: Coincident(g14,g-32)
    c: Coincident(g14,g12)
    c: Coincident(g14,g9)
    c: Coincident(g15,g-10)
    c: Coincident(g15,g11)
    c: Parallel(g16,g-22)
    c: Distance(g17) = 4
    c: PointOnObject(g17,g16)
    c: Coincident(g15,g16)
    c: Horizontal(g18)
    c: Coincident(g18,g16)
    c: Coincident(g19,g0)
    c: PointOnObject(g19,g-39)
    c: DistanceY(g19,g-36) = 2
    c: Coincident(g18,g19)
    c: Diameter(g22) = 3.6
    c: Coincident(g22,g-9)
    c: Diameter(g23) = 3.6
    c: Coincident(g23,g-8)
    c: Diameter(g24) = 3.6
    c: Diameter(g25) = 3.6
    c: Diameter(g26) = 3.6
    c: Diameter(g27) = 3.6
    c: Diameter(g28) = 3.6
    c: Coincident(g27,g-4)
    c: Coincident(g28,g-3)
    c: Coincident(g25,g-6)
    c: Coincident(g26,g-5)
    c: Coincident(g24,g-7)
    c: Parallel(g20,g-21)
    c: Equal(g20,g-21)
    c: Parallel(g21,g-19)
    c: Equal(g21,g-19)
    c: Distance(g29) = 0.2
    c: Distance(g30) = 0.2
    c: Parallel(g29,g-20)
    c: Parallel(g31,g-20)
    c: Equal(g31,g-20)
    c: Coincident(g30,g31)
    c: Coincident(g31,g29)
    c: Coincident(g29,g-21)
    c: Parallel(g30,g31)
    c: Coincident(g17,g30)
    c: Coincident(g20,g29)
    c: Coincident(g21,g30)
    c: Perpendicular(g16,g17)
    c: Coincident(g32,g21)
    c: Coincident(g32,g20)
    c: Perpendicular(g10,g7)
    c: Horizontal(g33)
    c: Symmetric(g-24,g-24,g33)
    c: PointOnObject(g33,g-28)
    c: Symmetric(g-24,g-24,g34)
    c: DistanceY(g35,g35) = 25
    c: Symmetric(g35,g35,g33)
    c: Distance(g36) = 41
    c: Coincident(g36,g35)
    c: Horizontal(g36)
    c: Coincident(g37,g35)
    c: Horizontal(g37)
    c: Coincident(g38,g36)
    c: Vertical(g38)
    c: Coincident(g37,g38)
    c: Diameter(g39) = 6.8
    c: Diameter(g40) = 6.8
    c: Tangent(g39,g36)
    c: Tangent(g40,g37)
    c: Tangent(g39,g35)
    c: Tangent(g40,g35)
    c: Diameter(g41) = 6.8
    c: Diameter(g42) = 6.8
    c: Tangent(g41,g36)
    c: Tangent(g42,g37)
    c: DistanceX(g41,g39) = 24.6
    c: DistanceX(g42,g40) = 24.6
    c: Distance(g43) = 11.2
    c: Coincident(g43,g33)
    c: PointOnObject(g43,g33)
    c: PointOnObject(g43,g35)
    c: Distance(g44) = 21
    c: Coincident(g44,g43)
    c: PointOnObject(g44,g33)
    c: Coincident(g45,g46)
    c: Coincident(g46,g47)
    c: Coincident(g47,g48)
    c: Coincident(g48,g45)
    c: Horizontal(g45)
    c: Horizontal(g47)
    c: Vertical(g46)
    c: Vertical(g48)
    c: Symmetric(g47,g45,g49)
    c: Distance(g46,g48) = 10.6
    c: Distance(g45,g47) = 10
    c: Coincident(g49,g44)
    c: Diameter(g50) = 5.6
    c: Coincident(g50,g44)
    c: Distance(g51) = 11
    c: Symmetric(g51,g51,g33)
    c: DistanceX(g51,g43) = 9
    c: Diameter(g52) = 6
    c: Coincident(g52,g51)
    c: Diameter(g53) = 6
    c: Coincident(g53,g51)
    c: Coincident(g40,g55)
    c: Coincident(g39,g54)
    c: Coincident(g41,g57)
    c: Coincident(g42,g56)
    c: Diameter(g58) = 3
    c: Diameter(g59) = 3
    c: Diameter(g60) = 3
    c: Coincident(g58,g-44)
    c: Coincident(g59,g-46)
    c: Coincident(g60,g-45)
FEATURE [Sketcher::SketchObject] Sketch076  label="lato sx pistola - scavi pulsanti"
  ArcFitTolerance = 1e-06
  AttachmentSupport = -> [XZ_Plane]
  ExternalGeometry = -> [Sketch074]
  FullyConstrained = true
  MakeInternals = false
  MapMode = 5
  Placement = pos=(0,0,0) rot=(1,0,0;1.5708rad)
  sketch-geometry (3):
    g0: Circle CenterX=-65 CenterY=21.2 CenterZ=0 NormalX=0 NormalY=0 NormalZ=1 AngleXU=0 Radius=7.3
    g1: Circle CenterX=-42 CenterY=21.2 CenterZ=0 NormalX=0 NormalY=0 NormalZ=1 AngleXU=0 Radius=7.3
    g2: Circle CenterX=-19 CenterY=21.2 CenterZ=0 NormalX=0 NormalY=0 NormalZ=1 AngleXU=0 Radius=7.3
  constraints (6):
    c: Diameter(g0) = 14.6
    c: Diameter(g1) = 14.6
    c: Diameter(g2) = 14.6
    c: Coincident(g0,g-3)
    c: Coincident(g1,g-4)
    c: Coincident(g2,g-5)
FEATURE [Part::Extrusion] Extrude077  label="Extrude lato sx pistola - scavi pulsanti"
  Base = -> Sketch076
  Dir = (0,-1,2e-16)
  DirMode = 2
  FaceMakerClass = Part::FaceMakerBullseye
  FaceMakerMode = 3
  LengthFwd = -1.2
  LengthRev = 0
  Solid = true
  Symmetric = false
FEATURE [Part::Cut] Cut044
  Base = -> Extrude076
  Refine = true
  Tool = -> Extrude077
FEATURE [Part::Extrusion] Extrude078  label="Extrude lato dx pistola"
  Base = -> Sketch075
  Dir = (0,-1,2e-16)
  DirMode = 2
  FaceMakerClass = Part::FaceMakerBullseye
  FaceMakerMode = 3
  LengthFwd = 2
  LengthRev = 0
  Solid = true
  Symmetric = false
FEATURE [Sketcher::SketchObject] Sketch077  label="lato dx pistola - scavi pulsanti"
  ArcFitTolerance = 1e-06
  AttachmentSupport = -> [XZ_Plane]
  ExternalGeometry = -> [Sketch075]
  FullyConstrained = true
  MakeInternals = false
  MapMode = 5
  Placement = pos=(0,0,0) rot=(1,0,0;1.5708rad)
  sketch-geometry (4):
    g0: LineSegment StartX=-27.2 StartY=26.7 StartZ=0 EndX=-27.2 EndY=15.7 EndZ=0
    g1: LineSegment StartX=-21.2 StartY=26.7 StartZ=0 EndX=-21.2 EndY=15.7 EndZ=0
    g2: ArcOfCircle CenterX=-24.2 CenterY=26.7 CenterZ=0 NormalX=0 NormalY=0 NormalZ=1 AngleXU=0 Radius=3 StartAngle=5.96642e-06 EndAngle=3.14159
    g3: ArcOfCircle CenterX=-24.2 CenterY=15.7 CenterZ=0 NormalX=0 NormalY=0 NormalZ=1 AngleXU=0 Radius=3 StartAngle=3.14159 EndAngle=6.28319
  constraints (10):
    c: Vertical(g0)
    c: Coincident(g2,g-3)
    c: Vertical(g1)
    c: Coincident(g3,g-4)
    c: Tangent(g1,g-3)
    c: Tangent(g0,g-3)
    c: Tangent(g3,g0) = -1.5708
    c: Coincident(g3,g1)
    c: Tangent(g0,g2) = -1.5708
    c: Coincident(g1,g2)
FEATURE [Part::Extrusion] Extrude079  label="Extrude lato dx pistola - scavi pulsanti"
  Base = -> Sketch077
  Dir = (0,-1,2e-16)
  DirMode = 2
  FaceMakerClass = Part::FaceMakerBullseye
  FaceMakerMode = 3
  LengthFwd = 1.2
  LengthRev = 0
  Solid = true
  Symmetric = false
FEATURE [Part::Cut] Cut045
  Base = -> Extrude078
  Refine = true
  Tool = -> Extrude079
FEATURE [Sketcher::SketchObject] Sketch078
  ArcFitTolerance = 1e-06
  AttachmentSupport = -> [XZ_Plane005]
  FullyConstrained = true
  MakeInternals = false
  MapMode = 5
  Placement = pos=(0,0,0) rot=(1,0,0;1.5708rad)
  sketch-geometry (5):
    g0: LineSegment [constr] StartX=0 StartY=5.5 StartZ=0 EndX=0 EndY=-5.5 EndZ=0
    g1: ArcOfCircle CenterX=0 CenterY=5.5 CenterZ=0 NormalX=0 NormalY=0 NormalZ=1 AngleXU=0 Radius=2.7 StartAngle=0 EndAngle=3.14159
    g2: ArcOfCircle CenterX=0 CenterY=-5.5 CenterZ=0 NormalX=0 NormalY=0 NormalZ=1 AngleXU=0 Radius=2.7 StartAngle=3.1416 EndAngle=6.28318
    g3: LineSegment StartX=-2.7 StartY=5.5 StartZ=0 EndX=-2.7 EndY=-5.50001 EndZ=0
    g4: LineSegment StartX=2.7 StartY=5.5 StartZ=0 EndX=2.7 EndY=-5.50001 EndZ=0
  constraints (13):
    c: Distance(g0) = 11
    c: Vertical(g0)
    c: Symmetric(g0,g0,g-1)
    c: Radius(g1) = 2.7
    c: Coincident(g1,g0)
    c: Radius(g2) = 2.7
    c: Coincident(g2,g0)
    c: Vertical(g3)
    c: Vertical(g4)
    c: Coincident(g2,g4)
    c: Coincident(g2,g3)
    c: Tangent(g3,g1) = -1.5708
    c: Tangent(g4,g1) = 1.5708
FEATURE [PartDesign::Pad] Pad002
  Direction = (0,-1,2e-16)
  Length = 0.8
  Length2 = 10
  Placement = pos=(0,0,0) rot=(1,0,0;1.5708rad)
  Profile = -> Sketch078
  ReferenceAxis = -> Sketch078 [N_Axis]
  Refine = true
  Suppressed = false
  Type = 0
FEATURE [Sketcher::SketchObject] Sketch079
  ArcFitTolerance = 1e-06
  AttachmentSupport = -> [XZ_Plane005]
  ExternalGeometry = -> [Sketch078]
  FullyConstrained = true
  MakeInternals = false
  MapMode = 5
  Placement = pos=(0,0,0) rot=(1,0,0;1.5708rad)
  sketch-geometry (2):
    g0: Circle CenterX=-1e-16 CenterY=5.5 CenterZ=0 NormalX=0 NormalY=0 NormalZ=1 AngleXU=0 Radius=2.7
    g1: Circle CenterX=0 CenterY=-5.5 CenterZ=0 NormalX=0 NormalY=0 NormalZ=1 AngleXU=0 Radius=2.7
  constraints (4):
    c: Coincident(g0,g-3)
    c: PointOnObject(g-3,g0)
    c: Coincident(g1,g-4)
    c: Equal(g1,g-4)
FEATURE [PartDesign::Pad] Pad003
  BaseFeature = -> Pad002
  Direction = (0,-1,2e-16)
  Length = 5
  Length2 = 10
  Placement = pos=(0,0,0) rot=(1,0,0;1.5708rad)
  Profile = -> Sketch079
  ReferenceAxis = -> Sketch079 [N_Axis]
  Refine = true
  Suppressed = false
  Type = 0
FEATURE [PartDesign::Fillet] Fillet001
  Base = -> Pad003 [Edge16,Edge14]
  BaseFeature = -> Pad003
  Placement = pos=(0,0,0) rot=(1,0,0;1.5708rad)
  Radius = 0.4
  Refine = true
  SupportTransform = false
  Suppressed = false
  UseAllEdges = false
FEATURE [PartDesign::Body] Body005  label="pulsanti lato destro"
  AllowCompound = false
  Group = -> [Sketch078,Pad002,Sketch079,Pad003,Fillet001]
  Origin = -> Origin005
  Tip = -> Fillet001
FEATURE [Sketcher::SketchObject] Sketch080  label="lato dx pistola - fori per inserto M3 x 3 x 4.5"
  ArcFitTolerance = 1e-06
  AttachmentSupport = -> [XZ_Plane]
  ExternalGeometry = -> [Sketch075]
  FullyConstrained = true
  MakeInternals = false
  MapMode = 5
  Placement = pos=(0,0,0) rot=(1,0,0;1.5708rad)
  sketch-geometry (4):
    g0: Circle CenterX=-18.6 CenterY=12.1 CenterZ=0 NormalX=0 NormalY=0 NormalZ=1 AngleXU=0 Radius=2.25
    g1: Circle CenterX=-18.6 CenterY=30.3 CenterZ=0 NormalX=0 NormalY=0 NormalZ=1 AngleXU=0 Radius=2.25
    g2: Circle CenterX=-43.2 CenterY=30.3 CenterZ=0 NormalX=0 NormalY=0 NormalZ=1 AngleXU=0 Radius=2.25
    g3: Circle CenterX=-43.2 CenterY=12.1 CenterZ=0 NormalX=0 NormalY=0 NormalZ=1 AngleXU=0 Radius=2.25
  constraints (8):
    c: Diameter(g0) = 4.5
    c: Coincident(g0,g-5)
    c: Diameter(g1) = 4.5
    c: Coincident(g1,g-4)
    c: Diameter(g2) = 4.5
    c: Coincident(g2,g-3)
    c: Diameter(g3) = 4.5
    c: Coincident(g3,g-6)
FEATURE [Sketcher::SketchObject] Sketch081  label="lato dx pistola - pieno per inserto M3 x 3 x 4,5"
  ArcFitTolerance = 1e-06
  AttachmentSupport = -> [XZ_Plane]
  ExternalGeometry = -> [Sketch075]
  FullyConstrained = true
  MakeInternals = false
  MapMode = 5
  Placement = pos=(0,0,0) rot=(1,0,0;1.5708rad)
  sketch-geometry (4):
    g0: Circle CenterX=-43.2 CenterY=30.3 CenterZ=0 NormalX=0 NormalY=0 NormalZ=1 AngleXU=0 Radius=3.4
    g1: Circle CenterX=-18.6 CenterY=30.3 CenterZ=0 NormalX=0 NormalY=0 NormalZ=1 AngleXU=0 Radius=3.4
    g2: Circle CenterX=-43.2 CenterY=12.1 CenterZ=0 NormalX=0 NormalY=0 NormalZ=1 AngleXU=0 Radius=3.4
    g3: Circle CenterX=-18.6 CenterY=12.1 CenterZ=0 NormalX=0 NormalY=0 NormalZ=1 AngleXU=0 Radius=3.4
  constraints (8):
    c: Diameter(g0) = 6.8
    c: Coincident(g0,g-6)
    c: Diameter(g1) = 6.8
    c: Coincident(g1,g-3)
    c: Diameter(g2) = 6.8
    c: Coincident(g2,g-5)
    c: Diameter(g3) = 6.8
    c: Coincident(g3,g-4)
FEATURE [Part::Extrusion] Extrude080  label="Extrude lato dx pistola - pieno per inserto M3 x 3 x 4,5"
  Base = -> Sketch081
  Dir = (0,-1,2e-16)
  DirMode = 2
  FaceMakerClass = Part::FaceMakerBullseye
  FaceMakerMode = 3
  LengthFwd = -2.4
  LengthRev = 0
  Solid = true
  Symmetric = false
FEATURE [Part::MultiFuse] Fusion004
  Refine = true
  Shapes = -> [Cut045,Extrude080]
FEATURE [Part::Extrusion] Extrude081  label="Extrude lato dx pistola - fori per inserto M3 x 3 x 4.5"
  Base = -> Sketch080
  Dir = (0,-1,2e-16)
  DirMode = 2
  FaceMakerClass = Part::FaceMakerBullseye
  FaceMakerMode = 3
  LengthFwd = 0.6
  LengthRev = 2.4
  Solid = true
  Symmetric = false
FEATURE [Part::Cut] Cut046
  Base = -> Fusion004
  Refine = true
  Tool = -> Extrude081
FEATURE [Sketcher::SketchObject] Sketch082  label="lato sx pistola - disegno anteriore"
  ArcFitTolerance = 1e-06
  AttachmentSupport = -> [XZ_Plane]
  ExternalGeometry = -> [Sketch074]
  FullyConstrained = true
  MakeInternals = false
  MapMode = 5
  Placement = pos=(0,0,0) rot=(1,0,0;1.5708rad)
  sketch-geometry (12):
    g0: ArcOfCircle CenterX=-65 CenterY=21.2 CenterZ=0 NormalX=0 NormalY=0 NormalZ=1 AngleXU=0 Radius=10 StartAngle=1.5708 EndAngle=4.71239
    g1: ArcOfCircle CenterX=-19 CenterY=21.2 CenterZ=0 NormalX=0 NormalY=0 NormalZ=1 AngleXU=0 Radius=10 StartAngle=4.71239 EndAngle=7.85398
    g2: LineSegment StartX=-65 StartY=31.2 StartZ=0 EndX=-19 EndY=31.2 EndZ=0
    g3: LineSegment StartX=-65 StartY=11.2 StartZ=0 EndX=-19 EndY=11.2 EndZ=0
    g4: LineSegment StartX=-82.8 StartY=3.2 StartZ=0 EndX=0 EndY=3.2 EndZ=0
    g5: LineSegment StartX=0 StartY=3.2 StartZ=0 EndX=0 EndY=39.2 EndZ=0
    g6: LineSegment StartX=0 StartY=39.2 StartZ=0 EndX=-82.8 EndY=39.2 EndZ=0
    g7: LineSegment StartX=-82.8 StartY=39.2 StartZ=0 EndX=-82.8 EndY=3.2 EndZ=0
    g8: Circle CenterX=-78.51 CenterY=34.8 CenterZ=0 NormalX=0 NormalY=0 NormalZ=1 AngleXU=0 Radius=1.8
    g9: Circle CenterX=-5.6 CenterY=34.8 CenterZ=0 NormalX=0 NormalY=0 NormalZ=1 AngleXU=0 Radius=1.8
    g10: Circle CenterX=-5.6 CenterY=7.6 CenterZ=0 NormalX=0 NormalY=0 NormalZ=1 AngleXU=0 Radius=1.8
    g11: Circle CenterX=-78.51 CenterY=7.6 CenterZ=0 NormalX=0 NormalY=0 NormalZ=1 AngleXU=0 Radius=1.8
  constraints (26):
    c: Tangent(g0,g2) = 1.5708
    c: Tangent(g0,g3) = -1.5708
    c: Tangent(g1,g2) = 1.5708
    c: Tangent(g1,g3) = -1.5708
    c: Equal(g0,g1)
    c: Coincident(g4,g5)
    c: Coincident(g5,g6)
    c: Coincident(g6,g7)
    c: Coincident(g7,g4)
    c: Horizontal(g4)
    c: Horizontal(g6)
    c: Vertical(g5)
    c: Vertical(g7)
    c: Coincident(g4,g-7)
    c: Coincident(g5,g-9)
    c: Diameter(g1) = 20
    c: Coincident(g1,g-5)
    c: Coincident(g0,g-4)
    c: Equal(g9,g-11)
    c: Equal(g10,g-12)
    c: Equal(g11,g-13)
    c: Equal(g8,g-10)
    c: Coincident(g8,g-10)
    c: Coincident(g11,g-13)
    c: Coincident(g10,g-12)
    c: Coincident(g9,g-11)
FEATURE [Sketcher::SketchObject] Sketch083  label="lato dx pistola - disegno anteriore"
  ArcFitTolerance = 1e-06
  AttachmentSupport = -> [XZ_Plane]
  ExternalGeometry = -> [Sketch082]
  FullyConstrained = true
  MakeInternals = false
  MapMode = 5
  Placement = pos=(0,0,0) rot=(1,0,0;1.5708rad)
  sketch-geometry (12):
    g0: LineSegment StartX=-82.8 StartY=3.2 StartZ=0 EndX=0 EndY=3.2 EndZ=0
    g1: LineSegment StartX=0 StartY=3.2 StartZ=0 EndX=0 EndY=39.2 EndZ=0
    g2: LineSegment StartX=0 StartY=39.2 StartZ=0 EndX=-82.8 EndY=39.2 EndZ=0
    g3: LineSegment StartX=-82.8 StartY=39.2 StartZ=0 EndX=-82.8 EndY=3.2 EndZ=0
    g4: ArcOfCircle CenterX=-65 CenterY=21.2 CenterZ=0 NormalX=0 NormalY=0 NormalZ=1 AngleXU=0 Radius=10 StartAngle=1.5708 EndAngle=4.71239
    g5: ArcOfCircle CenterX=-19 CenterY=21.2 CenterZ=0 NormalX=0 NormalY=0 NormalZ=1 AngleXU=0 Radius=10 StartAngle=4.71239 EndAngle=7.85398
    g6: LineSegment StartX=-65 StartY=31.2 StartZ=0 EndX=-19 EndY=31.2 EndZ=0
    g7: LineSegment StartX=-65 StartY=11.2 StartZ=0 EndX=-19 EndY=11.2 EndZ=0
    g8: Circle CenterX=-78.51 CenterY=34.8 CenterZ=0 NormalX=0 NormalY=0 NormalZ=1 AngleXU=0 Radius=1.8
    g9: Circle CenterX=-5.6 CenterY=34.8 CenterZ=0 NormalX=0 NormalY=0 NormalZ=1 AngleXU=0 Radius=1.8
    g10: Circle CenterX=-5.6 CenterY=7.6 CenterZ=0 NormalX=0 NormalY=0 NormalZ=1 AngleXU=0 Radius=1.8
    g11: Circle CenterX=-78.51 CenterY=7.6 CenterZ=0 NormalX=0 NormalY=0 NormalZ=1 AngleXU=0 Radius=1.8
  constraints (26):
    c: Coincident(g0,g1)
    c: Coincident(g1,g2)
    c: Coincident(g2,g3)
    c: Coincident(g3,g0)
    c: Horizontal(g0)
    c: Horizontal(g2)
    c: Vertical(g1)
    c: Vertical(g3)
    c: Coincident(g0,g-5)
    c: Coincident(g1,g-6)
    c: Tangent(g4,g6) = 1.5708
    c: Tangent(g4,g7) = -1.5708
    c: Tangent(g5,g6) = 1.5708
    c: Tangent(g5,g7) = -1.5708
    c: Equal(g4,g5)
    c: Equal(g5,g-9)
    c: Coincident(g5,g-9)
    c: Coincident(g4,g-8)
    c: Equal(g8,g-11)
    c: Equal(g11,g-12)
    c: Equal(g10,g-13)
    c: Equal(g9,g-14)
    c: Coincident(g9,g-14)
    c: Coincident(g10,g-13)
    c: Coincident(g11,g-12)
    c: Coincident(g8,g-11)
FEATURE [Sketcher::SketchObject] Sketch084  label="lato sx pistola - spazi anteriori per viti"
  ArcFitTolerance = 1e-06
  AttachmentSupport = -> [XZ_Plane]
  ExternalGeometry = -> [Sketch082]
  FullyConstrained = true
  MakeInternals = false
  MapMode = 5
  Placement = pos=(0,0,0) rot=(1,0,0;1.5708rad)
  sketch-geometry (24):
    g0: ArcOfCircle CenterX=-78.51 CenterY=34.8 CenterZ=0 NormalX=0 NormalY=0 NormalZ=1 AngleXU=0 Radius=3.5 StartAngle=4.71239 EndAngle=6.28319
    g1: ArcOfCircle CenterX=-5.6 CenterY=34.8 CenterZ=0 NormalX=0 NormalY=0 NormalZ=1 AngleXU=0 Radius=3.5 StartAngle=3.14159 EndAngle=4.71239
    g2: ArcOfCircle CenterX=-78.51 CenterY=7.6 CenterZ=0 NormalX=0 NormalY=0 NormalZ=1 AngleXU=0 Radius=3.5 StartAngle=3.99598e-11 EndAngle=1.5708
    g3: ArcOfCircle CenterX=-5.6 CenterY=7.6 CenterZ=0 NormalX=0 NormalY=0 NormalZ=1 AngleXU=0 Radius=3.5 StartAngle=1.5708 EndAngle=3.14159
    g4: LineSegment StartX=0 StartY=11.1 StartZ=0 EndX=-5.6 EndY=11.1 EndZ=0
    g5: LineSegment StartX=-9.1 StartY=7.6 StartZ=0 EndX=-9.1 EndY=3.2 EndZ=0
    g6: LineSegment StartX=-75.01 StartY=39.2 StartZ=0 EndX=-75.01 EndY=34.8 EndZ=0
    g7: LineSegment StartX=-82.8 StartY=31.3 StartZ=0 EndX=-78.51 EndY=31.3 EndZ=0
    g8: LineSegment StartX=-82.8 StartY=11.1 StartZ=0 EndX=-78.51 EndY=11.1 EndZ=0
    g9: LineSegment StartX=-75.01 StartY=7.6 StartZ=0 EndX=-75.01 EndY=3.2 EndZ=0
    g10: LineSegment StartX=-9.1 StartY=39.2 StartZ=0 EndX=-9.1 EndY=34.8 EndZ=0
    g11: LineSegment StartX=-5.6 StartY=31.3 StartZ=0 EndX=0 EndY=31.3 EndZ=0
    g12: LineSegment StartX=-9.1 StartY=39.2 StartZ=0 EndX=0 EndY=39.2 EndZ=0
    g13: LineSegment StartX=0 StartY=39.2 StartZ=0 EndX=0 EndY=31.3 EndZ=0
    g14: LineSegment StartX=0 StartY=11.1 StartZ=0 EndX=0 EndY=3.2 EndZ=0
    g15: LineSegment StartX=0 StartY=3.2 StartZ=0 EndX=-9.1 EndY=3.2 EndZ=0
    g16: LineSegment StartX=-75.01 StartY=3.2 StartZ=0 EndX=-82.8 EndY=3.2 EndZ=0
    g17: LineSegment StartX=-82.8 StartY=3.2 StartZ=0 EndX=-82.8 EndY=11.1 EndZ=0
    g18: LineSegment StartX=-82.8 StartY=31.3 StartZ=0 EndX=-82.8 EndY=39.2 EndZ=0
    g19: LineSegment StartX=-82.8 StartY=39.2 StartZ=0 EndX=-75.01 EndY=39.2 EndZ=0
    g20: Circle CenterX=-78.51 CenterY=34.8 CenterZ=0 NormalX=0 NormalY=0 NormalZ=1 AngleXU=0 Radius=1.8
    g21: Circle CenterX=-5.6 CenterY=34.8 CenterZ=0 NormalX=0 NormalY=0 NormalZ=1 AngleXU=0 Radius=1.8
    g22: Circle CenterX=-5.6 CenterY=7.6 CenterZ=0 NormalX=0 NormalY=0 NormalZ=1 AngleXU=0 Radius=1.8
    g23: Circle CenterX=-78.51 CenterY=7.6 CenterZ=0 NormalX=0 NormalY=0 NormalZ=1 AngleXU=0 Radius=1.8
  constraints (56):
    c: Radius(g0) = 3.5
    c: Coincident(g0,g-5)
    c: Radius(g1) = 3.5
    c: Coincident(g1,g-10)
    c: Radius(g2) = 3.5
    c: Coincident(g2,g-4)
    c: Radius(g3) = 3.5
    c: Coincident(g3,g-9)
    c: Horizontal(g4)
    c: Vertical(g5)
    c: Vertical(g6)
    c: Horizontal(g7)
    c: Horizontal(g8)
    c: Vertical(g9)
    c: Vertical(g10)
    c: Horizontal(g11)
    c: Tangent(g11,g1) = -1.5708
    c: Tangent(g1,g10) = -1.5708
    c: Tangent(g3,g5) = -1.5708
    c: Tangent(g3,g4) = -1.5708
    c: Tangent(g9,g2) = 1.5708
    c: Tangent(g8,g2) = 1.5708
    c: Tangent(g7,g0) = -1.5708
    c: Tangent(g0,g6) = 1.5708
    c: PointOnObject(g10,g-7)
    c: PointOnObject(g11,g-11)
    c: PointOnObject(g4,g-11)
    c: PointOnObject(g5,g-8)
    c: PointOnObject(g9,g-8)
    c: PointOnObject(g8,g-6)
    c: PointOnObject(g7,g-6)
    c: PointOnObject(g6,g-7)
    c: Coincident(g12,g10)
    c: Coincident(g12,g-11)
    c: Coincident(g13,g12)
    c: Coincident(g13,g11)
    c: Coincident(g14,g4)
    c: Coincident(g14,g-11)
    c: Coincident(g15,g14)
    c: Coincident(g15,g5)
    c: Coincident(g16,g9)
    c: Coincident(g16,g-8)
    c: Coincident(g17,g16)
    c: Coincident(g17,g8)
    c: Coincident(g18,g7)
    c: Coincident(g18,g-7)
    c: Coincident(g19,g18)
    c: Coincident(g19,g6)
    c: Equal(g21,g-10)
    c: Equal(g-9,g22)
    c: Equal(g23,g-4)
    c: Equal(g20,g-5)
    c: Coincident(g20,g0)
    c: Coincident(g21,g1)
    c: Coincident(g22,g3)
    c: Coincident(g23,g2)
FEATURE [Sketcher::SketchObject] Sketch085  label="lato dx pistola - spazi anteriori per viti"
  ArcFitTolerance = 1e-06
  AttachmentSupport = -> [XZ_Plane]
  ExternalGeometry = -> [Sketch083]
  FullyConstrained = true
  MakeInternals = false
  MapMode = 5
  Placement = pos=(0,0,0) rot=(1,0,0;1.5708rad)
  sketch-geometry (24):
    g0: ArcOfCircle CenterX=-78.51 CenterY=34.8 CenterZ=0 NormalX=0 NormalY=0 NormalZ=1 AngleXU=0 Radius=3.5 StartAngle=4.71239 EndAngle=6.28319
    g1: ArcOfCircle CenterX=-5.6 CenterY=34.8 CenterZ=0 NormalX=0 NormalY=0 NormalZ=1 AngleXU=0 Radius=3.5 StartAngle=3.14159 EndAngle=4.71239
    g2: ArcOfCircle CenterX=-78.51 CenterY=7.6 CenterZ=0 NormalX=0 NormalY=0 NormalZ=1 AngleXU=0 Radius=3.5 StartAngle=3.99599e-11 EndAngle=1.5708
    g3: ArcOfCircle CenterX=-5.6 CenterY=7.6 CenterZ=0 NormalX=0 NormalY=0 NormalZ=1 AngleXU=0 Radius=3.5 StartAngle=1.5708 EndAngle=3.14159
    g4: LineSegment StartX=-9.1 StartY=39.2 StartZ=0 EndX=-9.1 EndY=34.8 EndZ=0
    g5: LineSegment StartX=-5.6 StartY=31.3 StartZ=0 EndX=0 EndY=31.3 EndZ=0
    g6: LineSegment StartX=-5.6 StartY=11.1 StartZ=0 EndX=0 EndY=11.1 EndZ=0
    g7: LineSegment StartX=-9.1 StartY=7.6 StartZ=0 EndX=-9.1 EndY=3.2 EndZ=0
    g8: LineSegment StartX=-82.8 StartY=11.1 StartZ=0 EndX=-78.51 EndY=11.1 EndZ=0
    g9: LineSegment StartX=-75.01 StartY=7.6 StartZ=0 EndX=-75.01 EndY=3.2 EndZ=0
    g10: LineSegment StartX=-82.8 StartY=31.3 StartZ=0 EndX=-78.51 EndY=31.3 EndZ=0
    g11: LineSegment StartX=-75.01 StartY=34.8 StartZ=0 EndX=-75.01 EndY=39.2 EndZ=0
    g12: LineSegment StartX=-75.01 StartY=3.2 StartZ=0 EndX=-82.8 EndY=3.2 EndZ=0
    g13: LineSegment StartX=-82.8 StartY=3.2 StartZ=0 EndX=-82.8 EndY=11.1 EndZ=0
    g14: LineSegment StartX=-82.8 StartY=31.3 StartZ=0 EndX=-82.8 EndY=39.2 EndZ=0
    g15: LineSegment StartX=-82.8 StartY=39.2 StartZ=0 EndX=-75.01 EndY=39.2 EndZ=0
    g16: LineSegment StartX=-9.1 StartY=39.2 StartZ=0 EndX=0 EndY=39.2 EndZ=0
    g17: LineSegment StartX=0 StartY=39.2 StartZ=0 EndX=0 EndY=31.3 EndZ=0
    g18: LineSegment StartX=-9.1 StartY=3.2 StartZ=0 EndX=0 EndY=3.2 EndZ=0
    g19: LineSegment StartX=0 StartY=3.2 StartZ=0 EndX=0 EndY=11.1 EndZ=0
    g20: Circle CenterX=-78.51 CenterY=34.8 CenterZ=0 NormalX=0 NormalY=0 NormalZ=1 AngleXU=0 Radius=1.8
    g21: Circle CenterX=-5.6 CenterY=34.8 CenterZ=0 NormalX=0 NormalY=0 NormalZ=1 AngleXU=0 Radius=1.8
    g22: Circle CenterX=-5.6 CenterY=7.6 CenterZ=0 NormalX=0 NormalY=0 NormalZ=1 AngleXU=0 Radius=1.8
    g23: Circle CenterX=-78.51 CenterY=7.6 CenterZ=0 NormalX=0 NormalY=0 NormalZ=1 AngleXU=0 Radius=1.8
  constraints (56):
    c: Radius(g0) = 3.5
    c: Coincident(g0,g-3)
    c: Radius(g1) = 3.5
    c: Coincident(g1,g-5)
    c: Radius(g2) = 3.5
    c: Coincident(g2,g-4)
    c: Radius(g3) = 3.5
    c: Coincident(g3,g-6)
    c: Vertical(g4)
    c: Horizontal(g5)
    c: Horizontal(g6)
    c: Vertical(g7)
    c: Horizontal(g8)
    c: Vertical(g9)
    c: Horizontal(g10)
    c: Vertical(g11)
    c: Tangent(g4,g1) = -1.5708
    c: Tangent(g5,g1) = -1.5708
    c: Tangent(g6,g3) = 1.5708
    c: Tangent(g7,g3) = -1.5708
    c: Tangent(g9,g2) = 1.5708
    c: Tangent(g8,g2) = 1.5708
    c: Tangent(g10,g0) = -1.5708
    c: Tangent(g11,g0) = -1.5708
    c: PointOnObject(g11,g-9)
    c: PointOnObject(g4,g-9)
    c: PointOnObject(g5,g-10)
    c: PointOnObject(g6,g-10)
    c: PointOnObject(g7,g-7)
    c: PointOnObject(g9,g-7)
    c: PointOnObject(g8,g-8)
    c: PointOnObject(g10,g-8)
    c: Coincident(g12,g9)
    c: Coincident(g12,g-8)
    c: Coincident(g13,g12)
    c: Coincident(g13,g8)
    c: Coincident(g14,g10)
    c: Coincident(g14,g-9)
    c: Coincident(g15,g14)
    c: Coincident(g15,g11)
    c: Coincident(g16,g4)
    c: Coincident(g16,g-10)
    c: Coincident(g17,g16)
    c: Coincident(g17,g5)
    c: Coincident(g18,g7)
    c: Coincident(g18,g-10)
    c: Coincident(g19,g18)
    c: Coincident(g19,g6)
    c: Equal(g20,g-3)
    c: Equal(g21,g-5)
    c: Equal(g22,g-6)
    c: Equal(g23,g-4)
    c: Coincident(g20,g0)
    c: Coincident(g21,g1)
    c: Coincident(g22,g3)
    c: Coincident(g23,g2)
FEATURE [Part::Extrusion] Extrude082  label="Extrude lato sx pistola - disegno anteriore"
  Base = -> Sketch082
  Dir = (0,-1,2e-16)
  DirMode = 2
  FaceMakerClass = Part::FaceMakerBullseye
  FaceMakerMode = 3
  LengthFwd = -1.6
  LengthRev = 0
  Placement = pos=(0,2,0) rot=(0,0,1;0rad)
  Solid = true
  Symmetric = false
FEATURE [Part::Extrusion] Extrude083  label="Extrude lato dx pistola - disegno anteriore"
  Base = -> Sketch083
  Dir = (0,-1,2e-16)
  DirMode = 2
  FaceMakerClass = Part::FaceMakerBullseye
  FaceMakerMode = 3
  LengthFwd = 1.6
  LengthRev = 0
  Placement = pos=(0,-2,0) rot=(0,0,1;0rad)
  Solid = true
  Symmetric = false
FEATURE [Part::Extrusion] Extrude084  label="Extrude lato sx pistola - spazi anteriori per viti"
  Base = -> Sketch084
  Dir = (0,-1,2e-16)
  DirMode = 2
  FaceMakerClass = Part::FaceMakerBullseye
  FaceMakerMode = 3
  LengthFwd = -1.6
  LengthRev = 0
  Placement = pos=(0,2,0) rot=(0,0,1;0rad)
  Solid = true
  Symmetric = false
FEATURE [Part::Extrusion] Extrude085  label="Extrude lato dx pistola - spazi anteriori per viti"
  Base = -> Sketch085
  Dir = (0,-1,2e-16)
  DirMode = 2
  FaceMakerClass = Part::FaceMakerBullseye
  FaceMakerMode = 3
  LengthFwd = 0.8
  LengthRev = 0
  Placement = pos=(0,-2.8,0) rot=(0,0,1;0rad)
  Solid = true
  Symmetric = false
FEATURE [Part::Cut] Cut048  label="Extrude lato dx pistola - disegno anterioro con fori viti"
  Base = -> Extrude083
  Refine = true
  Tool = -> Extrude085
FEATURE [Part::MultiFuse] Fusion006
  Refine = true
  Shapes = -> [Cut046,Cut048]
FEATURE [Sketcher::SketchObject] Sketch087  label="lato sx pistola - rialzo posteriore"
  ArcFitTolerance = 1e-06
  AttachmentSupport = -> [XZ_Plane]
  ExternalGeometry = -> [Sketch074]
  FullyConstrained = true
  MakeInternals = false
  MapMode = 5
  Placement = pos=(0,0,0) rot=(1,0,0;1.5708rad)
  sketch-geometry (10):
    g0: LineSegment StartX=-181.33 StartY=20.0744 StartZ=0 EndX=-144.029 EndY=20.0744 EndZ=0
    g1: LineSegment StartX=-137.815 StartY=39.2 StartZ=0 EndX=-144.029 EndY=20.0744 EndZ=0
    g2: LineSegment StartX=-178.754 StartY=39.2 StartZ=0 EndX=-137.815 EndY=39.2 EndZ=0
    g3: ArcOfCircle CenterX=-184.08 CenterY=34.8 CenterZ=0 NormalX=0 NormalY=0 NormalZ=1 AngleXU=0 Radius=3.5 StartAngle=4.71239 EndAngle=5.93412
    g4: LineSegment StartX=-178.754 StartY=39.2 StartZ=0 EndX=-180.791 EndY=33.6029 EndZ=0
    g5: GeomPoint [constr] X=-181.33 Y=20.0744 Z=0
    g6: LineSegment [constr] StartX=-181.33 StartY=20.0744 StartZ=0 EndX=-192.176 EndY=-3.18451 EndZ=0
    g7: LineSegment StartX=-184.08 StartY=31.3 StartZ=0 EndX=-186.139 EndY=31.3 EndZ=0
    g8: LineSegment StartX=-186.139 StartY=31.3 StartZ=0 EndX=-190.224 EndY=20.0744 EndZ=0
    g9: LineSegment StartX=-181.33 StartY=20.0744 StartZ=0 EndX=-190.224 EndY=20.0744 EndZ=0
  constraints (23):
    c: Horizontal(g0)
    c: Tangent(g1,g-5)
    c: PointOnObject(g2,g-4)
    c: Coincident(g2,g1)
    c: Radius(g3) = 3.5
    c: Coincident(g3,g-10)
    c: Horizontal(g2)
    c: Equal(g1,g-3)
    c: Coincident(g0,g1)
    c: Tangent(g4,g3) = 1.5708
    c: Coincident(g4,g2)
    c: Coincident(g6,g5)
    c: Tangent(g6,g-11) = -1.5708
    c: Coincident(g0,g5)
    c: Parallel(g4,g-3)
    c: Horizontal(g7)
    c: Parallel(g8,g-3)
    c: Tangent(g3,g7) = 1.5708
    c: Coincident(g8,g7)
    c: Coincident(g9,g0)
    c: Horizontal(g9)
    c: Coincident(g9,g8)
    c: DistanceX(g-8,g7) = 3.8
FEATURE [Sketcher::SketchObject] Sketch086  label="lato sx pistola - rialzo centrale"
  ArcFitTolerance = 1e-06
  AttachmentOffset = pos=(0,2,0) rot=(0,0,1;0rad)
  AttachmentSupport = -> [XZ_Plane]
  ExternalGeometry = -> [Sketch074,Sketch087]
  FullyConstrained = true
  MakeInternals = false
  MapMode = 5
  Placement = pos=(0,4e-16,2) rot=(1,0,0;1.5708rad)
  sketch-geometry (6):
    g0: LineSegment StartX=-137.815 StartY=37.2 StartZ=0 EndX=-142.793 EndY=21.8787 EndZ=0
    g1: LineSegment StartX=-137.815 StartY=37.2 StartZ=0 EndX=-110.815 EndY=37.2 EndZ=0
    g2: LineSegment StartX=-110.815 StartY=37.2 StartZ=0 EndX=-112.201 EndY=32.9344 EndZ=0
    g3: LineSegment StartX=-127.418 StartY=21.8787 StartZ=0 EndX=-142.793 EndY=21.8787 EndZ=0
    g4: ArcOfCircle CenterX=-127.418 CenterY=37.8787 CenterZ=0 NormalX=0 NormalY=0 NormalZ=1 AngleXU=0 Radius=16 StartAngle=4.71239 EndAngle=5.96903
    g5: GeomPoint [constr] X=-115.793 Y=21.8787 Z=0
  constraints (15):
    c: Distance(g1) = 27
    c: Coincident(g1,g0)
    c: PointOnObject(g1,g-4)
    c: Parallel(g2,g-3)
    c: Coincident(g2,g1)
    c: Horizontal(g3)
    c: PointOnObject(g5,g2)
    c: PointOnObject(g5,g3)
    c: Tangent(g2,g4) = 1.5708
    c: Tangent(g3,g4) = 1.5708
    c: Radius(g4) = 16
    c: Parallel(g0,g-7)
    c: Coincident(g0,g-7)
    c: Coincident(g0,g3)
    c: Distance(g0,g-7) = 4
FEATURE [Sketcher::SketchObject] Sketch088  label="lato sx pistola - rialzo impugnatura"
  ArcFitTolerance = 1e-06
  AttachmentSupport = -> [XZ_Plane]
  ExternalGeometry = -> [Sketch074,Sketch087]
  FullyConstrained = true
  MakeInternals = false
  MapMode = 5
  Placement = pos=(0,0,0) rot=(1,0,0;1.5708rad)
  sketch-geometry (11):
    g0: LineSegment StartX=-144.029 StartY=20.0744 StartZ=0 EndX=-176.685 EndY=-80.4316 EndZ=0
    g1: Circle CenterX=-213.443 CenterY=-76.8316 CenterZ=0 NormalX=0 NormalY=0 NormalZ=1 AngleXU=0 Radius=3
    g2: Circle CenterX=-179.305 CenterY=-76.8316 CenterZ=0 NormalX=0 NormalY=0 NormalZ=1 AngleXU=0 Radius=3
    g3: LineSegment StartX=-176.685 StartY=-80.4316 StartZ=0 EndX=-215.932 EndY=-80.4316 EndZ=0
    g4: LineSegment StartX=-192.176 StartY=-3.18451 StartZ=0 EndX=-215.42 EndY=-53.0314 EndZ=0
    g5: ArcOfCircle CenterX=-184.801 CenterY=-67.3089 CenterZ=0 NormalX=0 NormalY=0 NormalZ=1 AngleXU=0 Radius=33.7833 StartAngle=2.70526 EndAngle=3.54053
    g6: LineSegment [constr] StartX=-192.176 StartY=-3.18451 StartZ=0 EndX=-181.33 EndY=20.0744 EndZ=0
    g7: LineSegment StartX=-144.029 StartY=20.0744 StartZ=0 EndX=-190.224 EndY=20.0744 EndZ=0
    g8: LineSegment StartX=-190.224 StartY=20.0744 StartZ=0 EndX=-191.316 EndY=17.0744 EndZ=0
    g9: LineSegment StartX=-191.316 StartY=17.0744 StartZ=0 EndX=-182.729 EndY=17.0744 EndZ=0
    g10: LineSegment StartX=-192.176 StartY=-3.18451 StartZ=0 EndX=-182.729 EndY=17.0744 EndZ=0
  constraints (26):
    c: Coincident(g0,g-5)
    c: Coincident(g2,g-10)
    c: Coincident(g1,g-9)
    c: Diameter(g2) = 6
    c: Diameter(g1) = 6
    c: Coincident(g3,g0)
    c: Coincident(g3,g-4)
    c: Equal(g4,g-15)
    c: Parallel(g4,g-15)
    c: Coincident(g4,g-15)
    c: Coincident(g5,g4)
    c: Coincident(g5,g3)
    c: Tangent(g6,g4) = 1.5708
    c: PointOnObject(g6,g-13)
    c: Coincident(g0,g-13)
    c: Coincident(g7,g0)
    c: Coincident(g7,g-14)
    c: Coincident(g8,g7)
    c: Coincident(g9,g8)
    c: Horizontal(g9)
    c: PointOnObject(g9,g6)
    c: Coincident(g10,g4)
    c: Coincident(g10,g9)
    c: DistanceY(g8,g8) = 3
    c: Parallel(g8,g-16)
    c: Tangent(g5,g-3)
FEATURE [Sketcher::SketchObject] Sketch089  label="lato sx pistola - disegno centrale"
  ArcFitTolerance = 1e-06
  AttachmentSupport = -> [XZ_Plane]
  ExternalGeometry = -> [Sketch086]
  FullyConstrained = true
  MakeInternals = false
  MapMode = 5
  Placement = pos=(0,0,0) rot=(1,0,0;1.5708rad)
  sketch-geometry (4):
    g0: LineSegment StartX=-130.215 StartY=39.2 StartZ=0 EndX=-119.215 EndY=39.2 EndZ=0
    g1: LineSegment StartX=-130.215 StartY=39.2 StartZ=0 EndX=-132.81 EndY=31.2111 EndZ=0
    g2: LineSegment StartX=-119.215 StartY=39.2 StartZ=0 EndX=-121.81 EndY=31.2111 EndZ=0
    g3: LineSegment StartX=-132.81 StartY=31.2111 StartZ=0 EndX=-121.81 EndY=31.2111 EndZ=0
  constraints (11):
    c: Horizontal(g3)
    c: Parallel(g2,g-4)
    c: Parallel(g1,g-4)
    c: Distance(g1) = 8.4
    c: DistanceX(g0,g0) = 11
    c: Tangent(g0,g-3)
    c: Coincident(g1,g0)
    c: Coincident(g2,g0)
    c: Coincident(g3,g1)
    c: Coincident(g3,g2)
    c: DistanceX(g0,g-4) = 8.4
FEATURE [Sketcher::SketchObject] Sketch090  label="lato sx pistola - disegno pre centrale"
  ArcFitTolerance = 1e-06
  AttachmentSupport = -> [XZ_Plane]
  ExternalGeometry = -> [Sketch074,Sketch086]
  FullyConstrained = true
  MakeInternals = false
  MapMode = 5
  Placement = pos=(0,0,0) rot=(1,0,0;1.5708rad)
  sketch-geometry (4):
    g0: LineSegment StartX=-106.615 StartY=36.8 StartZ=0 EndX=-89.6146 EndY=36.8 EndZ=0
    g1: LineSegment StartX=-110.254 StartY=26.8 StartZ=0 EndX=-89.6146 EndY=26.8 EndZ=0
    g2: LineSegment StartX=-106.615 StartY=36.8 StartZ=0 EndX=-110.254 EndY=26.8 EndZ=0
    g3: ArcOfCircle CenterX=-94.6146 CenterY=31.8 CenterZ=0 NormalX=0 NormalY=0 NormalZ=1 AngleXU=0 Radius=7.07107 StartAngle=5.49779 EndAngle=7.06858
  constraints (13):
    c: Horizontal(g0)
    c: Horizontal(g1)
    c: Parallel(g-3,g2)
    c: Coincident(g0,g2)
    c: DistanceY(g2,g2) = 10
    c: Coincident(g1,g2)
    c: DistanceX(g0,g0) = 17
    c: DistanceX(g0,g1) = 0
    c: Coincident(g3,g1)
    c: DistanceX(g-5,g0) = 4.2
    c: DistanceY(g0,g-5) = 2.4
    c: Coincident(g3,g0)
    c: DistanceX(g3,g0) = 5
FEATURE [PartDesign::Body] Body  label="Struttura pistola"
  AllowCompound = false
  Group = -> [Sketch,Sketch002,Sketch004,DatumPlane,Sketch005,DatumPlane001,CopyCut,Sketch008,Sketch009,Sketch010,Sketch011,Sketch012,Sketch013,Sketch014,Sketch015,Sketch016,Sketch017,Sketch018,Sketch019,Sketch020,Sketch022,Sketch023,Sketch024,Sketch025,Sketch026,Sketch027,Sketch029,Sketch030,Sketch031,Sketch032,Sketch033,Sketch034,Sketch035,Sketch036,Sketch037,Sketch038,Sketch039,Sketch040,Sketch041,Sketch042,+28 more]
  Origin = -> Origin
FEATURE [PartDesign::SubShapeBinder] Binder
  BindCopyOnChange = 0
  BindMode = 0
  ClaimChildren = false
  Context = -> Body006 [Binder.]
  Fuse = false
  MakeFace = true
  OffsetFill = false
  OffsetIntersection = false
  OffsetJoinType = 0
  OffsetOpenResult = false
  PartialLoad = false
  Refine = true
  Relative = true
  Support = -> [Body[Sketch074.]]
  _Version = 2
FEATURE [PartDesign::SubShapeBinder] Binder001
  BindCopyOnChange = 0
  BindMode = 0
  ClaimChildren = false
  Context = -> Body007 [Binder001.]
  Fuse = false
  MakeFace = true
  OffsetFill = false
  OffsetIntersection = false
  OffsetJoinType = 0
  OffsetOpenResult = false
  PartialLoad = false
  Refine = true
  Relative = true
  Support = -> [Body[Sketch075.]]
  _Version = 2
FEATURE [Mesh::Feature] logo_per_PCB_definitivo_positivo
  Placement = pos=(-191,17,-66) rot=(0,1,1;0rad)
FEATURE [Sketcher::SketchObject] Sketch114  label="Sketch114 - base lato DX"
  ArcFitTolerance = 1e-06
  AttachmentSupport = -> [Binder001]
  ExternalGeometry = -> [Binder001]
  FullyConstrained = true
  MakeInternals = false
  MapMode = 5
  Placement = pos=(0,1e-15,0) rot=(0,0.707107,0.707107;3.14159rad)
  sketch-geometry (30):
    g0: Circle CenterX=5.6 CenterY=34.8 CenterZ=0 NormalX=0 NormalY=0 NormalZ=1 AngleXU=0 Radius=1.8
    g1: Circle CenterX=5.6 CenterY=7.6 CenterZ=0 NormalX=0 NormalY=0 NormalZ=1 AngleXU=0 Radius=1.8
    g2: Circle CenterX=24.2 CenterY=26.7 CenterZ=0 NormalX=0 NormalY=0 NormalZ=1 AngleXU=0 Radius=3
    g3: Circle CenterX=24.2 CenterY=15.7 CenterZ=0 NormalX=0 NormalY=0 NormalZ=1 AngleXU=0 Radius=3
    g4: Circle CenterX=36.2 CenterY=21.2 CenterZ=0 NormalX=0 NormalY=0 NormalZ=1 AngleXU=0 Radius=2.8
    g5: Circle CenterX=78.51 CenterY=34.8 CenterZ=0 NormalX=0 NormalY=0 NormalZ=1 AngleXU=0 Radius=1.8
    g6: Circle CenterX=78.51 CenterY=7.6 CenterZ=0 NormalX=0 NormalY=0 NormalZ=1 AngleXU=0 Radius=1.8
    g7: Circle CenterX=184.08 CenterY=34.8 CenterZ=0 NormalX=0 NormalY=0 NormalZ=1 AngleXU=0 Radius=1.8
    g8: Circle CenterX=213.443 CenterY=-76.8316 CenterZ=0 NormalX=0 NormalY=0 NormalZ=1 AngleXU=0 Radius=1.8
    g9: Circle CenterX=179.305 CenterY=-76.8316 CenterZ=0 NormalX=0 NormalY=0 NormalZ=1 AngleXU=0 Radius=1.8
    g10: ArcOfCircle [constr] CenterX=132.428 CenterY=4 CenterZ=0 NormalX=0 NormalY=0 NormalZ=1 AngleXU=0 Radius=16 StartAngle=0.314159 EndAngle=1.5708
    g11: ArcOfCircle CenterX=107.6 CenterY=4 CenterZ=0 NormalX=0 NormalY=0 NormalZ=1 AngleXU=0 Radius=16 StartAngle=1.5708 EndAngle=3.00366
    g12: ArcOfCircle CenterX=207.583 CenterY=4 CenterZ=0 NormalX=0 NormalY=0 NormalZ=1 AngleXU=0 Radius=17 StartAngle=1.85815 EndAngle=3.57792
    g13: ArcOfCircle CenterX=184.801 CenterY=-67.3089 CenterZ=0 NormalX=0 NormalY=0 NormalZ=1 AngleXU=0 Radius=33.7833 StartAngle=5.88425 EndAngle=6.71952
    g14: LineSegment StartX=0 StartY=39.2 StartZ=0 EndX=0 EndY=3.2 EndZ=0
    g15: LineSegment StartX=0 StartY=3.2 StartZ=0 EndX=82.8 EndY=3.2 EndZ=0
    g16: LineSegment StartX=82.8 StartY=3.2 StartZ=0 EndX=82.8 EndY=6.2 EndZ=0
    g17: LineSegment StartX=82.8 StartY=6.2 StartZ=0 EndX=91.752 EndY=6.2 EndZ=0
    g18: LineSegment StartX=107.6 StartY=20 StartZ=0 EndX=132.428 EndY=20 EndZ=0
    g19: LineSegment StartX=147.645 StartY=8.94427 StartZ=0 EndX=176.685 EndY=-80.4316 EndZ=0
    g20: LineSegment StartX=176.685 StartY=-80.4316 StartZ=0 EndX=215.932 EndY=-80.4316 EndZ=0
    g21: LineSegment StartX=215.42 StartY=-53.0314 StartZ=0 EndX=192.176 EndY=-3.18451 EndZ=0
    g22: LineSegment StartX=202.765 StartY=20.303 StartZ=0 EndX=195.887 EndY=39.2 EndZ=0
    g23: LineSegment StartX=195.887 StartY=39.2 StartZ=0 EndX=0 EndY=39.2 EndZ=0
    g24: LineSegment StartX=196.467 StartY=26.4942 StartZ=0 EndX=194.073 EndY=33.0721 EndZ=0
    g25: LineSegment StartX=194.073 StartY=33.0721 StartZ=0 EndX=189.939 EndY=31.5672 EndZ=0
    g26: LineSegment StartX=189.939 StartY=31.5672 StartZ=0 EndX=192.333 EndY=24.9893 EndZ=0
    g27: LineSegment StartX=192.333 StartY=24.9893 StartZ=0 EndX=196.467 EndY=26.4942 EndZ=0
    g28: LineSegment StartX=132.428 StartY=20 StartZ=0 EndX=144.053 EndY=20 EndZ=0
    g29: LineSegment StartX=144.053 StartY=20 StartZ=0 EndX=147.645 EndY=8.94427 EndZ=0
  constraints (65):
    c: Equal(g0,g-25)
    c: Equal(g2,g-29)
    c: Equal(g3,g-30)
    c: Equal(g4,g-28)
    c: Equal(g1,g-26)
    c: Coincident(g0,g-25)
    c: Coincident(g1,g-26)
    c: Coincident(g2,g-29)
    c: Coincident(g3,g-30)
    c: Coincident(g4,g-28)
    c: Equal(g5,g-23)
    c: Equal(g6,g-24)
    c: Coincident(g5,g-23)
    c: Coincident(g6,g-24)
    c: Equal(g7,g-20)
    c: Coincident(g7,g-20)
    c: Equal(g9,g-22)
    c: Coincident(g9,g-22)
    c: Equal(g8,g-21)
    c: Coincident(g8,g-21)
    c: Equal(g13,g-12)
    c: Equal(g12,g-14)
    c: Equal(g10,g-9)
    c: Equal(g11,g-7)
    c: Coincident(g14,g-27)
    c: Coincident(g14,g-27)
    c: Coincident(g15,g14)
    c: Coincident(g15,g-5)
    c: Coincident(g16,g15)
    c: Coincident(g16,g-6)
    c: Coincident(g17,g16)
    c: Coincident(g17,g-7)
    c: Coincident(g11,g17)
    c: Coincident(g11,g-8)
    c: Coincident(g18,g11)
    c: Coincident(g18,g-9)
    c: Coincident(g10,g18)
    c: Coincident(g10,g-10)
    c: Coincident(g19,g10)
    c: Coincident(g19,g-11)
    c: Coincident(g20,g19)
    c: Coincident(g20,g-12)
    c: Coincident(g13,g20)
    c: Coincident(g13,g-13)
    c: Coincident(g21,g13)
    c: Coincident(g21,g-14)
    c: Coincident(g12,g21)
    c: Coincident(g12,g-15)
    c: Coincident(g22,g12)
    c: Coincident(g22,g-15)
    c: Coincident(g23,g22)
    c: Coincident(g23,g14)
    c: Coincident(g24,g-18)
    c: Coincident(g24,g-16)
    c: Coincident(g25,g24)
    c: Coincident(g25,g-19)
    c: Coincident(g26,g25)
    c: Coincident(g26,g-19)
    c: Coincident(g27,g26)
    c: Coincident(g27,g24)
    c: Coincident(g29,g10)
    c: Coincident(g28,g10)
    c: Coincident(g29,g28)
    c: Parallel(g28,g18)
    c: Parallel(g29,g19)
FEATURE [PartDesign::Pad] Pad011
  Direction = (0,1,-2e-16)
  Length = 2
  Length2 = 10
  Profile = -> Sketch114
  ReferenceAxis = -> Sketch114 [N_Axis]
  Refine = true
  Reversed = true
  Suppressed = false
  Type = 0
FEATURE [Sketcher::SketchObject] Sketch115
  ArcFitTolerance = 1e-06
  AttachmentSupport = -> [Pad011]
  ExternalGeometry = -> [Binder001]
  FullyConstrained = true
  MakeInternals = false
  MapMode = 5
  Placement = pos=(0,1.7e-15,0) rot=(0,0.707107,0.707107;3.14159rad)
  sketch-geometry (4):
    g0: ArcOfCircle CenterX=24.2 CenterY=26.7 CenterZ=0 NormalX=0 NormalY=0 NormalZ=1 AngleXU=0 Radius=3 StartAngle=4.48384e-08 EndAngle=3.14159
    g1: ArcOfCircle CenterX=24.2 CenterY=15.7 CenterZ=0 NormalX=0 NormalY=0 NormalZ=1 AngleXU=0 Radius=3 StartAngle=3.14159 EndAngle=6.28318
    g2: LineSegment StartX=21.2 StartY=26.7 StartZ=0 EndX=21.2 EndY=15.7 EndZ=0
    g3: LineSegment StartX=27.2 StartY=26.7 StartZ=0 EndX=27.2 EndY=15.7 EndZ=0
  constraints (12):
    c: Equal(g1,g-4)
    c: Equal(g0,g-3)
    c: Coincident(g0,g-3)
    c: Coincident(g1,g-4)
    c: Vertical(g2)
    c: Vertical(g3)
    c: Tangent(g3,g-3)
    c: Tangent(g2,g-3)
    c: Coincident(g0,g2)
    c: Coincident(g0,g3)
    c: Coincident(g1,g2)
    c: Coincident(g3,g1)
FEATURE [Sketcher::SketchObject] Sketch117
  ArcFitTolerance = 1e-06
  AttachmentSupport = -> [Pad011]
  ExternalGeometry = -> [Binder001]
  FullyConstrained = true
  MakeInternals = false
  MapMode = 5
  Placement = pos=(0,1.7e-15,0) rot=(0,0.707107,0.707107;3.14159rad)
  sketch-geometry (4):
    g0: Circle CenterX=43.2 CenterY=30.3 CenterZ=0 NormalX=0 NormalY=0 NormalZ=1 AngleXU=0 Radius=2.25
    g1: Circle CenterX=43.2 CenterY=12.1 CenterZ=0 NormalX=0 NormalY=0 NormalZ=1 AngleXU=0 Radius=2.25
    g2: Circle CenterX=18.6 CenterY=30.3 CenterZ=0 NormalX=0 NormalY=0 NormalZ=1 AngleXU=0 Radius=2.25
    g3: Circle CenterX=18.6 CenterY=12.1 CenterZ=0 NormalX=0 NormalY=0 NormalZ=1 AngleXU=0 Radius=2.25
  constraints (8):
    c: Diameter(g0) = 4.5
    c: Diameter(g1) = 4.5
    c: Diameter(g2) = 4.5
    c: Diameter(g3) = 4.5
    c: Coincident(g2,g-3)
    c: Coincident(g3,g-6)
    c: Coincident(g0,g-4)
    c: Coincident(g1,g-5)
FEATURE [Sketcher::SketchObject] Sketch118
  ArcFitTolerance = 1e-06
  AttachmentSupport = -> [Pad011]
  ExternalGeometry = -> [Binder001]
  FullyConstrained = true
  MakeInternals = false
  MapMode = 5
  Placement = pos=(0,-2,0) rot=(1,0,0;1.5708rad)
  sketch-geometry (12):
    g0: Circle CenterX=-78.51 CenterY=34.8 CenterZ=0 NormalX=0 NormalY=0 NormalZ=1 AngleXU=0 Radius=1.8
    g1: Circle CenterX=-78.51 CenterY=7.6 CenterZ=0 NormalX=0 NormalY=0 NormalZ=1 AngleXU=0 Radius=1.8
    g2: Circle CenterX=-5.6 CenterY=34.8 CenterZ=0 NormalX=0 NormalY=0 NormalZ=1 AngleXU=0 Radius=1.8
    g3: Circle CenterX=-5.6 CenterY=7.6 CenterZ=0 NormalX=0 NormalY=0 NormalZ=1 AngleXU=0 Radius=1.8
    g4: LineSegment StartX=0 StartY=39.2 StartZ=0 EndX=0 EndY=3.2 EndZ=0
    g5: LineSegment StartX=0 StartY=3.2 StartZ=0 EndX=-82.8 EndY=3.2 EndZ=0
    g6: LineSegment StartX=-82.8 StartY=3.2 StartZ=0 EndX=-82.8 EndY=39.2 EndZ=0
    g7: LineSegment StartX=-82.8 StartY=39.2 StartZ=0 EndX=0 EndY=39.2 EndZ=0
    g8: ArcOfCircle CenterX=-65 CenterY=21.2 CenterZ=0 NormalX=0 NormalY=0 NormalZ=1 AngleXU=0 Radius=10 StartAngle=1.5708 EndAngle=4.71239
    g9: ArcOfCircle CenterX=-19 CenterY=21.2 CenterZ=0 NormalX=0 NormalY=0 NormalZ=1 AngleXU=0 Radius=10 StartAngle=4.71239 EndAngle=7.85398
    g10: LineSegment StartX=-65 StartY=31.2 StartZ=0 EndX=-19 EndY=31.2 EndZ=0
    g11: LineSegment StartX=-65 StartY=11.2 StartZ=0 EndX=-19 EndY=11.2 EndZ=0
  constraints (25):
    c: Equal(g2,g-5)
    c: Equal(g3,g-7)
    c: Equal(g1,g-6)
    c: Equal(g0,g-4)
    c: Coincident(g0,g-4)
    c: Coincident(g1,g-6)
    c: Coincident(g3,g-7)
    c: Coincident(g2,g-5)
    c: Coincident(g4,g-8)
    c: Coincident(g4,g-9)
    c: Coincident(g5,g4)
    c: Coincident(g5,g-10)
    c: Coincident(g6,g5)
    c: PointOnObject(g6,g-3)
    c: Vertical(g6)
    c: Coincident(g7,g6)
    c: Coincident(g7,g4)
    c: Tangent(g8,g10) = 1.5708
    c: Tangent(g8,g11) = -1.5708
    c: Tangent(g9,g10) = 1.5708
    c: Tangent(g9,g11) = -1.5708
    c: Equal(g8,g9)
    c: Radius(g8) = 10
    c: Coincident(g8,g-11)
    c: Coincident(g9,g-12)
FEATURE [Sketcher::SketchObject] Sketch120
  ArcFitTolerance = 1e-06
  AttachmentSupport = -> [Pad011]
  ExternalGeometry = -> [Binder001]
  FullyConstrained = true
  MakeInternals = false
  MapMode = 5
  Placement = pos=(0,-2,0) rot=(1,0,0;1.5708rad)
  sketch-geometry (4):
    g0: LineSegment StartX=-137.815 StartY=39.2 StartZ=0 EndX=-142.655 EndY=24.303 EndZ=0
    g1: LineSegment StartX=-137.815 StartY=39.2 StartZ=0 EndX=-110.815 EndY=39.2 EndZ=0
    g2: LineSegment StartX=-142.655 StartY=24.303 StartZ=0 EndX=-110.815 EndY=24.303 EndZ=0
    g3: ArcOfCircle CenterX=-92.2534 CenterY=31.7515 CenterZ=0 NormalX=0 NormalY=0 NormalZ=1 AngleXU=0 Radius=20 StartAngle=2.75997 EndAngle=3.52321
  constraints (12):
    c: PointOnObject(g0,g-3)
    c: Coincident(g1,g0)
    c: PointOnObject(g1,g-3)
    c: Coincident(g2,g0)
    c: Horizontal(g2)
    c: Tangent(g0,g-4)
    c: Vertical(g2,g1)
    c: DistanceX(g1,g1) = 27
    c: DistanceY(g-6,g0) = 4
    c: Radius(g3) = 20
    c: Coincident(g3,g1)
    c: Coincident(g3,g2)
FEATURE [Sketcher::SketchObject] Sketch121
  ArcFitTolerance = 1e-06
  AttachmentSupport = -> [Pad011]
  ExternalGeometry = -> [Binder001]
  FullyConstrained = true
  MakeInternals = false
  MapMode = 5
  Placement = pos=(0,-2,0) rot=(1,0,0;1.5708rad)
  sketch-geometry (15):
    g0: LineSegment StartX=-137.815 StartY=39.2 StartZ=0 EndX=-143.955 EndY=20.303 EndZ=0
    g1: LineSegment StartX=-143.955 StartY=20.303 StartZ=0 EndX=-190.141 EndY=20.303 EndZ=0
    g2: LineSegment StartX=-190.141 StartY=20.303 StartZ=0 EndX=-186.139 EndY=31.3 EndZ=0
    g3: LineSegment StartX=-178.754 StartY=39.2 StartZ=0 EndX=-180.791 EndY=33.6029 EndZ=0
    g4: ArcOfCircle CenterX=-184.08 CenterY=34.8 CenterZ=0 NormalX=0 NormalY=0 NormalZ=1 AngleXU=0 Radius=3.5 StartAngle=4.71239 EndAngle=5.93412
    g5: LineSegment StartX=-184.08 StartY=31.3 StartZ=0 EndX=-186.139 EndY=31.3 EndZ=0
    g6: LineSegment StartX=-137.815 StartY=39.2 StartZ=0 EndX=-156.815 EndY=39.2 EndZ=0
    g7: LineSegment StartX=-168.815 StartY=39.2 StartZ=0 EndX=-178.754 EndY=39.2 EndZ=0
    g8: LineSegment StartX=-157.815 StartY=39.2 StartZ=0 EndX=-167.815 EndY=39.2 EndZ=0
    g9: LineSegment StartX=-168.815 StartY=31.2 StartZ=0 EndX=-156.815 EndY=31.2 EndZ=0
    g10: LineSegment StartX=-167.436 StartY=36.2 StartZ=0 EndX=-157.436 EndY=36.2 EndZ=0
    g11: ArcOfCircle CenterX=-176.411 CenterY=35.2 CenterZ=0 NormalX=0 NormalY=0 NormalZ=1 AngleXU=0 Radius=20 StartAngle=6.08183 EndAngle=6.48454
    g12: ArcOfCircle CenterX=-188.411 CenterY=35.2 CenterZ=0 NormalX=0 NormalY=0 NormalZ=1 AngleXU=0 Radius=20 StartAngle=6.08183 EndAngle=6.48454
    g13: ArcOfCircle CenterX=-177.411 CenterY=35.2 CenterZ=0 NormalX=0 NormalY=0 NormalZ=1 AngleXU=0 Radius=20 StartAngle=0.0500209 EndAngle=0.201358
    g14: ArcOfCircle CenterX=-187.411 CenterY=35.2 CenterZ=0 NormalX=0 NormalY=0 NormalZ=1 AngleXU=0 Radius=20 StartAngle=0.0500209 EndAngle=0.201358
  constraints (46):
    c: PointOnObject(g0,g-3)
    c: Tangent(g0,g-5)
    c: Coincident(g1,g0)
    c: Horizontal(g1)
    c: Coincident(g2,g1)
    c: PointOnObject(g3,g-3)
    c: Parallel(g3,g-6)
    c: Parallel(g2,g-6)
    c: Radius(g4) = 3.5
    c: Coincident(g4,g-7)
    c: Tangent(g3,g4) = 1.5708
    c: Horizontal(g5)
    c: Tangent(g5,g4) = 1.5708
    c: DistanceX(g-8,g5) = 3.8
    c: Coincident(g2,g5)
    c: Coincident(g6,g0)
    c: PointOnObject(g6,g-3)
    c: DistanceX(g6,g6) = 19
    c: PointOnObject(g7,g-3)
    c: DistanceX(g7,g6) = 12
    c: Coincident(g7,g3)
    c: PointOnObject(g8,g-3)
    c: PointOnObject(g8,g-3)
    c: DistanceX(g8,g8) = 10
    c: DistanceX(g8,g6) = 1
    c: Horizontal(g9)
    c: Vertical(g7,g9)
    c: Vertical(g6,g9)
    c: DistanceY(g9,g7) = 8
    c: Horizontal(g10)
    c: Equal(g8,g10)
    c: DistanceY(g10,g8) = 3
    c: Radius(g11) = 20
    c: Coincident(g11,g6)
    c: Coincident(g11,g9)
    c: Radius(g12) = 20
    c: Coincident(g12,g7)
    c: Coincident(g12,g9)
    c: Equal(g13,g11)
    c: Coincident(g13,g8)
    c: Coincident(g13,g10)
    c: Horizontal(g13,g11)
    c: Equal(g14,g12)
    c: Coincident(g14,g8)
    c: Coincident(g14,g10)
    c: Horizontal(g1,g-6)
FEATURE [Sketcher::SketchObject] Sketch122
  ArcFitTolerance = 1e-06
  AttachmentSupport = -> [Pad011]
  ExternalGeometry = -> [Binder001]
  FullyConstrained = true
  MakeInternals = false
  MapMode = 5
  Placement = pos=(0,-2,0) rot=(1,0,0;1.5708rad)
  sketch-geometry (8):
    g0: LineSegment StartX=-202.765 StartY=20.303 StartZ=0 EndX=-143.955 EndY=20.303 EndZ=0
    g1: ArcOfCircle CenterX=-184.801 CenterY=-67.3089 CenterZ=0 NormalX=0 NormalY=0 NormalZ=1 AngleXU=0 Radius=33.7833 StartAngle=2.70526 EndAngle=3.54053
    g2: LineSegment StartX=-176.685 StartY=-80.4316 StartZ=0 EndX=-215.932 EndY=-80.4316 EndZ=0
    g3: LineSegment StartX=-215.42 StartY=-53.0315 StartZ=0 EndX=-192.176 EndY=-3.18454 EndZ=0
    g4: ArcOfCircle CenterX=-207.583 CenterY=4 CenterZ=0 NormalX=0 NormalY=0 NormalZ=1 AngleXU=0 Radius=17 StartAngle=5.84685 EndAngle=7.56663
    g5: Circle CenterX=-213.443 CenterY=-76.8316 CenterZ=0 NormalX=0 NormalY=0 NormalZ=1 AngleXU=0 Radius=3
    g6: Circle CenterX=-179.305 CenterY=-76.8316 CenterZ=0 NormalX=0 NormalY=0 NormalZ=1 AngleXU=0 Radius=3
    g7: LineSegment StartX=-143.955 StartY=20.303 StartZ=0 EndX=-176.685 EndY=-80.4316 EndZ=0
  constraints (18):
    c: Coincident(g0,g-6)
    c: Coincident(g1,g-7)
    c: Coincident(g1,g-8)
    c: Coincident(g2,g1)
    c: Tangent(g3,g-5)
    c: Coincident(g4,g-6)
    c: Coincident(g4,g0)
    c: Coincident(g3,g4)
    c: Coincident(g1,g3)
    c: Diameter(g5) = 6
    c: Diameter(g6) = 6
    c: Coincident(g5,g-9)
    c: Coincident(g6,g-10)
    c: Horizontal(g0)
    c: Horizontal(g2)
    c: Coincident(g7,g0)
    c: Coincident(g7,g2)
    c: Tangent(g7,g-4)
FEATURE [Sketcher::SketchObject] Sketch123
  ArcFitTolerance = 1e-06
  AttachmentSupport = -> [Pad011]
  ExternalGeometry = -> [Binder001]
  FullyConstrained = true
  MakeInternals = false
  MapMode = 5
  Placement = pos=(0,-2,0) rot=(1,0,0;1.5708rad)
  sketch-geometry (4):
    g0: LineSegment StartX=-108 StartY=36.8 StartZ=0 EndX=-90 EndY=36.8 EndZ=0
    g1: LineSegment StartX=-108 StartY=36.8 StartZ=0 EndX=-108 EndY=26.8 EndZ=0
    g2: LineSegment StartX=-108 StartY=26.8 StartZ=0 EndX=-90 EndY=26.8 EndZ=0
    g3: ArcOfCircle CenterX=-94 CenterY=31.8 CenterZ=0 NormalX=0 NormalY=0 NormalZ=1 AngleXU=0 Radius=6.40312 StartAngle=5.38713 EndAngle=7.17924
  constraints (13):
    c: Horizontal(g0)
    c: Coincident(g1,g0)
    c: Vertical(g1)
    c: Coincident(g2,g1)
    c: Horizontal(g2)
    c: DistanceX(g0,g0) = 18
    c: DistanceY(g1,g1) = 10
    c: Equal(g0,g2)
    c: DistanceX(g0,g-3) = 90
    c: DistanceY(g0,g-3) = 2.4
    c: Coincident(g3,g0)
    c: Coincident(g3,g2)
    c: DistanceX(g3,g0) = 4
FEATURE [PartDesign::Chamfer] Chamfer014
  Angle = 45
  Base = -> Pad011 [Edge80,Edge4,Edge7]
  BaseFeature = -> Pad011
  ChamferType = 0
  FlipDirection = false
  Refine = true
  Size = 1.9
  Size2 = 1
  SupportTransform = false
  Suppressed = false
  UseAllEdges = false
FEATURE [PartDesign::Pocket] Pocket006
  BaseFeature = -> Chamfer014
  Direction = (0,-1,2e-16)
  Length = 1.2
  Length2 = 5
  Profile = -> Sketch115
  ReferenceAxis = -> Sketch115 [N_Axis]
  Refine = true
  Suppressed = false
  Type = 0
FEATURE [Sketcher::SketchObject] Sketch116
  ArcFitTolerance = 1e-06
  AttachmentSupport = -> [Pocket006]
  ExternalGeometry = -> [Binder001]
  FullyConstrained = true
  MakeInternals = false
  MapMode = 5
  Placement = pos=(0,1.7e-15,0) rot=(0,0.707107,0.707107;3.14159rad)
  sketch-geometry (4):
    g0: Circle CenterX=43.2 CenterY=30.3 CenterZ=0 NormalX=0 NormalY=0 NormalZ=1 AngleXU=0 Radius=3.4
    g1: Circle CenterX=43.2 CenterY=12.1 CenterZ=0 NormalX=0 NormalY=0 NormalZ=1 AngleXU=0 Radius=3.4
    g2: Circle CenterX=18.6 CenterY=30.3 CenterZ=0 NormalX=0 NormalY=0 NormalZ=1 AngleXU=0 Radius=3.4
    g3: Circle CenterX=18.6 CenterY=12.1 CenterZ=0 NormalX=0 NormalY=0 NormalZ=1 AngleXU=0 Radius=3.4
  constraints (8):
    c: Diameter(g0) = 6.8
    c: Diameter(g1) = 6.8
    c: Diameter(g2) = 6.8
    c: Diameter(g3) = 6.8
    c: Coincident(g2,g-3)
    c: Coincident(g0,g-4)
    c: Coincident(g3,g-6)
    c: Coincident(g1,g-5)
FEATURE [PartDesign::Pad] Pad012
  BaseFeature = -> Pocket006
  Direction = (0,1,-2e-16)
  Length = 2.4
  Length2 = 10
  Profile = -> Sketch116
  ReferenceAxis = -> Sketch116 [N_Axis]
  Refine = true
  Suppressed = false
  Type = 0
FEATURE [PartDesign::Pocket] Pocket007
  BaseFeature = -> Pad012
  Direction = (0,-1,2e-16)
  Length = 0.6
  Length2 = 2.4
  Profile = -> Sketch117
  ReferenceAxis = -> Sketch117 [N_Axis]
  Refine = true
  Suppressed = false
  Type = 4
FEATURE [PartDesign::Pad] Pad013
  BaseFeature = -> Pocket007
  Direction = (0,-1,2e-16)
  Length = 1.6
  Length2 = 10
  Profile = -> Sketch118
  ReferenceAxis = -> Sketch118 [N_Axis]
  Refine = true
  Suppressed = false
  Type = 0
FEATURE [Sketcher::SketchObject] Sketch119
  ArcFitTolerance = 1e-06
  AttachmentSupport = -> [Pad013]
  ExternalGeometry = -> [Binder001]
  FullyConstrained = true
  MakeInternals = false
  MapMode = 5
  Placement = pos=(0,-3.6,0) rot=(1,0,0;1.5708rad)
  sketch-geometry (21):
    g0: LineSegment [constr] StartX=-82.8 StartY=3.2 StartZ=0 EndX=-82.8 EndY=39.2 EndZ=0
    g1: ArcOfCircle CenterX=-78.51 CenterY=34.8 CenterZ=0 NormalX=0 NormalY=0 NormalZ=1 AngleXU=0 Radius=3.5 StartAngle=4.71239 EndAngle=6.28319
    g2: ArcOfCircle CenterX=-78.51 CenterY=7.6 CenterZ=0 NormalX=0 NormalY=0 NormalZ=1 AngleXU=0 Radius=3.5 StartAngle=0 EndAngle=1.5708
    g3: ArcOfCircle CenterX=-5.6 CenterY=34.8 CenterZ=0 NormalX=0 NormalY=0 NormalZ=1 AngleXU=0 Radius=3.5 StartAngle=3.14159 EndAngle=4.71239
    g4: ArcOfCircle CenterX=-5.6 CenterY=7.6 CenterZ=0 NormalX=0 NormalY=0 NormalZ=1 AngleXU=0 Radius=3.5 StartAngle=1.5708 EndAngle=3.14159
    g5: LineSegment StartX=0 StartY=39.2 StartZ=0 EndX=0 EndY=31.3 EndZ=0
    g6: LineSegment StartX=0 StartY=39.2 StartZ=0 EndX=-9.1 EndY=39.2 EndZ=0
    g7: LineSegment StartX=0 StartY=3.2 StartZ=0 EndX=0 EndY=11.1 EndZ=0
    g8: LineSegment StartX=0 StartY=3.2 StartZ=0 EndX=-9.1 EndY=3.2 EndZ=0
    g9: LineSegment StartX=-82.8 StartY=3.2 StartZ=0 EndX=-75.01 EndY=3.2 EndZ=0
    g10: LineSegment StartX=-82.8 StartY=3.2 StartZ=0 EndX=-82.8 EndY=11.1 EndZ=0
    g11: LineSegment StartX=-82.8 StartY=39.2 StartZ=0 EndX=-82.8 EndY=31.3 EndZ=0
    g12: LineSegment StartX=-82.8 StartY=39.2 StartZ=0 EndX=-75.01 EndY=39.2 EndZ=0
    g13: LineSegment StartX=-82.8 StartY=31.3 StartZ=0 EndX=-78.51 EndY=31.3 EndZ=0
    g14: LineSegment StartX=-75.01 StartY=39.2 StartZ=0 EndX=-75.01 EndY=34.8 EndZ=0
    g15: LineSegment StartX=-82.8 StartY=11.1 StartZ=0 EndX=-78.51 EndY=11.1 EndZ=0
    g16: LineSegment StartX=-75.01 StartY=3.2 StartZ=0 EndX=-75.01 EndY=7.6 EndZ=0
    g17: LineSegment StartX=-9.1 StartY=39.2 StartZ=0 EndX=-9.1 EndY=34.8 EndZ=0
    g18: LineSegment StartX=0 StartY=31.3 StartZ=0 EndX=-5.6 EndY=31.3 EndZ=0
    g19: LineSegment StartX=0 StartY=11.1 StartZ=0 EndX=-5.6 EndY=11.1 EndZ=0
    g20: LineSegment StartX=-9.1 StartY=3.2 StartZ=0 EndX=-9.1 EndY=7.6 EndZ=0
  constraints (51):
    c: Coincident(g0,g-10)
    c: PointOnObject(g0,g-8)
    c: Vertical(g0)
    c: Coincident(g1,g-3)
    c: Coincident(g2,g-4)
    c: Coincident(g3,g-5)
    c: Coincident(g4,g-6)
    c: Radius(g4) = 3.5
    c: Radius(g3) = 3.5
    c: Radius(g1) = 3.5
    c: Radius(g2) = 3.5
    c: Coincident(g5,g-9)
    c: PointOnObject(g5,g-9)
    c: Coincident(g6,g5)
    c: PointOnObject(g6,g-8)
    c: Coincident(g7,g-9)
    c: PointOnObject(g7,g-9)
    c: Coincident(g8,g7)
    c: PointOnObject(g8,g-7)
    c: Coincident(g9,g0)
    c: PointOnObject(g9,g-7)
    c: Coincident(g10,g0)
    c: PointOnObject(g10,g0)
    c: Coincident(g11,g0)
    c: PointOnObject(g11,g0)
    c: Coincident(g12,g0)
    c: PointOnObject(g12,g-8)
    c: Coincident(g13,g11)
    c: Horizontal(g13)
    c: Coincident(g14,g12)
    c: Vertical(g14)
    c: Coincident(g15,g10)
    c: Horizontal(g15)
    c: Coincident(g16,g9)
    c: Vertical(g16)
    c: Coincident(g17,g6)
    c: Vertical(g17)
    c: Coincident(g18,g5)
    c: Horizontal(g18)
    c: Coincident(g19,g7)
    c: Horizontal(g19)
    c: Coincident(g20,g8)
    c: Vertical(g20)
    c: Tangent(g20,g4) = 1.5708
    c: Tangent(g4,g19) = -1.5708
    c: Tangent(g18,g3) = 1.5708
    c: Tangent(g3,g17) = -1.5708
    c: Tangent(g13,g1) = -1.5708
    c: Tangent(g1,g14) = 1.5708
    c: Tangent(g16,g2) = -1.5708
    c: Tangent(g2,g15) = 1.5708
FEATURE [PartDesign::Pocket] Pocket008
  BaseFeature = -> Pad013
  Direction = (0,1,-2e-16)
  Length = 1.6
  Length2 = 5
  Profile = -> Sketch119
  ReferenceAxis = -> Sketch119 [N_Axis]
  Refine = true
  Suppressed = false
  Type = 0
FEATURE [PartDesign::Pad] Pad017
  BaseFeature = -> Pocket008
  Direction = (0,-1,2e-16)
  Length = 1.6
  Length2 = 10
  Profile = -> Sketch123
  ReferenceAxis = -> Sketch123 [N_Axis]
  Refine = true
  Suppressed = false
  Type = 0
FEATURE [Sketcher::SketchObject] Sketch125
  ArcFitTolerance = 1e-06
  AttachmentSupport = -> [Pad017]
  ExternalGeometry = -> [Pad017]
  FullyConstrained = true
  MakeInternals = false
  MapMode = 5
  Placement = pos=(0,-3.6,8e-16) rot=(1,0,0;1.5708rad)
  sketch-geometry (20):
    g0: LineSegment StartX=-108 StartY=35.8 StartZ=0 EndX=-108 EndY=35 EndZ=0
    g1: LineSegment StartX=-108 StartY=35 StartZ=0 EndX=-97 EndY=35 EndZ=0
    g2: LineSegment StartX=-97 StartY=35 StartZ=0 EndX=-97 EndY=35.8 EndZ=0
    g3: LineSegment StartX=-97 StartY=35.8 StartZ=0 EndX=-108 EndY=35.8 EndZ=0
    g4: LineSegment StartX=-108 StartY=28.6 StartZ=0 EndX=-108 EndY=27.8 EndZ=0
    g5: LineSegment StartX=-108 StartY=27.8 StartZ=0 EndX=-97 EndY=27.8 EndZ=0
    g6: LineSegment StartX=-97 StartY=27.8 StartZ=0 EndX=-97 EndY=28.6 EndZ=0
    g7: LineSegment StartX=-97 StartY=28.6 StartZ=0 EndX=-108 EndY=28.6 EndZ=0
    g8: LineSegment StartX=-108 StartY=30.4 StartZ=0 EndX=-108 EndY=29.6 EndZ=0
    g9: LineSegment StartX=-108 StartY=29.6 StartZ=0 EndX=-97 EndY=29.6 EndZ=0
    g10: LineSegment StartX=-97 StartY=29.6 StartZ=0 EndX=-97 EndY=30.4 EndZ=0
    g11: LineSegment StartX=-97 StartY=30.4 StartZ=0 EndX=-108 EndY=30.4 EndZ=0
    g12: LineSegment StartX=-108 StartY=32.2 StartZ=0 EndX=-108 EndY=31.4 EndZ=0
    g13: LineSegment StartX=-108 StartY=31.4 StartZ=0 EndX=-97 EndY=31.4 EndZ=0
    g14: LineSegment StartX=-97 StartY=31.4 StartZ=0 EndX=-97 EndY=32.2 EndZ=0
    g15: LineSegment StartX=-97 StartY=32.2 StartZ=0 EndX=-108 EndY=32.2 EndZ=0
    g16: LineSegment StartX=-108 StartY=34 StartZ=0 EndX=-108 EndY=33.2 EndZ=0
    g17: LineSegment StartX=-108 StartY=33.2 StartZ=0 EndX=-97 EndY=33.2 EndZ=0
    g18: LineSegment StartX=-97 StartY=33.2 StartZ=0 EndX=-97 EndY=34 EndZ=0
    g19: LineSegment StartX=-97 StartY=34 StartZ=0 EndX=-108 EndY=34 EndZ=0
  constraints (55):
    c: Coincident(g1,g0)
    c: Horizontal(g1)
    c: Coincident(g2,g1)
    c: Vertical(g2)
    c: Coincident(g3,g2)
    c: Horizontal(g3)
    c: Coincident(g3,g0)
    c: DistanceX(g1,g1) = 11
    c: DistanceY(g2,g2) = 0.8
    c: Coincident(g5,g4)
    c: Horizontal(g5)
    c: Coincident(g6,g5)
    c: Vertical(g6)
    c: Coincident(g7,g6)
    c: Horizontal(g7)
    c: Coincident(g7,g4)
    c: Coincident(g9,g8)
    c: Horizontal(g9)
    c: Coincident(g10,g9)
    c: Vertical(g10)
    c: Coincident(g11,g10)
    c: Horizontal(g11)
    c: Coincident(g11,g8)
    c: Coincident(g13,g12)
    c: Horizontal(g13)
    c: Coincident(g14,g13)
    c: Vertical(g14)
    c: Coincident(g15,g14)
    c: Horizontal(g15)
    c: Coincident(g15,g12)
    c: Coincident(g17,g16)
    c: Horizontal(g17)
    c: Coincident(g18,g17)
    c: Vertical(g18)
    c: Coincident(g19,g18)
    c: Horizontal(g19)
    c: Coincident(g19,g16)
    c: Equal(g3,g19)
    c: Equal(g3,g15)
    c: Equal(g3,g11)
    c: Equal(g3,g7)
    c: Equal(g2,g18)
    c: Equal(g2,g14)
    c: Equal(g2,g10)
    c: Equal(g2,g6)
    c: DistanceY(g-4,g4) = 1
    c: DistanceY(g4,g8) = 1
    c: DistanceY(g8,g12) = 1
    c: DistanceY(g12,g16) = 1
    c: DistanceY(g16,g0) = 1
    c: Tangent(g0,g-5)
    c: Tangent(g16,g-5)
    c: Tangent(g12,g-5)
    c: Tangent(g8,g-5)
    c: Tangent(g4,g-5)
FEATURE [PartDesign::Chamfer] Chamfer009
  Angle = 45
  Base = -> Pad017 [Edge151,Edge154]
  BaseFeature = -> Pad017
  ChamferType = 1
  FlipDirection = false
  Refine = true
  Size = 1.5
  Size2 = 2.8
  SupportTransform = false
  Suppressed = false
  UseAllEdges = false
FEATURE [PartDesign::Pocket] Pocket009
  BaseFeature = -> Chamfer009
  Direction = (0,1,-2e-16)
  Length = 1
  Length2 = 5
  Profile = -> Sketch125
  ReferenceAxis = -> Sketch125 [N_Axis]
  Refine = true
  Suppressed = false
  Type = 0
FEATURE [PartDesign::Pad] Pad014
  BaseFeature = -> Pocket009
  Direction = (0,-1,2e-16)
  Length = 0.8
  Length2 = 10
  Profile = -> Sketch120
  ReferenceAxis = -> Sketch120 [N_Axis]
  Refine = true
  Suppressed = false
  Type = 0
FEATURE [Sketcher::SketchObject] Sketch124
  ArcFitTolerance = 1e-06
  AttachmentSupport = -> [Pad014]
  ExternalGeometry = -> [Binder001]
  FullyConstrained = true
  MakeInternals = false
  MapMode = 5
  Placement = pos=(0,-2.8,6e-16) rot=(1,0,0;1.5708rad)
  sketch-geometry (4):
    g0: LineSegment StartX=-129 StartY=39.2 StartZ=0 EndX=-131.599 EndY=31.2 EndZ=0
    g1: LineSegment StartX=-118 StartY=39.2 StartZ=0 EndX=-120.599 EndY=31.2 EndZ=0
    g2: LineSegment StartX=-129 StartY=39.2 StartZ=0 EndX=-118 EndY=39.2 EndZ=0
    g3: LineSegment StartX=-120.599 StartY=31.2 StartZ=0 EndX=-131.599 EndY=31.2 EndZ=0
  constraints (12):
    c: PointOnObject(g0,g-3)
    c: PointOnObject(g1,g-3)
    c: Parallel(g-4,g0)
    c: Parallel(g-4,g1)
    c: Coincident(g2,g0)
    c: Coincident(g2,g1)
    c: DistanceX(g2,g2) = 11
    c: DistanceY(g1,g1) = 8
    c: Coincident(g3,g1)
    c: Horizontal(g3)
    c: Coincident(g3,g0)
    c: DistanceX(g1,g-3) = 118
FEATURE [PartDesign::Pad] Pad018
  BaseFeature = -> Pad014
  Direction = (0,-1,2e-16)
  Length = 1.2
  Length2 = 10
  Profile = -> Sketch124
  ReferenceAxis = -> Sketch124 [N_Axis]
  Refine = true
  Suppressed = false
  Type = 0
FEATURE [Sketcher::SketchObject] Sketch126
  ArcFitTolerance = 1e-06
  AttachmentSupport = -> [Pad018]
  ExternalGeometry = -> [Pad018]
  FullyConstrained = true
  MakeInternals = false
  MapMode = 5
  Placement = pos=(0,-4,0) rot=(1,0,0;1.5708rad)
  sketch-geometry (8):
    g0: LineSegment StartX=-129.877 StartY=36.5 StartZ=0 EndX=-130.137 EndY=35.7 EndZ=0
    g1: LineSegment StartX=-130.69 StartY=34 StartZ=0 EndX=-130.95 EndY=33.2 EndZ=0
    g2: LineSegment StartX=-129.877 StartY=36.5 StartZ=0 EndX=-118.877 EndY=36.5 EndZ=0
    g3: LineSegment StartX=-130.137 StartY=35.7 StartZ=0 EndX=-119.137 EndY=35.7 EndZ=0
    g4: LineSegment StartX=-130.69 StartY=34 StartZ=0 EndX=-119.69 EndY=34 EndZ=0
    g5: LineSegment StartX=-130.95 StartY=33.2 StartZ=0 EndX=-119.95 EndY=33.2 EndZ=0
    g6: LineSegment StartX=-118.877 StartY=36.5 StartZ=0 EndX=-119.137 EndY=35.7 EndZ=0
    g7: LineSegment StartX=-119.69 StartY=34 StartZ=0 EndX=-119.95 EndY=33.2 EndZ=0
  constraints (20):
    c: Coincident(g2,g0)
    c: Horizontal(g2)
    c: Coincident(g3,g0)
    c: Horizontal(g3)
    c: Coincident(g4,g1)
    c: Horizontal(g4)
    c: Coincident(g5,g1)
    c: Horizontal(g5)
    c: Coincident(g6,g2)
    c: Coincident(g6,g3)
    c: Coincident(g7,g4)
    c: Coincident(g7,g5)
    c: Tangent(g0,g-4)
    c: Tangent(g6,g-5)
    c: Tangent(g1,g-4)
    c: Tangent(g7,g-5)
    c: DistanceY(g3,g2) = 0.8
    c: DistanceY(g5,g4) = 0.8
    c: DistanceY(g-6,g1) = 2
    c: DistanceY(g-6,g0) = 4.5
FEATURE [PartDesign::Chamfer] Chamfer008
  Angle = 45
  Base = -> Pad018 [Edge257]
  BaseFeature = -> Pad018
  ChamferType = 1
  FlipDirection = false
  Refine = true
  Size = 1
  Size2 = 6
  SupportTransform = false
  Suppressed = false
  UseAllEdges = false
FEATURE [PartDesign::Pocket] Pocket010
  BaseFeature = -> Chamfer008
  Direction = (0,1,-2e-16)
  Length = 1
  Length2 = 5
  Profile = -> Sketch126
  ReferenceAxis = -> Sketch126 [N_Axis]
  Refine = true
  Suppressed = false
  Type = 0
FEATURE [PartDesign::Pad] Pad015
  BaseFeature = -> Pocket010
  Direction = (0,-1,2e-16)
  Length = 2
  Length2 = 10
  Profile = -> Sketch121
  ReferenceAxis = -> Sketch121 [N_Axis]
  Refine = true
  Suppressed = false
  Type = 0
FEATURE [PartDesign::Pad] Pad016
  BaseFeature = -> Pad015
  Direction = (0,-1,2e-16)
  Length = 1.6
  Length2 = 10
  Profile = -> Sketch122
  ReferenceAxis = -> Sketch122 [N_Axis]
  Refine = true
  Suppressed = false
  Type = 0
FEATURE [Sketcher::SketchObject] Sketch127
  ArcFitTolerance = 1e-06
  AttachmentSupport = -> [Pad016]
  ExternalGeometry = -> [Pad016]
  FullyConstrained = true
  MakeInternals = false
  MapMode = 5
  Placement = pos=(0,0,-80.4316) rot=(1,0,0;3.14159rad)
  sketch-geometry (8):
    g0: LineSegment StartX=-176.685 StartY=3.6 StartZ=0 EndX=-186.685 EndY=3.6 EndZ=0
    g1: LineSegment [constr] StartX=-186.685 StartY=3.6 StartZ=0 EndX=-186.685 EndY=-9e-16 EndZ=0
    g2: LineSegment StartX=-176.685 StartY=3.6 StartZ=0 EndX=-176.685 EndY=0 EndZ=0
    g3: ArcOfEllipse CenterX=-186.685 CenterY=-9e-16 CenterZ=0 NormalX=0 NormalY=0 NormalZ=1 MajorRadius=10 MinorRadius=3.6 AngleXU=1e-16 StartAngle=0 EndAngle=1.5708
    g4: LineSegment [constr] StartX=-176.685 StartY=-2e-15 StartZ=0 EndX=-196.685 EndY=-2e-15 EndZ=0
    g5: LineSegment [constr] StartX=-186.685 StartY=3.6 StartZ=0 EndX=-186.685 EndY=-3.6 EndZ=0
    g6: GeomPoint [constr] X=-177.356 Y=0 Z=0
    g7: GeomPoint [constr] X=-196.015 Y=-1.9e-15 Z=0
  constraints (13):
    c: Coincident(g0,g-4)
    c: PointOnObject(g0,g-4)
    c: DistanceX(g0,g0) = 10
    c: Coincident(g1,g0)
    c: PointOnObject(g1,g-5)
    c: Vertical(g1)
    c: Coincident(g2,g0)
    c: Coincident(g2,g-5)
    c: InternalAlignment(g4-g7 -> g3) x4
    c: Coincident(g3,g1)
    c: Coincident(g3,g0)
    c: Coincident(g3,g2)
    c: Horizontal(g4)
FEATURE [Sketcher::SketchObject] Sketch128
  ArcFitTolerance = 1e-06
  AttachmentSupport = -> [Pad016]
  ExternalGeometry = -> [Pad016]
  FullyConstrained = true
  MakeInternals = false
  MapMode = 5
  Placement = pos=(0,0,-80.4316) rot=(1,0,0;3.14159rad)
  sketch-geometry (8):
    g0: LineSegment StartX=-215.932 StartY=3.6 StartZ=0 EndX=-215.932 EndY=-1.3e-15 EndZ=0
    g1: LineSegment StartX=-215.932 StartY=3.6 StartZ=0 EndX=-205.932 EndY=3.6 EndZ=0
    g2: LineSegment [constr] StartX=-205.932 StartY=3.6 StartZ=0 EndX=-205.932 EndY=-9e-16 EndZ=0
    g3: ArcOfEllipse CenterX=-205.932 CenterY=-9e-16 CenterZ=0 NormalX=0 NormalY=0 NormalZ=1 MajorRadius=10 MinorRadius=3.6 AngleXU=-3.14159 StartAngle=4.71239 EndAngle=6.28319
    g4: LineSegment [constr] StartX=-215.932 StartY=-1e-15 StartZ=0 EndX=-195.932 EndY=-1e-15 EndZ=0
    g5: LineSegment [constr] StartX=-205.932 StartY=-3.6 StartZ=0 EndX=-205.932 EndY=3.6 EndZ=0
    g6: GeomPoint [constr] X=-215.262 Y=-2e-15 Z=0
    g7: GeomPoint [constr] X=-196.602 Y=-1e-15 Z=0
  constraints (13):
    c: Coincident(g0,g-4)
    c: Coincident(g0,g-5)
    c: Coincident(g1,g0)
    c: PointOnObject(g1,g-3)
    c: DistanceX(g1,g1) = 10
    c: Coincident(g2,g1)
    c: Vertical(g2)
    c: PointOnObject(g2,g-5)
    c: InternalAlignment(g4-g7 -> g3) x4
    c: Coincident(g3,g2)
    c: Coincident(g3,g1)
    c: Coincident(g3,g0)
    c: Horizontal(g4)
FEATURE [PartDesign::SubtractivePipe] SubtractivePipe002
  AuxilleryCurvelinear = true
  AuxillerySpineTangent = false
  BaseFeature = -> Pad016
  Binormal = (0,0,0)
  Mode = 0
  Profile = -> Sketch127
  Refine = true
  Spine = -> Pad016 [Edge254]
  SpineTangent = false
  Suppressed = false
  Transformation = 0
  Transition = 0
FEATURE [PartDesign::SubtractivePipe] SubtractivePipe003
  AuxilleryCurvelinear = true
  AuxillerySpineTangent = false
  BaseFeature = -> SubtractivePipe002
  Binormal = (0,0,0)
  Mode = 0
  Profile = -> Sketch128
  Refine = true
  Spine = -> Pad016 [Edge256,Edge251,Edge252]
  SpineTangent = false
  Suppressed = false
  Transformation = 0
  Transition = 0
FEATURE [Sketcher::SketchObject] Sketch129
  ArcFitTolerance = 1e-06
  AttachmentSupport = -> [Pad016]
  ExternalGeometry = -> [Binder001]
  FullyConstrained = true
  MakeInternals = false
  MapMode = 5
  Placement = pos=(0,-3.6,0) rot=(1,0,0;1.5708rad)
  sketch-geometry (12):
    g0: LineSegment [constr] StartX=-192.176 StartY=-3.18451 StartZ=0 EndX=-181.223 EndY=20.303 EndZ=0
    g1: LineSegment [constr] StartX=-202.765 StartY=20.303 StartZ=0 EndX=-181.223 EndY=20.303 EndZ=0
    g2: LineSegment StartX=-202.765 StartY=20.303 StartZ=0 EndX=-181.223 EndY=20.303 EndZ=0
    g3: LineSegment StartX=-192.176 StartY=-3.18451 StartZ=0 EndX=-196.804 EndY=-13.1107 EndZ=0
    g4: ArcOfCircle CenterX=-207.583 CenterY=4 CenterZ=0 NormalX=0 NormalY=0 NormalZ=1 AngleXU=0 Radius=17 StartAngle=5.84685 EndAngle=7.56663
    g5: ArcOfEllipse CenterX=-181.223 CenterY=8.55923 CenterZ=0 NormalX=0 NormalY=0 NormalZ=1 MajorRadius=23.4779 MinorRadius=11.7437 AngleXU=2e-16 StartAngle=4.71239 EndAngle=7.85398
    g6: LineSegment [constr] StartX=-157.745 StartY=8.55923 StartZ=0 EndX=-204.701 EndY=8.55923 EndZ=0
    g7: LineSegment [constr] StartX=-181.223 StartY=20.303 StartZ=0 EndX=-181.223 EndY=-3.18451 EndZ=0
    g8: GeomPoint [constr] X=-160.894 Y=8.55923 Z=0
    g9: GeomPoint [constr] X=-201.553 Y=8.55923 Z=0
    g10: ArcOfCircle CenterX=-181.223 CenterY=-20.3763 CenterZ=0 NormalX=0 NormalY=0 NormalZ=1 AngleXU=0 Radius=17.1918 StartAngle=1.57079 EndAngle=2.70526
    g11: GeomPoint [constr] X=-181.223 Y=-3.18451 Z=0
  constraints (23):
    c: Coincident(g0,g-5)
    c: Coincident(g1,g-6)
    c: Horizontal(g1)
    c: Coincident(g1,g0)
    c: Parallel(g0,g-4)
    c: Coincident(g2,g1)
    c: Coincident(g2,g0)
    c: Coincident(g3,g0)
    c: Equal(g4,g-5)
    c: Coincident(g4,g1)
    c: Coincident(g4,g0)
    c: InternalAlignment(g6-g9 -> g5) x4
    c: Vertical(g5,g0)
    c: Horizontal(g6)
    c: Coincident(g5,g0)
    c: DistanceX(g6,g-3) = 10.1
    c: Tangent(g10,g3) = -1.5708
    c: PointOnObject(g11,g10)
    c: Tangent(g5,g10,g11) = 1.5708
    c: Coincident(g10,g5)
    c: Coincident(g11,g7)
    c: Parallel(g3,g-4)
    c: Horizontal(g5,g0)
FEATURE [Sketcher::SketchObject] Sketch130
  ArcFitTolerance = 1e-06
  AttachmentOffset = pos=(0,0,-1.6) rot=(0,0,1;0rad)
  AttachmentSupport = -> [Pad016]
  ExternalGeometry = -> [Binder001]
  FullyConstrained = true
  MakeInternals = false
  MapMode = 5
  Placement = pos=(0,-2,-4e-16) rot=(1,0,0;1.5708rad)
  sketch-geometry (12):
    g0: LineSegment [constr] StartX=-192.176 StartY=-3.18451 StartZ=0 EndX=-181.223 EndY=20.303 EndZ=0
    g1: LineSegment [constr] StartX=-202.765 StartY=20.303 StartZ=0 EndX=-181.223 EndY=20.303 EndZ=0
    g2: LineSegment StartX=-202.765 StartY=20.303 StartZ=0 EndX=-181.223 EndY=20.303 EndZ=0
    g3: LineSegment StartX=-192.176 StartY=-3.18451 StartZ=0 EndX=-193.827 EndY=-6.72678 EndZ=0
    g4: ArcOfCircle CenterX=-207.583 CenterY=4 CenterZ=0 NormalX=0 NormalY=0 NormalZ=1 AngleXU=0 Radius=17 StartAngle=5.84685 EndAngle=7.56663
    g5: ArcOfEllipse CenterX=-181.223 CenterY=10.803 CenterZ=0 NormalX=0 NormalY=0 NormalZ=1 MajorRadius=14.4779 MinorRadius=9.5 AngleXU=0 StartAngle=4.71239 EndAngle=7.85398
    g6: LineSegment [constr] StartX=-166.745 StartY=10.803 StartZ=0 EndX=-195.701 EndY=10.803 EndZ=0
    g7: LineSegment [constr] StartX=-181.223 StartY=20.303 StartZ=0 EndX=-181.223 EndY=1.30297 EndZ=0
    g8: GeomPoint [constr] X=-170.298 Y=10.803 Z=0
    g9: GeomPoint [constr] X=-192.148 Y=10.803 Z=0
    g10: ArcOfCircle CenterX=-181.223 CenterY=-12.6042 CenterZ=0 NormalX=0 NormalY=0 NormalZ=1 AngleXU=0 Radius=13.9072 StartAngle=1.5708 EndAngle=2.70526
    g11: GeomPoint [constr] X=-181.223 Y=1.30297 Z=0
  constraints (23):
    c: Coincident(g0,g-5)
    c: Coincident(g1,g-6)
    c: Horizontal(g1)
    c: Coincident(g1,g0)
    c: Parallel(g0,g-4)
    c: Coincident(g2,g1)
    c: Coincident(g2,g0)
    c: Coincident(g3,g0)
    c: Equal(g4,g-5)
    c: Coincident(g4,g1)
    c: Coincident(g4,g0)
    c: InternalAlignment(g6-g9 -> g5) x4
    c: Vertical(g5,g0)
    c: Horizontal(g6)
    c: Coincident(g5,g0)
    c: DistanceX(g6,g-3) = 19.1
    c: Tangent(g10,g3) = -1.5708
    c: PointOnObject(g11,g10)
    c: Tangent(g5,g10,g11) = 1.5708
    c: Coincident(g10,g5)
    c: Coincident(g11,g7)
    c: Parallel(g3,g-4)
    c: DistanceY(g5,g0) = 19
FEATURE [Part::Part2DObjectPython] Clone2D001  label="Sketch130 (2D)"  # Draft 2D object (typed FeaturePython)
  Fuse = false
  Objects = -> [Sketch130]
  Placement = pos=(0,-2,-4e-16) rot=(1,0,0;1.5708rad)
  Scale = (1,1,1)
FEATURE [Sketcher::SketchObject] Sketch131
  ArcFitTolerance = 1e-06
  AttachmentOffset = pos=(0,0,-3.5) rot=(0,0,1;0rad)
  AttachmentSupport = -> [Pad016]
  ExternalGeometry = -> [Binder001]
  FullyConstrained = true
  MakeInternals = false
  MapMode = 5
  Placement = pos=(0,-0.1,-8e-16) rot=(1,0,0;1.5708rad)
  sketch-geometry (1):
    g0: GeomPoint X=-197.47 Y=8.55923 Z=0
  constraints (1):
    c: Symmetric(g-6,g-4,g0)
FEATURE [PartDesign::SubtractiveLoft] SubtractiveLoft002
  BaseFeature = -> SubtractivePipe003
  Closed = false
  Profile = -> Sketch129
  Refine = true
  Ruled = false
  Sections = -> [Sketch130]
  Suppressed = false
FEATURE [PartDesign::SubtractiveLoft] SubtractiveLoft003
  BaseFeature = -> SubtractiveLoft002
  Closed = false
  Profile = -> Clone2D001
  Refine = true
  Ruled = false
  Sections = -> [Sketch131]
  Suppressed = false
FEATURE [PartDesign::Chamfer] Chamfer010
  Angle = 45
  Base = -> SubtractiveLoft003 [Edge200,Edge201,Edge203,Edge202,Edge194]
  BaseFeature = -> SubtractiveLoft003
  ChamferType = 0
  FlipDirection = false
  Refine = true
  Size = 1.5
  Size2 = 1
  SupportTransform = false
  Suppressed = false
  UseAllEdges = false
FEATURE [PartDesign::Chamfer] Chamfer011
  Angle = 45
  Base = -> Chamfer010 [Edge15]
  BaseFeature = -> Chamfer010
  ChamferType = 0
  FlipDirection = false
  Refine = true
  Size = 3.5
  Size2 = 1
  SupportTransform = false
  Suppressed = false
  UseAllEdges = false
FEATURE [PartDesign::Chamfer] Chamfer012
  Angle = 45
  Base = -> Chamfer011 [Edge10]
  BaseFeature = -> Chamfer011
  ChamferType = 0
  FlipDirection = false
  Refine = true
  Size = 3.5
  Size2 = 1
  SupportTransform = false
  Suppressed = false
  UseAllEdges = false
FEATURE [PartDesign::Chamfer] Chamfer013
  Angle = 45
  Base = -> Chamfer012 [Edge146,Edge93]
  BaseFeature = -> Chamfer012
  ChamferType = 0
  FlipDirection = false
  Refine = true
  Size = 1.9
  Size2 = 1
  SupportTransform = false
  Suppressed = false
  UseAllEdges = false
FEATURE [Sketcher::SketchObject] Sketch132
  ArcFitTolerance = 1e-06
  AttachmentSupport = -> [Pad016]
  ExternalGeometry = -> [Binder001]
  FullyConstrained = true
  MakeInternals = false
  MapMode = 5
  Placement = pos=(0,-3.6,0) rot=(1,0,0;1.5708rad)
  sketch-geometry (3):
    g0: LineSegment [constr] StartX=-215.42 StartY=-53.0314 StartZ=0 EndX=-167.782 EndY=-53.0314 EndZ=0
    g1: Circle CenterX=-191.282 CenterY=-53.0314 CenterZ=0 NormalX=0 NormalY=0 NormalZ=1 AngleXU=0 Radius=11.5
    g2: Circle CenterX=-191.282 CenterY=-53.0314 CenterZ=0 NormalX=0 NormalY=0 NormalZ=1 AngleXU=0 Radius=10.7
  constraints (8):
    c: Coincident(g0,g-3)
    c: PointOnObject(g0,g-4)
    c: Horizontal(g0)
    c: Diameter(g1) = 23
    c: PointOnObject(g1,g0)
    c: DistanceX(g1,g0) = 23.5
    c: Diameter(g2) = 21.4
    c: Coincident(g2,g1)
FEATURE [PartDesign::Fillet] Fillet007
  Base = -> Chamfer013 [Edge84]
  BaseFeature = -> Chamfer013
  Radius = 1.1
  Refine = true
  SupportTransform = false
  Suppressed = false
  UseAllEdges = false
FEATURE [PartDesign::Fillet] Fillet008
  Base = -> Fillet007 [Edge77]
  BaseFeature = -> Fillet007
  Radius = 1.9
  Refine = true
  SupportTransform = false
  Suppressed = false
  UseAllEdges = false
FEATURE [PartDesign::Pocket] Pocket011
  BaseFeature = -> Fillet008
  Direction = (0,1,-2e-16)
  Length = 0.8
  Length2 = 5
  Profile = -> Sketch132
  ReferenceAxis = -> Sketch132 [N_Axis]
  Refine = true
  Suppressed = false
  Type = 0
FEATURE [Part::Part2DObjectPython] ShapeString  # Draft 2D object (typed FeaturePython)
  FontFile = <path>
  Fuse = false
  Justification = 6
  JustificationReference = 0
  KeepLeftMargin = false
  MakeFace = true
  ObliqueAngle = 0
  Placement = pos=(-199,-3.6,-57.5) rot=(1,0,0;1.5708rad)
  ScaleToSize = true
  Size = 10
  String = AS
  Tracking = 0
FEATURE [PartDesign::Pocket] Pocket012
  BaseFeature = -> Pocket011
  Direction = (0,1,0)
  Length = 1
  Length2 = 5
  Profile = -> ShapeString
  ReferenceAxis = -> ShapeString [N_Axis]
  Refine = true
  Suppressed = false
  Type = 0
FEATURE [PartDesign::Body] Body007  label="lato DX"
  AllowCompound = false
  Group = -> [Binder001,Sketch114,Pad011,Chamfer014,Sketch115,Pocket006,Sketch116,Pad012,Sketch117,Pocket007,Sketch118,Pad013,Sketch119,Pocket008,Pad017,Chamfer009,Pocket009,Sketch123,Sketch120,Pad014,Pad018,Chamfer008,Pocket010,Sketch121,Pad015,Sketch122,Pad016,Sketch124,Sketch125,Sketch126,Sketch127,Sketch128,SubtractivePipe002,SubtractivePipe003,Sketch129,Sketch130,Clone2D001,Sketch131,SubtractiveLoft002,+11 more]
  Origin = -> Origin007
  Tip = -> Pocket012
FEATURE [Sketcher::SketchObject] Sketch133
  ArcFitTolerance = 1e-06
  AttachmentSupport = -> [Binder]
  ExternalGeometry = -> [Binder]
  FullyConstrained = true
  MakeInternals = false
  MapMode = 5
  Placement = pos=(0,9e-16,0) rot=(0,0.707107,0.707107;3.14159rad)
  sketch-geometry (30):
    g0: LineSegment StartX=0 StartY=39.2 StartZ=0 EndX=0 EndY=3.2 EndZ=0
    g1: LineSegment StartX=0 StartY=3.2 StartZ=0 EndX=82.8 EndY=3.2 EndZ=0
    g2: LineSegment StartX=82.8 StartY=3.2 StartZ=0 EndX=82.8 EndY=6.2 EndZ=0
    g3: LineSegment StartX=82.8 StartY=6.2 StartZ=0 EndX=91.752 EndY=6.2 EndZ=0
    g4: LineSegment StartX=0 StartY=39.2 StartZ=0 EndX=195.887 EndY=39.2 EndZ=0
    g5: LineSegment StartX=195.887 StartY=39.2 StartZ=0 EndX=202.765 EndY=20.303 EndZ=0
    g6: LineSegment StartX=192.333 StartY=24.9893 StartZ=0 EndX=196.467 EndY=26.4942 EndZ=0
    g7: LineSegment StartX=196.467 StartY=26.4942 StartZ=0 EndX=194.073 EndY=33.0721 EndZ=0
    g8: LineSegment StartX=194.073 StartY=33.0721 StartZ=0 EndX=189.939 EndY=31.5672 EndZ=0
    g9: LineSegment StartX=189.939 StartY=31.5672 StartZ=0 EndX=192.333 EndY=24.9893 EndZ=0
    g10: ArcOfCircle CenterX=107.6 CenterY=4 CenterZ=0 NormalX=0 NormalY=0 NormalZ=1 AngleXU=0 Radius=16 StartAngle=1.5708 EndAngle=3.00366
    g11: LineSegment StartX=107.6 StartY=20 StartZ=0 EndX=132.428 EndY=20 EndZ=0
    g12: ArcOfCircle [constr] CenterX=132.428 CenterY=4 CenterZ=0 NormalX=0 NormalY=0 NormalZ=1 AngleXU=0 Radius=16 StartAngle=0.314159 EndAngle=1.5708
    g13: LineSegment StartX=147.645 StartY=8.94427 StartZ=0 EndX=176.685 EndY=-80.4316 EndZ=0
    g14: LineSegment StartX=176.685 StartY=-80.4316 StartZ=0 EndX=215.932 EndY=-80.4316 EndZ=0
    g15: ArcOfCircle CenterX=207.583 CenterY=4 CenterZ=0 NormalX=0 NormalY=0 NormalZ=1 AngleXU=0 Radius=17 StartAngle=1.85815 EndAngle=3.57792
    g16: ArcOfCircle CenterX=184.801 CenterY=-67.3089 CenterZ=0 NormalX=0 NormalY=0 NormalZ=1 AngleXU=0 Radius=33.7833 StartAngle=5.88425 EndAngle=6.71952
    g17: LineSegment StartX=192.176 StartY=-3.18451 StartZ=0 EndX=215.42 EndY=-53.0314 EndZ=0
    g18: Circle CenterX=5.6 CenterY=34.8 CenterZ=0 NormalX=0 NormalY=0 NormalZ=1 AngleXU=0 Radius=1.8
    g19: Circle CenterX=5.6 CenterY=7.6 CenterZ=0 NormalX=0 NormalY=0 NormalZ=1 AngleXU=0 Radius=1.8
    g20: Circle CenterX=78.51 CenterY=34.8 CenterZ=0 NormalX=0 NormalY=0 NormalZ=1 AngleXU=0 Radius=1.8
    g21: Circle CenterX=78.51 CenterY=7.6 CenterZ=0 NormalX=0 NormalY=0 NormalZ=1 AngleXU=0 Radius=1.8
    g22: Circle CenterX=184.08 CenterY=34.8 CenterZ=0 NormalX=0 NormalY=0 NormalZ=1 AngleXU=0 Radius=1.8
    g23: Circle CenterX=179.305 CenterY=-76.8316 CenterZ=0 NormalX=0 NormalY=0 NormalZ=1 AngleXU=0 Radius=1.8
    g24: Circle CenterX=213.443 CenterY=-76.8316 CenterZ=0 NormalX=0 NormalY=0 NormalZ=1 AngleXU=0 Radius=1.8
    g25: Circle CenterX=19 CenterY=21.2 CenterZ=0 NormalX=0 NormalY=0 NormalZ=1 AngleXU=0 Radius=6.3
    g26: Circle CenterX=42 CenterY=21.2 CenterZ=0 NormalX=0 NormalY=0 NormalZ=1 AngleXU=0 Radius=6.3
    g27: Circle CenterX=65 CenterY=21.2 CenterZ=0 NormalX=0 NormalY=0 NormalZ=1 AngleXU=0 Radius=6.3
    g28: LineSegment StartX=132.428 StartY=20 StartZ=0 EndX=144.053 EndY=20 EndZ=0
    g29: LineSegment StartX=147.645 StartY=8.94427 StartZ=0 EndX=144.053 EndY=20 EndZ=0
  constraints (65):
    c: Coincident(g0,g-4)
    c: Coincident(g0,g-5)
    c: Coincident(g1,g0)
    c: Coincident(g1,g-6)
    c: Coincident(g2,g1)
    c: Coincident(g2,g-7)
    c: Coincident(g3,g2)
    c: Coincident(g3,g-8)
    c: Coincident(g4,g0)
    c: Coincident(g4,g-16)
    c: Coincident(g5,g4)
    c: Coincident(g5,g-16)
    c: Coincident(g6,g-20)
    c: Coincident(g6,g-21)
    c: Coincident(g7,g6)
    c: Coincident(g7,g-23)
    c: Coincident(g8,g7)
    c: Coincident(g8,g-22)
    c: Coincident(g9,g8)
    c: Coincident(g9,g6)
    c: Equal(g10,g-8)
    c: Coincident(g10,g3)
    c: Coincident(g10,g-9)
    c: Coincident(g11,g10)
    c: Coincident(g11,g-10)
    c: Equal(g12,g-10)
    c: Coincident(g12,g11)
    c: Coincident(g12,g-11)
    c: Coincident(g13,g12)
    c: Coincident(g13,g-12)
    c: Coincident(g14,g13)
    c: Coincident(g14,g-13)
    c: Equal(g15,g-15)
    c: Coincident(g15,g5)
    c: Coincident(g15,g-15)
    c: Equal(g16,g-13)
    c: Coincident(g16,g14)
    c: Coincident(g16,g-14)
    c: Coincident(g17,g15)
    c: Coincident(g17,g16)
    c: Equal(g18,g-28)
    c: Equal(g19,g-29)
    c: Equal(g20,g-26)
    c: Equal(g21,g-27)
    c: Equal(g22,g-17)
    c: Equal(g24,g-25)
    c: Equal(g23,g-24)
    c: Coincident(g23,g-24)
    c: Coincident(g24,g-25)
    c: Coincident(g22,g-17)
    c: Coincident(g20,g-26)
    c: Coincident(g21,g-27)
    c: Coincident(g18,g-28)
    c: Coincident(g19,g-29)
    c: Equal(g25,g-30)
    c: Equal(g26,g-31)
    c: Equal(g27,g-32)
    c: Coincident(g25,g-30)
    c: Coincident(g26,g-31)
    c: Coincident(g27,g-32)
    c: Parallel(g28,g11)
    c: Parallel(g29,g13)
    c: Coincident(g28,g11)
    c: Coincident(g29,g12)
    c: Coincident(g29,g28)
FEATURE [PartDesign::Pad] Pad019
  Direction = (0,1,-2e-16)
  Length = 2
  Length2 = 10
  Profile = -> Sketch133
  ReferenceAxis = -> Sketch133 [N_Axis]
  Refine = true
  Suppressed = false
  Type = 0
FEATURE [Sketcher::SketchObject] Sketch091  label="Sketch091 - forma anteriore"
  ArcFitTolerance = 1e-06
  AttachmentSupport = -> [Pad019]
  ExternalGeometry = -> [Binder]
  FullyConstrained = true
  MakeInternals = false
  MapMode = 5
  Placement = pos=(0,2,0) rot=(0,0.707107,0.707107;3.14159rad)
  sketch-geometry (12):
    g0: Circle CenterX=5.6 CenterY=34.8 CenterZ=0 NormalX=0 NormalY=0 NormalZ=1 AngleXU=0 Radius=1.8
    g1: Circle CenterX=5.6 CenterY=7.6 CenterZ=0 NormalX=0 NormalY=0 NormalZ=1 AngleXU=0 Radius=1.8
    g2: Circle CenterX=78.51 CenterY=34.8 CenterZ=0 NormalX=0 NormalY=0 NormalZ=1 AngleXU=0 Radius=1.8
    g3: Circle CenterX=78.51 CenterY=7.6 CenterZ=0 NormalX=0 NormalY=0 NormalZ=1 AngleXU=0 Radius=1.8
    g4: LineSegment StartX=0 StartY=39.2 StartZ=0 EndX=0 EndY=3.2 EndZ=0
    g5: LineSegment StartX=0 StartY=3.2 StartZ=0 EndX=82.8 EndY=3.2 EndZ=0
    g6: LineSegment StartX=82.8 StartY=3.2 StartZ=0 EndX=82.8 EndY=39.2 EndZ=0
    g7: LineSegment StartX=82.8 StartY=39.2 StartZ=0 EndX=0 EndY=39.2 EndZ=0
    g8: ArcOfCircle CenterX=19 CenterY=21.2 CenterZ=0 NormalX=0 NormalY=0 NormalZ=1 AngleXU=0 Radius=10 StartAngle=1.5708 EndAngle=4.71239
    g9: ArcOfCircle CenterX=65 CenterY=21.2 CenterZ=0 NormalX=0 NormalY=0 NormalZ=1 AngleXU=0 Radius=10 StartAngle=4.71239 EndAngle=7.85398
    g10: LineSegment StartX=19 StartY=31.2 StartZ=0 EndX=65 EndY=31.2 EndZ=0
    g11: LineSegment StartX=19 StartY=11.2 StartZ=0 EndX=65 EndY=11.2 EndZ=0
  constraints (25):
    c: Equal(g2,g-7)
    c: Equal(g3,g-8)
    c: Equal(g1,g-13)
    c: Equal(g0,g-12)
    c: Coincident(g0,g-12)
    c: Coincident(g1,g-13)
    c: Coincident(g3,g-8)
    c: Coincident(g2,g-7)
    c: Coincident(g4,g-4)
    c: Coincident(g4,g-5)
    c: Coincident(g5,g4)
    c: Coincident(g5,g-6)
    c: Coincident(g6,g5)
    c: PointOnObject(g6,g-3)
    c: Vertical(g6)
    c: Coincident(g7,g6)
    c: Coincident(g7,g4)
    c: Tangent(g8,g10) = 1.5708
    c: Tangent(g8,g11) = -1.5708
    c: Tangent(g9,g10) = 1.5708
    c: Tangent(g9,g11) = -1.5708
    c: Equal(g8,g9)
    c: Radius(g8) = 10
    c: Coincident(g8,g-11)
    c: Coincident(g9,g-9)
FEATURE [Sketcher::SketchObject] Sketch093  label="Sketch093 - scavi interni pulsanti"
  ArcFitTolerance = 1e-06
  AttachmentSupport = -> [Pad019]
  ExternalGeometry = -> [Binder]
  FullyConstrained = true
  MakeInternals = false
  MapMode = 5
  Placement = pos=(0,1.8e-15,0) rot=(1,0,0;1.5708rad)
  sketch-geometry (3):
    g0: Circle CenterX=-65 CenterY=21.2 CenterZ=0 NormalX=0 NormalY=0 NormalZ=1 AngleXU=0 Radius=7.3
    g1: Circle CenterX=-42 CenterY=21.2 CenterZ=0 NormalX=0 NormalY=0 NormalZ=1 AngleXU=0 Radius=7.3
    g2: Circle CenterX=-19 CenterY=21.2 CenterZ=0 NormalX=0 NormalY=0 NormalZ=1 AngleXU=0 Radius=7.3
  constraints (6):
    c: Coincident(g0,g-3)
    c: Coincident(g1,g-4)
    c: Coincident(g2,g-5)
    c: Diameter(g0) = 14.6
    c: Diameter(g1) = 14.6
    c: Diameter(g2) = 14.6
FEATURE [Sketcher::SketchObject] Sketch094  label="Sketch094 - forma centrale"
  ArcFitTolerance = 1e-06
  AttachmentSupport = -> [Pad019]
  ExternalGeometry = -> [Binder]
  FullyConstrained = true
  MakeInternals = false
  MapMode = 5
  Placement = pos=(0,2,0) rot=(0,0.707107,0.707107;3.14159rad)
  sketch-geometry (4):
    g0: LineSegment StartX=137.815 StartY=39.2 StartZ=0 EndX=142.655 EndY=24.303 EndZ=0
    g1: LineSegment StartX=110.815 StartY=24.303 StartZ=0 EndX=142.655 EndY=24.303 EndZ=0
    g2: LineSegment StartX=137.815 StartY=39.2 StartZ=0 EndX=110.815 EndY=39.2 EndZ=0
    g3: ArcOfCircle CenterX=92.2534 CenterY=31.7515 CenterZ=0 NormalX=0 NormalY=0 NormalZ=1 AngleXU=0 Radius=20 StartAngle=5.90156 EndAngle=6.66481
  constraints (12):
    c: PointOnObject(g0,g-3)
    c: Tangent(g0,g-5)
    c: Horizontal(g1)
    c: Coincident(g1,g0)
    c: Coincident(g2,g0)
    c: PointOnObject(g2,g-3)
    c: DistanceX(g2,g2) = 27
    c: Vertical(g1,g2)
    c: Coincident(g3,g2)
    c: Radius(g3) = 20
    c: Coincident(g3,g1)
    c: DistanceY(g-6,g0) = 4
FEATURE [Sketcher::SketchObject] Sketch095  label="Sketch095 - forma posteriore"
  ArcFitTolerance = 1e-06
  AttachmentSupport = -> [Pad019]
  ExternalGeometry = -> [Binder]
  FullyConstrained = true
  MakeInternals = false
  MapMode = 5
  Placement = pos=(0,2,0) rot=(0,0.707107,0.707107;3.14159rad)
  sketch-geometry (15):
    g0: LineSegment StartX=137.815 StartY=39.2 StartZ=0 EndX=143.955 EndY=20.303 EndZ=0
    g1: LineSegment StartX=143.955 StartY=20.303 StartZ=0 EndX=190.141 EndY=20.303 EndZ=0
    g2: ArcOfCircle CenterX=184.08 CenterY=34.8 CenterZ=0 NormalX=0 NormalY=0 NormalZ=1 AngleXU=0 Radius=3.5 StartAngle=3.49066 EndAngle=4.71239
    g3: LineSegment StartX=180.791 StartY=33.6029 StartZ=0 EndX=178.754 EndY=39.2 EndZ=0
    g4: LineSegment StartX=184.08 StartY=31.3 StartZ=0 EndX=186.139 EndY=31.3 EndZ=0
    g5: LineSegment StartX=190.141 StartY=20.303 StartZ=0 EndX=186.139 EndY=31.3 EndZ=0
    g6: LineSegment StartX=137.815 StartY=39.2 StartZ=0 EndX=156.815 EndY=39.2 EndZ=0
    g7: LineSegment StartX=178.754 StartY=39.2 StartZ=0 EndX=168.815 EndY=39.2 EndZ=0
    g8: LineSegment StartX=156.815 StartY=31.2 StartZ=0 EndX=168.815 EndY=31.2 EndZ=0
    g9: ArcOfCircle CenterX=176.411 CenterY=35.2 CenterZ=0 NormalX=0 NormalY=0 NormalZ=1 AngleXU=0 Radius=20 StartAngle=2.94023 EndAngle=3.34295
    g10: ArcOfCircle CenterX=188.411 CenterY=35.2 CenterZ=0 NormalX=0 NormalY=0 NormalZ=1 AngleXU=0 Radius=20 StartAngle=2.94023 EndAngle=3.34295
    g11: LineSegment StartX=157.815 StartY=39.2 StartZ=0 EndX=167.815 EndY=39.2 EndZ=0
    g12: LineSegment StartX=157.436 StartY=36.2 StartZ=0 EndX=167.436 EndY=36.2 EndZ=0
    g13: ArcOfCircle CenterX=177.411 CenterY=35.2 CenterZ=0 NormalX=0 NormalY=0 NormalZ=1 AngleXU=0 Radius=20 StartAngle=2.94023 EndAngle=3.09157
    g14: ArcOfCircle CenterX=187.411 CenterY=35.2 CenterZ=0 NormalX=0 NormalY=0 NormalZ=1 AngleXU=0 Radius=20 StartAngle=2.94023 EndAngle=3.09157
  constraints (46):
    c: PointOnObject(g0,g-3)
    c: Tangent(g0,g-6)
    c: Coincident(g1,g0)
    c: Horizontal(g1)
    c: Radius(g2) = 3.5
    c: Coincident(g2,g-5)
    c: PointOnObject(g3,g-3)
    c: Parallel(g3,g-4)
    c: Tangent(g3,g2) = 1.5708
    c: Horizontal(g4)
    c: Tangent(g4,g2) = -1.5708
    c: Coincident(g5,g1)
    c: Parallel(g5,g-4)
    c: Coincident(g5,g4)
    c: DistanceX(g4,g-8) = 3.8
    c: Coincident(g6,g0)
    c: PointOnObject(g6,g-3)
    c: Coincident(g7,g3)
    c: PointOnObject(g7,g-3)
    c: Horizontal(g8)
    c: DistanceX(g6,g7) = 12
    c: Vertical(g8,g6)
    c: Vertical(g7,g8)
    c: DistanceY(g8,g6) = 8
    c: Coincident(g9,g8)
    c: Coincident(g9,g6)
    c: Coincident(g10,g7)
    c: Coincident(g10,g8)
    c: Radius(g9) = 20
    c: Radius(g10) = 20
    c: PointOnObject(g11,g-3)
    c: PointOnObject(g11,g-3)
    c: DistanceX(g11,g11) = 10
    c: DistanceX(g6,g11) = 1
    c: Horizontal(g12)
    c: Equal(g12,g11)
    c: DistanceY(g12,g11) = 3
    c: Coincident(g13,g11)
    c: Coincident(g13,g12)
    c: Radius(g13) = 20
    c: Coincident(g14,g11)
    c: Coincident(g14,g12)
    c: Radius(g14) = 20
    c: DistanceX(g0,g6) = 19
    c: Horizontal(g9,g13)
    c: Horizontal(g0,g-4)
FEATURE [Sketcher::SketchObject] Sketch096  label="Sketch096 - forma impugnatura"
  ArcFitTolerance = 1e-06
  AttachmentSupport = -> [Pad019]
  ExternalGeometry = -> [Binder]
  FullyConstrained = true
  MakeInternals = false
  MapMode = 5
  Placement = pos=(0,2,0) rot=(0,0.707107,0.707107;3.14159rad)
  sketch-geometry (8):
    g0: LineSegment StartX=176.685 StartY=-80.4316 StartZ=0 EndX=143.955 EndY=20.303 EndZ=0
    g1: LineSegment StartX=176.685 StartY=-80.4316 StartZ=0 EndX=215.932 EndY=-80.4316 EndZ=0
    g2: Circle CenterX=179.305 CenterY=-76.8316 CenterZ=0 NormalX=0 NormalY=0 NormalZ=1 AngleXU=0 Radius=3
    g3: Circle CenterX=213.443 CenterY=-76.8316 CenterZ=0 NormalX=0 NormalY=0 NormalZ=1 AngleXU=0 Radius=3
    g4: LineSegment StartX=143.955 StartY=20.303 StartZ=0 EndX=202.765 EndY=20.303 EndZ=0
    g5: LineSegment StartX=215.42 StartY=-53.0314 StartZ=0 EndX=192.176 EndY=-3.18451 EndZ=0
    g6: ArcOfCircle CenterX=184.801 CenterY=-67.3089 CenterZ=0 NormalX=0 NormalY=0 NormalZ=1 AngleXU=0 Radius=33.7833 StartAngle=5.88425 EndAngle=6.71952
    g7: ArcOfCircle CenterX=207.583 CenterY=4 CenterZ=0 NormalX=0 NormalY=0 NormalZ=1 AngleXU=0 Radius=17 StartAngle=1.85815 EndAngle=3.57792
  constraints (19):
    c: Coincident(g0,g-4)
    c: PointOnObject(g0,g-3)
    c: Horizontal(g0,g-7)
    c: Coincident(g1,g0)
    c: Coincident(g1,g-5)
    c: Diameter(g2) = 6
    c: Diameter(g3) = 6
    c: Coincident(g2,g-9)
    c: Coincident(g3,g-10)
    c: Coincident(g4,g0)
    c: Coincident(g5,g-6)
    c: Coincident(g6,g1)
    c: Coincident(g6,g5)
    c: Equal(g-5,g6)
    c: Coincident(g5,g-7)
    c: Coincident(g4,g-7)
    c: Tangent(g7,g-7)
    c: Coincident(g7,g4)
    c: Coincident(g7,g5)
FEATURE [Sketcher::SketchObject] Sketch097
  ArcFitTolerance = 1e-06
  AttachmentSupport = -> [Pad019]
  ExternalGeometry = -> [Binder]
  FullyConstrained = true
  MakeInternals = false
  MapMode = 5
  Placement = pos=(0,2,0) rot=(0,0.707107,0.707107;3.14159rad)
  sketch-geometry (4):
    g0: LineSegment StartX=90 StartY=36.8 StartZ=0 EndX=108 EndY=36.8 EndZ=0
    g1: LineSegment StartX=108 StartY=36.8 StartZ=0 EndX=108 EndY=26.8 EndZ=0
    g2: LineSegment StartX=108 StartY=26.8 StartZ=0 EndX=90 EndY=26.8 EndZ=0
    g3: ArcOfCircle CenterX=94 CenterY=31.8 CenterZ=0 NormalX=0 NormalY=0 NormalZ=1 AngleXU=0 Radius=6.40312 StartAngle=2.24554 EndAngle=4.03765
  constraints (13):
    c: Horizontal(g0)
    c: Coincident(g1,g0)
    c: Vertical(g1)
    c: DistanceX(g0,g0) = 18
    c: DistanceY(g1,g1) = 10
    c: Coincident(g2,g1)
    c: Horizontal(g2)
    c: Equal(g2,g0)
    c: DistanceY(g0,g-3) = 2.4
    c: Coincident(g3,g0)
    c: Coincident(g3,g2)
    c: DistanceX(g2,g3) = 4
    c: DistanceX(g-3,g0) = 90
FEATURE [PartDesign::Chamfer] Chamfer015
  Angle = 45
  Base = -> Pad019 [Edge19,Edge22,Edge79]
  BaseFeature = -> Pad019
  ChamferType = 0
  FlipDirection = false
  Refine = true
  Size = 1.9
  Size2 = 1
  SupportTransform = false
  Suppressed = false
  UseAllEdges = false
FEATURE [PartDesign::Pocket] Pocket002
  BaseFeature = -> Chamfer015
  Direction = (0,1,-2e-16)
  Length = 1.2
  Length2 = 5
  Profile = -> Sketch093
  ReferenceAxis = -> Sketch093 [N_Axis]
  Refine = true
  Suppressed = false
  Type = 0
FEATURE [PartDesign::Pad] Pad005
  BaseFeature = -> Pocket002
  Direction = (0,1,-2e-16)
  Length = 1.6
  Length2 = 10
  Profile = -> Sketch091
  ReferenceAxis = -> Sketch091 [N_Axis]
  Refine = true
  Suppressed = false
  Type = 0
FEATURE [Sketcher::SketchObject] Sketch092  label="Sketch092 - scavi per viti anteriori"
  ArcFitTolerance = 1e-06
  AttachmentSupport = -> [Pad005]
  ExternalGeometry = -> [Binder]
  FullyConstrained = true
  MakeInternals = false
  MapMode = 5
  Placement = pos=(0,3.6,0) rot=(0,0.707107,0.707107;3.14159rad)
  sketch-geometry (20):
    g0: ArcOfCircle CenterX=5.6 CenterY=7.6 CenterZ=0 NormalX=0 NormalY=0 NormalZ=1 AngleXU=0 Radius=3.5 StartAngle=0 EndAngle=1.5708
    g1: ArcOfCircle CenterX=5.6 CenterY=34.8 CenterZ=0 NormalX=0 NormalY=0 NormalZ=1 AngleXU=0 Radius=3.5 StartAngle=4.71239 EndAngle=6.28319
    g2: ArcOfCircle CenterX=78.51 CenterY=34.8 CenterZ=0 NormalX=0 NormalY=0 NormalZ=1 AngleXU=0 Radius=3.5 StartAngle=3.14159 EndAngle=4.71239
    g3: ArcOfCircle CenterX=78.51 CenterY=7.6 CenterZ=0 NormalX=0 NormalY=0 NormalZ=1 AngleXU=0 Radius=3.5 StartAngle=1.5708 EndAngle=3.14159
    g4: LineSegment StartX=0 StartY=3.2 StartZ=0 EndX=0 EndY=11.1 EndZ=0
    g5: LineSegment StartX=0 StartY=11.1 StartZ=0 EndX=5.6 EndY=11.1 EndZ=0
    g6: LineSegment StartX=0 StartY=3.2 StartZ=0 EndX=9.1 EndY=3.2 EndZ=0
    g7: LineSegment StartX=9.1 StartY=3.2 StartZ=0 EndX=9.1 EndY=7.6 EndZ=0
    g8: LineSegment StartX=0 StartY=39.2 StartZ=0 EndX=0 EndY=31.3 EndZ=0
    g9: LineSegment StartX=0 StartY=31.3 StartZ=0 EndX=5.6 EndY=31.3 EndZ=0
    g10: LineSegment StartX=0 StartY=39.2 StartZ=0 EndX=9.1 EndY=39.2 EndZ=0
    g11: LineSegment StartX=9.1 StartY=39.2 StartZ=0 EndX=9.1 EndY=34.8 EndZ=0
    g12: LineSegment StartX=82.8 StartY=39.2 StartZ=0 EndX=75.01 EndY=39.2 EndZ=0
    g13: LineSegment StartX=82.8 StartY=39.2 StartZ=0 EndX=82.8 EndY=31.3 EndZ=0
    g14: LineSegment StartX=82.8 StartY=31.3 StartZ=0 EndX=78.51 EndY=31.3 EndZ=0
    g15: LineSegment StartX=82.8 StartY=3.2 StartZ=0 EndX=75.01 EndY=3.2 EndZ=0
    g16: LineSegment StartX=75.01 StartY=3.2 StartZ=0 EndX=75.01 EndY=7.6 EndZ=0
    g17: LineSegment StartX=82.8 StartY=3.2 StartZ=0 EndX=82.8 EndY=11.1 EndZ=0
    g18: LineSegment StartX=82.8 StartY=11.1 StartZ=0 EndX=78.51 EndY=11.1 EndZ=0
    g19: LineSegment StartX=75.01 StartY=39.2 StartZ=0 EndX=75.01 EndY=34.8 EndZ=0
  constraints (48):
    c: Radius(g0) = 3.5
    c: Coincident(g0,g-10)
    c: Radius(g1) = 3.5
    c: Coincident(g1,g-9)
    c: Radius(g2) = 3.5
    c: Coincident(g2,g-8)
    c: Radius(g3) = 3.5
    c: Coincident(g3,g-7)
    c: Coincident(g4,g-5)
    c: PointOnObject(g4,g-4)
    c: Coincident(g5,g4)
    c: Horizontal(g5)
    c: Coincident(g6,g4)
    c: PointOnObject(g6,g-5)
    c: Coincident(g7,g6)
    c: Vertical(g7)
    c: Coincident(g8,g-4)
    c: PointOnObject(g8,g-4)
    c: Coincident(g9,g8)
    c: Horizontal(g9)
    c: Coincident(g10,g8)
    c: PointOnObject(g10,g-3)
    c: Coincident(g11,g10)
    c: Vertical(g11)
    c: PointOnObject(g12,g-3)
    c: PointOnObject(g12,g-3)
    c: Coincident(g13,g12)
    c: Vertical(g13)
    c: Coincident(g14,g13)
    c: Horizontal(g14)
    c: Coincident(g15,g-6)
    c: PointOnObject(g15,g-5)
    c: Coincident(g16,g15)
    c: Vertical(g16)
    c: Coincident(g17,g15)
    c: Coincident(g18,g17)
    c: Horizontal(g18)
    c: Tangent(g3,g18) = -1.5708
    c: Tangent(g16,g3) = 1.5708
    c: Coincident(g19,g12)
    c: Vertical(g19)
    c: Tangent(g2,g19) = -1.5708
    c: Tangent(g2,g14) = 1.5708
    c: Tangent(g0,g7) = -1.5708
    c: Tangent(g0,g5) = 1.5708
    c: Tangent(g9,g1) = -1.5708
    c: Tangent(g1,g11) = 1.5708
    c: Tangent(g17,g13)
FEATURE [PartDesign::Pocket] Pocket001
  BaseFeature = -> Pad005
  Direction = (0,-1,2e-16)
  Length = 1.6
  Length2 = 5
  Profile = -> Sketch092
  ReferenceAxis = -> Sketch092 [N_Axis]
  Refine = true
  Suppressed = false
  Type = 0
FEATURE [PartDesign::Pad] Pad006
  BaseFeature = -> Pocket001
  Direction = (0,1,-2e-16)
  Length = 0.8
  Length2 = 10
  Profile = -> Sketch094
  ReferenceAxis = -> Sketch094 [N_Axis]
  Refine = true
  Suppressed = false
  Type = 0
FEATURE [PartDesign::Pad] Pad007
  BaseFeature = -> Pad006
  Direction = (0,1,-2e-16)
  Length = 2
  Length2 = 10
  Profile = -> Sketch095
  ReferenceAxis = -> Sketch095 [N_Axis]
  Refine = true
  Suppressed = false
  Type = 0
FEATURE [PartDesign::Pad] Pad008  label="Pad008 - forma impugnatura"
  BaseFeature = -> Pad007
  Direction = (0,1,-2e-16)
  Length = 1.6
  Length2 = 10
  Profile = -> Sketch096
  ReferenceAxis = -> Sketch096 [N_Axis]
  Refine = true
  Suppressed = false
  Type = 0
FEATURE [PartDesign::Pad] Pad009
  BaseFeature = -> Pad008
  Direction = (0,1,-2e-16)
  Length = 1.6
  Length2 = 10
  Profile = -> Sketch097
  ReferenceAxis = -> Sketch097 [N_Axis]
  Refine = true
  Suppressed = false
  Type = 0
FEATURE [Sketcher::SketchObject] Sketch098
  ArcFitTolerance = 1e-06
  AttachmentSupport = -> [Pad006]
  ExternalGeometry = -> [Binder]
  FullyConstrained = true
  MakeInternals = false
  MapMode = 5
  Placement = pos=(0,2.8,-7e-16) rot=(0,0.707107,0.707107;3.14159rad)
  sketch-geometry (4):
    g0: LineSegment StartX=118 StartY=39.2 StartZ=0 EndX=129 EndY=39.2 EndZ=0
    g1: LineSegment StartX=120.599 StartY=31.2 StartZ=0 EndX=131.599 EndY=31.2 EndZ=0
    g2: LineSegment StartX=129 StartY=39.2 StartZ=0 EndX=131.599 EndY=31.2 EndZ=0
    g3: LineSegment StartX=118 StartY=39.2 StartZ=0 EndX=120.599 EndY=31.2 EndZ=0
  constraints (12):
    c: PointOnObject(g0,g-3)
    c: PointOnObject(g0,g-3)
    c: DistanceX(g0,g0) = 11
    c: Horizontal(g1)
    c: Equal(g1,g0)
    c: Coincident(g2,g0)
    c: Coincident(g3,g0)
    c: Parallel(g-4,g2)
    c: Coincident(g1,g2)
    c: Coincident(g1,g3)
    c: DistanceY(g1,g0) = 8
    c: DistanceX(g-3,g0) = 118
FEATURE [Sketcher::SketchObject] Sketch099
  ArcFitTolerance = 1e-06
  AttachmentSupport = -> [Pad008]
  ExternalGeometry = -> [Binder]
  FullyConstrained = true
  MakeInternals = false
  MapMode = 5
  Placement = pos=(0,3.6,0) rot=(0,0.707107,0.707107;3.14159rad)
  sketch-geometry (13):
    g0: LineSegment StartX=192.176 StartY=-3.18451 StartZ=0 EndX=196.804 EndY=-13.1108 EndZ=0
    g1: LineSegment [constr] StartX=202.765 StartY=20.303 StartZ=0 EndX=181.223 EndY=20.303 EndZ=0
    g2: LineSegment [constr] StartX=181.223 StartY=20.303 StartZ=0 EndX=181.223 EndY=-3.18451 EndZ=0
    g3: ArcOfCircle CenterX=181.223 CenterY=-20.3764 CenterZ=0 NormalX=0 NormalY=0 NormalZ=1 AngleXU=0 Radius=17.1918 StartAngle=0.436332 EndAngle=1.57079
    g4: ArcOfEllipse CenterX=181.223 CenterY=8.55923 CenterZ=0 NormalX=0 NormalY=0 NormalZ=1 MajorRadius=23.4779 MinorRadius=11.7437 AngleXU=0 StartAngle=1.5708 EndAngle=4.71239
    g5: LineSegment [constr] StartX=204.701 StartY=8.55923 StartZ=0 EndX=157.745 EndY=8.55923 EndZ=0
    g6: LineSegment [constr] StartX=181.223 StartY=20.303 StartZ=0 EndX=181.223 EndY=-3.18451 EndZ=0
    g7: GeomPoint [constr] X=201.553 Y=8.55923 Z=0
    g8: GeomPoint [constr] X=160.894 Y=8.55923 Z=0
    g9: GeomPoint [constr] X=181.223 Y=-3.18451 Z=0
    g10: LineSegment StartX=181.223 StartY=20.303 StartZ=0 EndX=202.765 EndY=20.303 EndZ=0
    g11: ArcOfCircle CenterX=207.583 CenterY=4 CenterZ=0 NormalX=0 NormalY=0 NormalZ=1 AngleXU=0 Radius=17 StartAngle=1.85815 EndAngle=3.57792
    g12: LineSegment [constr] StartX=172.411 StartY=39.2 StartZ=0 EndX=192.176 EndY=-3.18451 EndZ=0
  constraints (27):
    c: Coincident(g1,g-7)
    c: Horizontal(g1)
    c: Coincident(g2,g1)
    c: Vertical(g2)
    c: Horizontal(g2,g0)
    c: Coincident(g3,g0)
    c: Coincident(g3,g2)
    c: InternalAlignment(g5-g8 -> g4) x4
    c: Horizontal(g5)
    c: PointOnObject(g4,g2)
    c: Coincident(g4,g1)
    c: DistanceX(g-3,g5) = 10.1
    c: Coincident(g4,g2)
    c: Tangent(g3,g-5)
    c: PointOnObject(g9,g4)
    c: PointOnObject(g9,g3)
    c: Tangent(g4,g3,g9) = 1.5708
    c: Coincident(g10,g1)
    c: Coincident(g10,g1)
    c: Equal(g11,g-4)
    c: Coincident(g11,g1)
    c: Coincident(g11,g0)
    c: PointOnObject(g12,g-6)
    c: PointOnObject(g1,g12)
    c: Tangent(g12,g-5) = -1.5708
    c: Tangent(g0,g-5) = -1.5708
    c: Horizontal(g9,g12)
FEATURE [Sketcher::SketchObject] Sketch106  label="Sketch106 - smusso impuniatura interno"
  ArcFitTolerance = 1e-06
  AttachmentSupport = -> [Pad008]
  ExternalGeometry = -> [Pad008]
  FullyConstrained = true
  MakeInternals = false
  MapMode = 5
  Placement = pos=(0,-1.585e-13,-80.4316) rot=(1,0,0;3.14159rad)
  sketch-geometry (9):
    g0: LineSegment StartX=-176.685 StartY=-3.6 StartZ=0 EndX=-176.685 EndY=1.1684e-12 EndZ=0
    g1: LineSegment [constr] StartX=-176.685 StartY=1.79e-14 StartZ=0 EndX=-176.685 EndY=1.1684e-12 EndZ=0
    g2: LineSegment [constr] StartX=-186.685 StartY=-3.6 StartZ=0 EndX=-186.685 EndY=1.1684e-12 EndZ=0
    g3: ArcOfEllipse CenterX=-186.685 CenterY=1.1684e-12 CenterZ=0 NormalX=0 NormalY=0 NormalZ=1 MajorRadius=10 MinorRadius=3.6 AngleXU=-3.14159 StartAngle=1.5708 EndAngle=3.14159
    g4: LineSegment [constr] StartX=-196.685 StartY=1.79e-14 StartZ=0 EndX=-176.685 EndY=1.79e-14 EndZ=0
    g5: LineSegment [constr] StartX=-186.685 StartY=-3.6 StartZ=0 EndX=-186.685 EndY=3.6 EndZ=0
    g6: GeomPoint [constr] X=-196.015 Y=1.53e-14 Z=0
    g7: GeomPoint [constr] X=-177.356 Y=1.85e-14 Z=0
    g8: LineSegment StartX=-176.685 StartY=-3.6 StartZ=0 EndX=-186.685 EndY=-3.6 EndZ=0
  constraints (15):
    c: PointOnObject(g2,g-3)
    c: Coincident(g1,g-5)
    c: DistanceY(g1,g1) = 0
    c: Coincident(g0,g1)
    c: DistanceX(g2,g-5) = 10
    c: Vertical(g2)
    c: Horizontal(g2,g0)
    c: InternalAlignment(g4-g7 -> g3) x4
    c: Coincident(g3,g2)
    c: Horizontal(g4)
    c: Coincident(g3,g0)
    c: Tangent(g0,g-5) = 1.5708
    c: Coincident(g3,g2)
    c: Coincident(g8,g0)
    c: Coincident(g8,g2)
FEATURE [Sketcher::SketchObject] Sketch107  label="Sketch107 - smusso impugnatura esterno"
  ArcFitTolerance = 1e-06
  AttachmentSupport = -> [Pad008]
  ExternalGeometry = -> [Pad008]
  FullyConstrained = true
  MakeInternals = false
  MapMode = 5
  Placement = pos=(0,-1.585e-13,-80.4316) rot=(1,0,0;3.14159rad)
  sketch-geometry (9):
    g0: LineSegment [constr] StartX=-215.932 StartY=1.79e-14 StartZ=0 EndX=-215.932 EndY=2.03e-14 EndZ=0
    g1: LineSegment StartX=-215.932 StartY=-3.6 StartZ=0 EndX=-215.932 EndY=2.04e-14 EndZ=0
    g2: LineSegment StartX=-215.932 StartY=-3.6 StartZ=0 EndX=-205.932 EndY=-3.6 EndZ=0
    g3: LineSegment [constr] StartX=-205.932 StartY=-3.6 StartZ=0 EndX=-205.932 EndY=2.04e-14 EndZ=0
    g4: ArcOfEllipse CenterX=-205.932 CenterY=2.03e-14 CenterZ=0 NormalX=0 NormalY=0 NormalZ=1 MajorRadius=10 MinorRadius=3.6 AngleXU=3.14159 StartAngle=1e-16 EndAngle=1.5708
    g5: LineSegment [constr] StartX=-215.932 StartY=1.79e-14 StartZ=0 EndX=-195.932 EndY=1.79e-14 EndZ=0
    g6: LineSegment [constr] StartX=-205.932 StartY=-3.6 StartZ=0 EndX=-205.932 EndY=3.6 EndZ=0
    g7: GeomPoint [constr] X=-215.262 Y=2.05e-14 Z=0
    g8: GeomPoint [constr] X=-196.602 Y=1.78e-14 Z=0
  constraints (16):
    c: Coincident(g0,g-6)
    c: PointOnObject(g0,g-6)
    c: DistanceY(g0,g0) = 0
    c: Coincident(g1,g-6)
    c: Coincident(g1,g0)
    c: Tangent(g2,g-3)
    c: DistanceX(g2,g2) = 10
    c: Coincident(g3,g2)
    c: Vertical(g3)
    c: Horizontal(g3,g0)
    c: InternalAlignment(g5-g8 -> g4) x4
    c: Coincident(g4,g3)
    c: Horizontal(g5)
    c: Coincident(g4,g0)
    c: Coincident(g4,g2)
    c: PointOnObject(g2,g1)
FEATURE [Sketcher::SketchObject] Sketch108
  ArcFitTolerance = 1e-06
  AttachmentOffset = pos=(0,0,-1.6) rot=(0,0,1;0rad)
  AttachmentSupport = -> [Pad008]
  ExternalGeometry = -> [Binder]
  FullyConstrained = true
  MakeInternals = false
  MapMode = 5
  Placement = pos=(0,2,4e-16) rot=(0,0.707107,0.707107;3.14159rad)
  sketch-geometry (14):
    g0: LineSegment StartX=192.176 StartY=-3.18451 StartZ=0 EndX=193.827 EndY=-6.72678 EndZ=0
    g1: LineSegment [constr] StartX=202.765 StartY=20.303 StartZ=0 EndX=181.223 EndY=20.303 EndZ=0
    g2: LineSegment [constr] StartX=181.223 StartY=20.303 StartZ=0 EndX=181.223 EndY=1.30297 EndZ=0
    g3: ArcOfCircle CenterX=181.223 CenterY=-12.6042 CenterZ=0 NormalX=0 NormalY=0 NormalZ=1 AngleXU=0 Radius=13.9072 StartAngle=0.436332 EndAngle=1.5708
    g4: ArcOfEllipse CenterX=181.223 CenterY=10.803 CenterZ=0 NormalX=0 NormalY=0 NormalZ=1 MajorRadius=14.4779 MinorRadius=9.5 AngleXU=0 StartAngle=1.5708 EndAngle=4.71239
    g5: LineSegment [constr] StartX=195.701 StartY=10.803 StartZ=0 EndX=166.745 EndY=10.803 EndZ=0
    g6: LineSegment [constr] StartX=181.223 StartY=20.303 StartZ=0 EndX=181.223 EndY=1.30297 EndZ=0
    g7: GeomPoint [constr] X=192.148 Y=10.803 Z=0
    g8: GeomPoint [constr] X=170.298 Y=10.803 Z=0
    g9: LineSegment StartX=181.223 StartY=20.303 StartZ=0 EndX=202.765 EndY=20.303 EndZ=0
    g10: ArcOfCircle CenterX=207.583 CenterY=4 CenterZ=0 NormalX=0 NormalY=0 NormalZ=1 AngleXU=0 Radius=17 StartAngle=1.85815 EndAngle=3.57792
    g11: LineSegment [constr] StartX=172.411 StartY=39.2 StartZ=0 EndX=192.176 EndY=-3.18451 EndZ=0
    g12: GeomPoint [constr] X=181.223 Y=1.30297 Z=0
    g13: GeomPoint [constr] X=181.223 Y=1.30297 Z=0
  constraints (28):
    c: Coincident(g1,g-7)
    c: Horizontal(g1)
    c: Coincident(g2,g1)
    c: Vertical(g2)
    c: Coincident(g3,g2)
    c: InternalAlignment(g5-g8 -> g4) x4
    c: Horizontal(g5)
    c: PointOnObject(g4,g2)
    c: Coincident(g4,g1)
    c: DistanceX(g-3,g5) = 19.1
    c: Coincident(g4,g2)
    c: Coincident(g9,g1)
    c: Coincident(g9,g1)
    c: Coincident(g10,g1)
    c: Coincident(g10,g0)
    c: PointOnObject(g11,g-6)
    c: PointOnObject(g1,g11)
    c: DistanceY(g2,g1) = 19
    c: Coincident(g10,g-4)
    c: PointOnObject(g12,g4)
    c: PointOnObject(g12,g3)
    c: Tangent(g11,g-5) = -1.5708
    c: Tangent(g0,g-5) = -1.5708
    c: Tangent(g3,g0) = 1.5708
    c: PointOnObject(g13,g4)
    c: PointOnObject(g13,g3)
    c: Tangent(g4,g3,g13) = 1.5708
    c: Horizontal(g11,g0)
FEATURE [Part::Part2DObjectPython] Clone2D  label="Sketch108 (2D)"  # Draft 2D object (typed FeaturePython)
  Fuse = false
  Objects = -> [Sketch108]
  Placement = pos=(0,2,4e-16) rot=(0,0.707107,0.707107;3.14159rad)
  Scale = (1,1,1)
FEATURE [Sketcher::SketchObject] Sketch109
  ArcFitTolerance = 1e-06
  AttachmentOffset = pos=(0,0,-3.5) rot=(0,0,1;0rad)
  AttachmentSupport = -> [Pad008]
  ExternalGeometry = -> [Binder]
  FullyConstrained = true
  MakeInternals = false
  MapMode = 5
  Placement = pos=(0,0.1,8e-16) rot=(0,0.707107,0.707107;3.14159rad)
  sketch-geometry (1):
    g0: GeomPoint X=197.47 Y=8.55923 Z=0
  constraints (1):
    c: Symmetric(g-7,g-5,g0)
FEATURE [PartDesign::Chamfer] Chamfer005
  Angle = 45
  Base = -> Pad009 [Edge215,Edge212]
  BaseFeature = -> Pad009
  ChamferType = 1
  FlipDirection = false
  Refine = true
  Size = 1.5
  Size2 = 2.8
  SupportTransform = false
  Suppressed = false
  UseAllEdges = false
FEATURE [Sketcher::SketchObject] Sketch111
  ArcFitTolerance = 1e-06
  AttachmentSupport = -> [Pad009]
  ExternalGeometry = -> [Pad009]
  FullyConstrained = true
  MakeInternals = false
  MapMode = 5
  Placement = pos=(0,3.6,-8e-16) rot=(0,0.707107,0.707107;3.14159rad)
  sketch-geometry (21):
    g0: LineSegment [constr] StartX=97 StartY=36.8 StartZ=0 EndX=97 EndY=26.8 EndZ=0
    g1: LineSegment StartX=97 StartY=28.6 StartZ=0 EndX=97 EndY=27.8 EndZ=0
    g2: LineSegment StartX=97 StartY=27.8 StartZ=0 EndX=108 EndY=27.8 EndZ=0
    g3: LineSegment StartX=108 StartY=27.8 StartZ=0 EndX=108 EndY=28.6 EndZ=0
    g4: LineSegment StartX=108 StartY=28.6 StartZ=0 EndX=97 EndY=28.6 EndZ=0
    g5: LineSegment StartX=97 StartY=35.8 StartZ=0 EndX=97 EndY=35 EndZ=0
    g6: LineSegment StartX=97 StartY=35 StartZ=0 EndX=108 EndY=35 EndZ=0
    g7: LineSegment StartX=108 StartY=35 StartZ=0 EndX=108 EndY=35.8 EndZ=0
    g8: LineSegment StartX=108 StartY=35.8 StartZ=0 EndX=97 EndY=35.8 EndZ=0
    g9: LineSegment StartX=97 StartY=30.4 StartZ=0 EndX=97 EndY=29.6 EndZ=0
    g10: LineSegment StartX=97 StartY=29.6 StartZ=0 EndX=108 EndY=29.6 EndZ=0
    g11: LineSegment StartX=108 StartY=29.6 StartZ=0 EndX=108 EndY=30.4 EndZ=0
    g12: LineSegment StartX=108 StartY=30.4 StartZ=0 EndX=97 EndY=30.4 EndZ=0
    g13: LineSegment StartX=97 StartY=34 StartZ=0 EndX=97 EndY=33.2 EndZ=0
    g14: LineSegment StartX=97 StartY=33.2 StartZ=0 EndX=108 EndY=33.2 EndZ=0
    g15: LineSegment StartX=108 StartY=33.2 StartZ=0 EndX=108 EndY=34 EndZ=0
    g16: LineSegment StartX=108 StartY=34 StartZ=0 EndX=97 EndY=34 EndZ=0
    g17: LineSegment StartX=97 StartY=32.2 StartZ=0 EndX=97 EndY=31.4 EndZ=0
    g18: LineSegment StartX=97 StartY=31.4 StartZ=0 EndX=108 EndY=31.4 EndZ=0
    g19: LineSegment StartX=108 StartY=31.4 StartZ=0 EndX=108 EndY=32.2 EndZ=0
    g20: LineSegment StartX=108 StartY=32.2 StartZ=0 EndX=97 EndY=32.2 EndZ=0
  constraints (54):
    c: Vertical(g0)
    c: PointOnObject(g0,g-3)
    c: PointOnObject(g0,g-4)
    c: DistanceX(g0,g-5) = 11
    c: Coincident(g1,g2)
    c: Coincident(g2,g3)
    c: Coincident(g3,g4)
    c: Coincident(g4,g1)
    c: Horizontal(g2)
    c: Horizontal(g4)
    c: Tangent(g1,g0)
    c: Tangent(g3,g-5)
    c: DistanceY(g2,g3) = 0.8
    c: Coincident(g5,g6)
    c: Coincident(g6,g7)
    c: Coincident(g7,g8)
    c: Coincident(g8,g5)
    c: Horizontal(g6)
    c: Horizontal(g8)
    c: DistanceY(g6,g7) = 0.8
    c: Coincident(g9,g10)
    c: Coincident(g10,g11)
    c: Coincident(g11,g12)
    c: Coincident(g12,g9)
    c: Horizontal(g10)
    c: Horizontal(g12)
    c: DistanceY(g10,g11) = 0.8
    c: Tangent(g5,g0)
    c: Tangent(g7,g-5)
    c: Tangent(g9,g0)
    c: Tangent(g11,g-5)
    c: Coincident(g13,g14)
    c: Coincident(g14,g15)
    c: Coincident(g15,g16)
    c: Coincident(g16,g13)
    c: Horizontal(g14)
    c: Horizontal(g16)
    c: DistanceY(g14,g15) = 0.8
    c: Tangent(g13,g0)
    c: Tangent(g15,g-5)
    c: Coincident(g17,g18)
    c: Coincident(g18,g19)
    c: Coincident(g19,g20)
    c: Coincident(g20,g17)
    c: Horizontal(g18)
    c: Horizontal(g20)
    c: DistanceY(g18,g19) = 0.8
    c: Tangent(g17,g0)
    c: Tangent(g19,g-5)
    c: DistanceY(g1,g9) = 1
    c: DistanceY(g9,g17) = 1
    c: DistanceY(g17,g13) = 1
    c: DistanceY(g13,g5) = 1
    c: DistanceY(g0,g1) = 1
FEATURE [PartDesign::Pocket] Pocket004
  BaseFeature = -> Chamfer005
  Direction = (0,-1,2e-16)
  Length = 1
  Length2 = 5
  Profile = -> Sketch111
  ReferenceAxis = -> Sketch111 [N_Axis]
  Refine = true
  Suppressed = false
  Type = 0
FEATURE [PartDesign::Pad] Pad010
  BaseFeature = -> Pocket004
  Direction = (0,1,-2e-16)
  Length = 1.2
  Length2 = 10
  Profile = -> Sketch098
  ReferenceAxis = -> Sketch098 [N_Axis]
  Refine = true
  Suppressed = false
  Type = 0
FEATURE [PartDesign::Chamfer] Chamfer006
  Angle = 45
  Base = -> Pad010 [Edge291]
  BaseFeature = -> Pad010
  ChamferType = 1
  FlipDirection = false
  Refine = true
  Size = 1
  Size2 = 6
  SupportTransform = false
  Suppressed = false
  UseAllEdges = false
FEATURE [Sketcher::SketchObject] Sketch110
  ArcFitTolerance = 1e-06
  AttachmentSupport = -> [Pad010]
  ExternalGeometry = -> [Sketch098]
  FullyConstrained = true
  MakeInternals = false
  MapMode = 5
  Placement = pos=(0,4,-9e-16) rot=(0,0.707107,0.707107;3.14159rad)
  sketch-geometry (8):
    g0: LineSegment StartX=119.69 StartY=34 StartZ=0 EndX=130.69 EndY=34 EndZ=0
    g1: LineSegment StartX=119.95 StartY=33.2 StartZ=0 EndX=130.95 EndY=33.2 EndZ=0
    g2: LineSegment StartX=119.137 StartY=35.7 StartZ=0 EndX=130.137 EndY=35.7 EndZ=0
    g3: LineSegment StartX=118.877 StartY=36.5 StartZ=0 EndX=129.877 EndY=36.5 EndZ=0
    g4: LineSegment StartX=118.877 StartY=36.5 StartZ=0 EndX=119.137 EndY=35.7 EndZ=0
    g5: LineSegment StartX=129.877 StartY=36.5 StartZ=0 EndX=130.137 EndY=35.7 EndZ=0
    g6: LineSegment StartX=119.69 StartY=34 StartZ=0 EndX=119.95 EndY=33.2 EndZ=0
    g7: LineSegment StartX=130.69 StartY=34 StartZ=0 EndX=130.95 EndY=33.2 EndZ=0
  constraints (24):
    c: Horizontal(g0)
    c: Horizontal(g1)
    c: Horizontal(g2)
    c: Horizontal(g3)
    c: Equal(g1,g-5)
    c: Equal(g0,g-5)
    c: Equal(g2,g-5)
    c: Equal(g3,g-5)
    c: PointOnObject(g0,g-3)
    c: PointOnObject(g1,g-3)
    c: PointOnObject(g2,g-3)
    c: PointOnObject(g3,g-3)
    c: Coincident(g4,g3)
    c: Coincident(g4,g2)
    c: Coincident(g5,g3)
    c: Coincident(g5,g2)
    c: Coincident(g6,g0)
    c: Coincident(g6,g1)
    c: Coincident(g7,g0)
    c: Coincident(g7,g1)
    c: DistanceY(g1,g0) = 0.8
    c: DistanceY(g2,g3) = 0.8
    c: DistanceY(g-5,g1) = 2
    c: DistanceY(g-5,g2) = 4.5
FEATURE [PartDesign::Pocket] Pocket003
  BaseFeature = -> Chamfer006
  Direction = (0,-1,2e-16)
  Length = 1
  Length2 = 5
  Profile = -> Sketch110
  ReferenceAxis = -> Sketch110 [N_Axis]
  Refine = true
  Suppressed = false
  Type = 0
FEATURE [PartDesign::SubtractivePipe] SubtractivePipe
  AuxilleryCurvelinear = true
  AuxillerySpineTangent = false
  BaseFeature = -> Pocket003
  Binormal = (0,0,0)
  Mode = 0
  Profile = -> Sketch106
  Refine = true
  Spine = -> Pad008 [Edge215]
  SpineTangent = false
  Suppressed = false
  Transformation = 0
  Transition = 0
FEATURE [PartDesign::SubtractivePipe] SubtractivePipe001
  AuxilleryCurvelinear = true
  AuxillerySpineTangent = false
  BaseFeature = -> SubtractivePipe
  Binormal = (0,0,0)
  Mode = 0
  Profile = -> Sketch107
  Refine = true
  Spine = -> Pad008 [Edge213,Edge216,Edge210]
  SpineTangent = false
  Suppressed = false
  Transformation = 0
  Transition = 0
FEATURE [PartDesign::SubtractiveLoft] SubtractiveLoft
  BaseFeature = -> SubtractivePipe001
  Closed = false
  Profile = -> Sketch099
  Refine = true
  Ruled = false
  Sections = -> [Sketch108]
  Suppressed = false
FEATURE [PartDesign::SubtractiveLoft] SubtractiveLoft001
  BaseFeature = -> SubtractiveLoft
  Closed = false
  Profile = -> Clone2D
  Refine = true
  Ruled = false
  Sections = -> [Sketch109]
  Suppressed = false
FEATURE [Sketcher::SketchObject] Sketch112
  ArcFitTolerance = 1e-06
  AttachmentSupport = -> [Pad008]
  ExternalGeometry = -> [Binder]
  FullyConstrained = true
  MakeInternals = false
  MapMode = 5
  Placement = pos=(0,3.6,0) rot=(0,0.707107,0.707107;3.14159rad)
  sketch-geometry (4):
    g0: LineSegment [constr] StartX=167.782 StartY=-53.0314 StartZ=0 EndX=215.42 EndY=-53.0314 EndZ=0
    g1: GeomPoint [constr] X=191.282 Y=-53.0314 Z=0
    g2: Circle CenterX=191.282 CenterY=-53.0314 CenterZ=0 NormalX=0 NormalY=0 NormalZ=1 AngleXU=0 Radius=11.5
    g3: Circle CenterX=191.282 CenterY=-53.0314 CenterZ=0 NormalX=0 NormalY=0 NormalZ=1 AngleXU=0 Radius=10.7
  constraints (9):
    c: Horizontal(g0)
    c: PointOnObject(g0,g-3)
    c: Diameter(g2) = 23
    c: Coincident(g2,g1)
    c: Diameter(g3) = 21.4
    c: Coincident(g3,g1)
    c: DistanceX(g0,g1) = 23.5
    c: PointOnObject(g1,g0)
    c: Coincident(g0,g-4)
FEATURE [PartDesign::Chamfer] Chamfer016
  Angle = 45
  Base = -> SubtractiveLoft001 [Edge118,Edge117,Edge119,Edge120,Edge109]
  BaseFeature = -> SubtractiveLoft001
  ChamferType = 0
  FlipDirection = false
  Refine = true
  Size = 1.5
  Size2 = 1
  SupportTransform = false
  Suppressed = false
  UseAllEdges = false
FEATURE [PartDesign::Chamfer] Chamfer017
  Angle = 45
  Base = -> Chamfer016 [Edge15]
  BaseFeature = -> Chamfer016
  ChamferType = 0
  FlipDirection = false
  Refine = true
  Size = 3.5
  Size2 = 1
  SupportTransform = false
  Suppressed = false
  UseAllEdges = false
FEATURE [PartDesign::Chamfer] Chamfer018
  Angle = 45
  Base = -> Chamfer017 [Edge10]
  BaseFeature = -> Chamfer017
  ChamferType = 0
  FlipDirection = false
  Refine = true
  Size = 3.5
  Size2 = 1
  SupportTransform = false
  Suppressed = false
  UseAllEdges = false
FEATURE [PartDesign::Chamfer] Chamfer019
  Angle = 45
  Base = -> Chamfer018 [Edge93,Edge140]
  BaseFeature = -> Chamfer018
  ChamferType = 0
  FlipDirection = false
  Refine = true
  Size = 1.9
  Size2 = 1
  SupportTransform = false
  Suppressed = false
  UseAllEdges = false
FEATURE [PartDesign::Fillet] Fillet009
  Base = -> Chamfer019 [Edge84]
  BaseFeature = -> Chamfer019
  Radius = 1.1
  Refine = true
  SupportTransform = false
  Suppressed = false
  UseAllEdges = false
FEATURE [PartDesign::Fillet] Fillet010
  Base = -> Fillet009 [Edge78]
  BaseFeature = -> Fillet009
  Radius = 1.9
  Refine = true
  SupportTransform = false
  Suppressed = false
  UseAllEdges = false
FEATURE [PartDesign::Pocket] Pocket005
  BaseFeature = -> Fillet010
  Direction = (0,-1,2e-16)
  Length = 0.8
  Length2 = 5
  Profile = -> Sketch112
  ReferenceAxis = -> Sketch112 [N_Axis]
  Refine = true
  Suppressed = false
  Type = 0
FEATURE [Part::Mirroring] Part__Mirroring  label="Pocket005 (Mirror #1)"
  Base = (0,0,0)
  Normal = (0,0,1)
  Source = -> Pocket005
FEATURE [Part::Part2DObjectPython] ShapeString001  # Draft 2D object (typed FeaturePython)
  FontFile = <path>
  Fuse = false
  Justification = 6
  JustificationReference = 0
  KeepLeftMargin = false
  MakeFace = true
  ObliqueAngle = 0
  Placement = pos=(-183.5,3.6,-57.5) rot=(0,0.707107,0.707107;3.14159rad)
  ScaleToSize = true
  Size = 10
  String = AS
  Tracking = 0
FEATURE [PartDesign::Pocket] Pocket013
  BaseFeature = -> Pocket005
  Direction = (-1e-16,-1,2e-16)
  Length = 1
  Length2 = 5
  Profile = -> ShapeString001
  ReferenceAxis = -> ShapeString001 [N_Axis]
  Refine = true
  Suppressed = false
  Type = 0
FEATURE [PartDesign::Body] Body006  label="lato SX"
  AllowCompound = false
  Group = -> [Binder,Pad019,Chamfer015,Pocket002,Sketch133,Sketch091,Pad005,Sketch092,Pocket001,Sketch093,Sketch094,Pad006,Sketch095,Pad007,Sketch096,Pad008,Sketch097,Pad009,Chamfer005,Pocket004,Sketch098,Pad010,Chamfer006,Pocket003,SubtractivePipe,SubtractivePipe001,Sketch099,Sketch106,Sketch107,Sketch108,Clone2D,Sketch109,SubtractiveLoft,SubtractiveLoft001,Sketch110,Sketch111,Sketch112,Chamfer016,Chamfer017,+7 more]
  Origin = -> Origin006
  Tip = -> Pocket013
note: 2 file-system paths scrubbed to <path> (originals preserved in the JSON sidecar)
